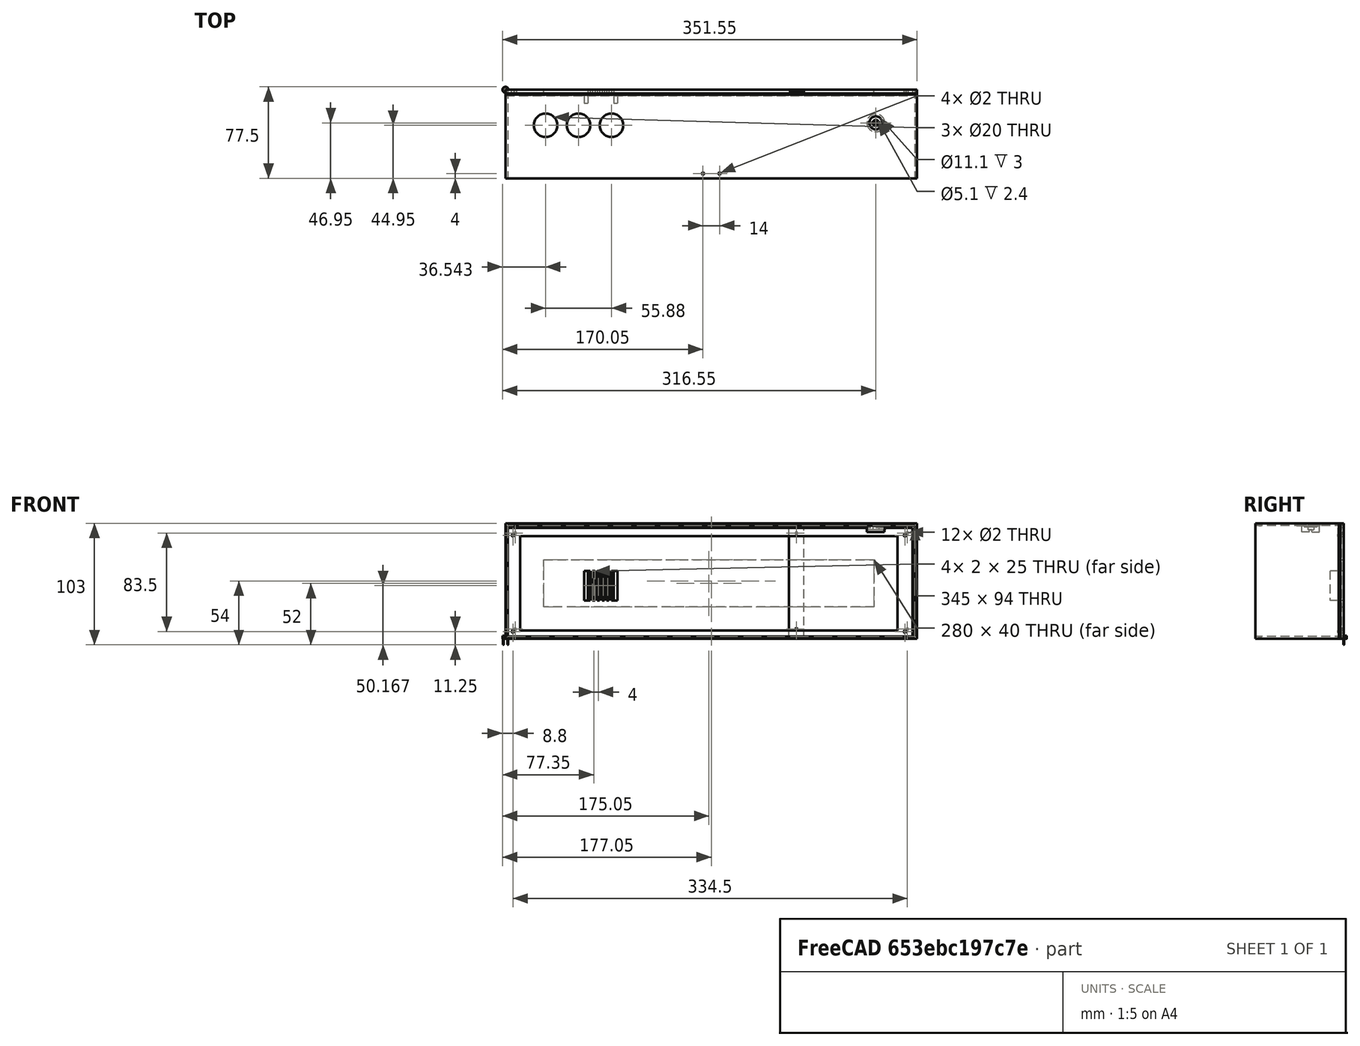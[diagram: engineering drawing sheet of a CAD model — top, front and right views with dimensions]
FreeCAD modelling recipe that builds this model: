
FCSTD DOCUMENT  (FreeCAD 1.0R39109 (Git))
Label: display
License: All rights reserved
LicenseURL: https://en.wikipedia.org/wiki/All_rights_reserved
objects: App::FeaturePython×42, App::Link×32, Sketcher::SketchObject×29, PartDesign::Plane×15, PartDesign::Pocket×10, PartDesign::Body×7, PartDesign::Pad×6, PartDesign::SubShapeBinder×5, PartDesign::Mirrored×4, App::DocumentObjectGroup×4, Spreadsheet::Sheet×2, PartDesign::MultiTransform×2, PartDesign::Line×2, Assembly::JointGroup×2, Assembly::AssemblyObject×2, PartDesign::FeatureBase×2, Assembly::ViewGroup×1, PartDesign::Point×1, PartDesign::Groove×1, PartDesign::Revolution×1, +2 more types
note: 161 computed .brp shape members not serialized (recipe doc carries the construction recipe); baked Part::Feature solids carry a one-line shape summary decoded from their .brp
EXTERNAL_REF file=Protoboard.FCStd obj=Spreadsheet004
EXTERNAL_REF file=grid.FCStd obj=Spreadsheet001
EXTERNAL_REF file=mount_stud.FCStd obj=Spreadsheet002
EXTERNAL_REF file=mount_bracket.FCStd obj=Spreadsheet
EXTERNAL_REF file=button.FCStd obj=Spreadsheet005
EXTERNAL_REF file=grid.FCStd obj=Body001
EXTERNAL_REF file=Protoboard.FCStd obj=Body007
EXTERNAL_REF file=mount_stud.FCStd obj=Body
EXTERNAL_REF file=button.FCStd obj=Body006
EXTERNAL_REF file=mount_bracket.FCStd obj=Body003
EXTERNAL_REF file=two_female_mount_bracket.FCStd obj=Body

FEATURE [Spreadsheet::Sheet] Spreadsheet  label="DisplaySS"
  cells = A1='Variant; B1='case_depth; C1='matrix_height; D1='matrix_width; E1='matrix_depth; F1='threaded_insert_depth; G1='threaded_insert_outer_diameter; H1='threaded_insert_safety_zone; I1='case_thickness; J1='grid_border_thickness; K1='grid_depth; L1='grid_intercell_spacing; M1='grid_cell_width; N1='led_x_count; O1='led_y_count; P1='grid_countersink_hole_depth; Q1='magnet_diameter; R1='magnet_height; S1='printer_tolerance_modifier; T1='screw_diameter; U1='mount_panel_exclusion_offset; V1='glass_thickness; W1='pcb_offset; X1='top_component_offset; Y1='photoresistor_diameter; Z1='photoresistor_truncated_width; AA1='photoresistor_height; AB1='top_component_horizontal_offset; AC1='top_component_spacing; AD1='photoresistor_ledge_size; AE1='back_plate_thickness; AF1='button_diameter; AG1='button_count; AH1='button_spacing; AI1='dht_height; AJ1='dht_width; AK1='dht_depth; AL1='dht_grill_diameter; A2==hiddenref(Body.Configuration.String); B2(case_depth)==.B3; C2(matrix_height)==.C3; D2(matrix_width)==.D3; E2(matrix_depth)==.E3; F2(threaded_insert_depth)==.F3; G2(threaded_insert_outer_diameter)==.G3; H2(threaded_insert_safety_zone)==.H3; I2(case_thickness)==.I3; J2(grid_border_thickness)==.J3; K2(grid_depth)==.K3; L2(grid_intercell_spacing)==.L3; M2(grid_cell_width)==.M3; N2(led_x_count)==.N3; O2(led_y_count)==.O3; P2(grid_countersink_hole_depth)==.P3; Q2(magnet_diameter)==.Q3; R2(magnet_height)==.R3; S2(printer_tolerance_modifier)==.S3; T2(screw_diameter)==.T3; U2(mount_panel_exclusion_offset)==.U3; V2(glass_thickness)==.V3; W2(pcb_offset)==.W3; X2(top_component_offset)==.X3; Y2(photoresistor_diameter)==.Y3; Z2(photoresistor_truncated_width)==.Z3; AA2(photoresistor_height)==.AA3; AB2(top_component_horizontal_offset)==.AB3; AC2(top_component_spacing)==.AC3; AD2(photoresistor_ledge_size)==.AD3; AE2(back_plate_thickness)==.AE3; AF2(button_diameter)==.AF3; AG2(button_count)==.AG3; AH2(button_spacing)==.AH3; AI2(dht_height)==.AI3; AJ2(dht_width)==.AJ3; AK2(dht_depth)==.AK3; AL2(dht_grill_diameter)==.AL3; A3='A; B3==75 mm; C3==80 mm; D3==320 mm; E3==2 mm; F3==4 mm; G3==5 mm; H3==2 mm; I3==2 mm; J3==3 mm; K3==8 mm; L3==1 mm; M3==9 mm; N3=32; O3=8; P3==3 mm; Q3==5 mm; R3==2.8 mm; S3==1 mm; T3==2 mm; U3==2 cm; V3==3 mm; W3==2 mm; X3==pcb_offset + <<Protoboard>>#<<ProtoboardSS>>.total_width / 2; Y3==5.1 mm; Z3==4.5 mm; AA3==2.4 mm; AB3==35 mm; AC3==0.5 cm; AD3==3 mm; AE3==4 mm; AF3==2.54 * 9 mm; AG3=3; AH3==2.54 * 2 mm; AI3==25.1 mm; AJ3==15.1 mm; AK3==7.7 mm; AL3==30 mm
  expr: .cells.Bind.B2.ZZ2 = tuple(.cells; <<B>> + str(hiddenref(Body.Configuration) + 3); <<ZZ>> + str(hiddenref(Body.Configuration) + 3))
FEATURE [Spreadsheet::Sheet] Spreadsheet001  label="CalculatedSS"
  cells = B1='grid_horizontal_padding; C1='grid_vertical_padding; D1='case_height; E1='case_width; F1='grid_width; G1='grid_height; H1='grid_matrix_width; I1='grid_matrix_height; J1='screw_horizontal_offset; K1='screw_vertical_offset; L1='grid_magnet_vertical_offset; M1='grid_magnet_horizontal_offset; N1='grid_magnet_depth; O1='case_clear_opening_height; P1='case_clear_opening_width; Q1='mounting_plate_thickness; R1='mount_bracket_face_size; S1='mount_bracket_length; T1='mount_bracket_draft_angle; U1='case_relative_magnet_horizontal_offset; V1='case_relative_magnet_vertical_offset; W1='mount_face_offset; X1='photoresistor_well_height; Y1='photoresistor_well_diameter; Z1='backplate_screw_offset_x; AA1='backplate_screw_offset_x; AB1='dht_vertical_offset; AC1='dht_horizontal_offset; AD1='pin_offset; AE1='protoboard_offset; AF1='protoboard_max_extent; AG1='protoboard_long_stud_clearance; AH1='button_mount_offset; AI1='button_pattern_extent; AJ1='back_plate_width; AK1='back_plate_height; AL1='split_offset; B2(grid_horizontal_padding)==<<DisplaySS>>.threaded_insert_outer_diameter + <<DisplaySS>>.threaded_insert_safety_zone * 2 + <<DisplaySS>>.grid_border_thickness + <<DisplaySS>>.grid_intercell_spacing / 2; C2(grid_vertical_padding)==grid#<<GridCalculatedSS>>.grid_vertical_padding; D2(case_height)==grid_height + <<DisplaySS>>.case_thickness * 2; E2(case_width)==grid_width + <<DisplaySS>>.case_thickness * 2; F2(grid_width)==grid_horizontal_padding * 2 + <<DisplaySS>>.matrix_width; G2(grid_height)==grid#<<GridCalculatedSS>>.grid_height; H2(grid_matrix_width)==grid_width - 2 * grid_horizontal_padding - 10 mm; I2(grid_matrix_height)=70; J2(screw_horizontal_offset)==grid_horizontal_padding / 2; K2(screw_vertical_offset)==mount_bracket_face_size / 2; L2(grid_magnet_vertical_offset)==grid#<<GridCalculatedSS>>.grid_magnet_vertical_offset; M2(grid_magnet_horizontal_offset)==grid#<<GridCalculatedSS>>.grid_magnet_horizontal_offset; N2(grid_magnet_depth)==<<DisplaySS>>.magnet_height * 2; O2(case_clear_opening_height)==grid_height; P2(case_clear_opening_width)==grid_width; Q2(mounting_plate_thickness)==<<DisplaySS>>.matrix_depth + 3 mm; R2(mount_bracket_face_size)==screw_horizontal_offset * 2; S2(mount_bracket_length)==mount_bracket_face_size / tan(mount_bracket_draft_angle) + <<DisplaySS>>.threaded_insert_depth; T2(mount_bracket_draft_angle)==35 deg; U2(case_relative_magnet_horizontal_offset)==grid_magnet_horizontal_offset + <<DisplaySS>>.case_thickness; V2(case_relative_magnet_vertical_offset)==grid_magnet_vertical_offset + <<DisplaySS>>.case_thickness; W2(mount_face_offset)==<<DisplaySS>>.case_depth - <<DisplaySS>>.grid_depth - mounting_plate_thickness; X2(photoresistor_well_height)==<<DisplaySS>>.glass_thickness + <<DisplaySS>>.photoresistor_height; Y2(photoresistor_well_diameter)==<<DisplaySS>>.photoresistor_diameter + <<DisplaySS>>.photoresistor_ledge_size * 2 + <<DisplaySS>>.case_thickness * 2; Z2(backplate_screw_offset_x)==mount_bracket_face_size / 2 + <<DisplaySS>>.case_thickness; AA2(backplate_screw_offset_y)==mount_bracket_face_size / 2 + <<DisplaySS>>.case_thickness; AB2(dht_vertical_offset)==case_height / 3; AC2(dht_horizontal_offset)==case_width / 5; AD2(pin_offset)==<<Protoboard>>#<<ProtoboardSS>>.first_pin_row_start; AE2(protoboard_offset)==40 mm; AF2(protoboard_max_extent)==protoboard_offset + <<Protoboard>>#<<ProtoboardSS>>.total_length; AG2(protoboard_long_stud_clearance)==<<mount_stud>>#<<MountStudSS>>.base_diameter / 2 - <<Protoboard>>#<<ProtoboardSS>>.mount_top_offset; AH2(button_mount_offset)==<<Protoboard>>#<<ProtoboardSS>>.mount_spacing_length / 2 - <<Protoboard>>#<<ProtoboardSS>>.pin_width / 2; AI2(button_pattern_extent)==<<DisplaySS>>.button_diameter * (<<DisplaySS>>.button_count - 1) + <<DisplaySS>>.button_spacing * (<<DisplaySS>>.button_count - 1); AJ2(back_plate_width)==case_width; AK2(back_plate_height)==case_height; AL2(split_offset)==253 mm
FEATURE [Sketcher::SketchObject] Sketch
  ArcFitTolerance = 1e-06
  AttachmentSupport = -> [XY_Plane]
  FullyConstrained = true
  MakeInternals = false
  MapMode = 3
  Placement = pos=(0,0,0) rot=(1,0,0;1.5708rad)
  expr: Constraints[10] = <<CalculatedSS>>.case_height
  expr: Constraints[9] = <<CalculatedSS>>.case_width
  sketch-geometry (4):
    g0: LineSegment StartX=0 StartY=0 StartZ=0 EndX=349 EndY=0 EndZ=0
    g1: LineSegment StartX=349 StartY=0 StartZ=0 EndX=349 EndY=98 EndZ=0
    g2: LineSegment StartX=349 StartY=98 StartZ=0 EndX=0 EndY=98 EndZ=0
    g3: LineSegment StartX=0 StartY=98 StartZ=0 EndX=0 EndY=0 EndZ=0
  constraints (11):
    c: Coincident(g0,g1)
    c: Coincident(g1,g2)
    c: Coincident(g2,g3)
    c: Coincident(g3,g0)
    c: Horizontal(g0)
    c: Horizontal(g2)
    c: Vertical(g1)
    c: Vertical(g3)
    c: Coincident(g0,g-1)
    c: Distance(g0) = 349
    c: Distance(g3) = 98
FEATURE [Sketcher::SketchObject] Sketch001
  ArcFitTolerance = 1e-06
  AttachmentSupport = -> [XY_Plane]
  FullyConstrained = true
  MakeInternals = false
  MapMode = 3
  Placement = pos=(0,0,0) rot=(1,0,0;1.5708rad)
  expr: Constraints[10] = <<CalculatedSS>>.case_width - <<DisplaySS>>.case_thickness
  expr: Constraints[11] = <<CalculatedSS>>.case_height - <<DisplaySS>>.case_thickness
  expr: Constraints[8] = <<DisplaySS>>.case_thickness
  expr: Constraints[9] = <<DisplaySS>>.case_thickness
  sketch-geometry (4):
    g0: LineSegment StartX=2 StartY=2 StartZ=0 EndX=347 EndY=2 EndZ=0
    g1: LineSegment StartX=347 StartY=2 StartZ=0 EndX=347 EndY=96 EndZ=0
    g2: LineSegment StartX=347 StartY=96 StartZ=0 EndX=2 EndY=96 EndZ=0
    g3: LineSegment StartX=2 StartY=96 StartZ=0 EndX=2 EndY=2 EndZ=0
  constraints (12):
    c: Coincident(g0,g1)
    c: Coincident(g1,g2)
    c: Coincident(g2,g3)
    c: Coincident(g3,g0)
    c: Horizontal(g0)
    c: Horizontal(g2)
    c: Vertical(g1)
    c: Vertical(g3)
    c: DistanceX(g-2,g0) = 2
    c: DistanceY(g-1,g0) = 2
    c: DistanceX(g-2,g1) = 347
    c: DistanceY(g-1,g1) = 96
FEATURE [PartDesign::Pad] Pad
  Direction = (0,-1,2e-16)
  Length = 75
  Length2 = 10
  Profile = -> Sketch
  ReferenceAxis = -> Sketch [N_Axis]
  Refine = true
  Suppressed = false
  Type = 0
  expr: Length = <<DisplaySS>>.case_depth
FEATURE [PartDesign::Pocket] Pocket
  BaseFeature = -> Pad
  Direction = (0,1,-2e-16)
  Length = 5
  Length2 = 5
  Profile = -> Sketch001
  ReferenceAxis = -> Sketch001 [N_Axis]
  Refine = true
  Reversed = true
  Suppressed = false
  Type = 1
FEATURE [PartDesign::Plane] DatumPlane
  AttachmentOffset = pos=(0,0,67) rot=(0,0,1;0rad)
  AttachmentSupport = -> [XZ_Plane]
  Length = 416.896
  MapMode = 2
  Placement = pos=(0,-67,1.49e-14) rot=(1,0,0;1.5708rad)
  ResizeMode = 0
  Width = 165.896
  expr: .AttachmentOffset.Base.z = <<DisplaySS>>.case_depth - <<DisplaySS>>.grid_depth
FEATURE [Sketcher::SketchObject] Sketch006  label="MountingPlateSketch"
  ArcFitTolerance = 1e-06
  AttachmentSupport = -> [XZ_Plane002]
  FullyConstrained = true
  MakeInternals = false
  MapMode = 5
  Placement = pos=(0,0,0) rot=(1,0,0;1.5708rad)
  expr: Constraints[10] = <<CalculatedSS>>.case_clear_opening_height
  expr: Constraints[9] = <<CalculatedSS>>.case_clear_opening_width
  sketch-geometry (4):
    g0: LineSegment StartX=0 StartY=0 StartZ=0 EndX=345 EndY=0 EndZ=0
    g1: LineSegment StartX=345 StartY=0 StartZ=0 EndX=345 EndY=94 EndZ=0
    g2: LineSegment StartX=345 StartY=94 StartZ=0 EndX=0 EndY=94 EndZ=0
    g3: LineSegment StartX=0 StartY=94 StartZ=0 EndX=0 EndY=0 EndZ=0
  constraints (11):
    c: Coincident(g0,g1)
    c: Coincident(g1,g2)
    c: Coincident(g2,g3)
    c: Coincident(g3,g0)
    c: Horizontal(g0)
    c: Horizontal(g2)
    c: Vertical(g1)
    c: Vertical(g3)
    c: Coincident(g0,g-1)
    c: Distance(g0) = 345
    c: Distance(g3) = 94
FEATURE [PartDesign::Pad] Pad002  label="MountingPlatePad"
  Direction = (0,-1,2e-16)
  Length = 5
  Length2 = 10
  Placement = pos=(0,0,0) rot=(1,0,0;1.5708rad)
  Profile = -> Sketch006
  ReferenceAxis = -> Sketch006 [N_Axis]
  Refine = true
  Suppressed = false
  Type = 0
  expr: Length = <<CalculatedSS>>.mounting_plate_thickness
FEATURE [Sketcher::SketchObject] Sketch007  label="Mounting Plate Screw Hole"
  ArcFitTolerance = 1e-06
  AttachmentSupport = -> [XZ_Plane002]
  FullyConstrained = true
  MakeInternals = false
  MapMode = 5
  Placement = pos=(0,0,0) rot=(1,0,0;1.5708rad)
  expr: Constraints[0] = <<DisplaySS>>.screw_diameter
  expr: Constraints[1] = <<CalculatedSS>>.screw_horizontal_offset
  expr: Constraints[2] = <<CalculatedSS>>.screw_vertical_offset
  sketch-geometry (1):
    g0: Circle CenterX=6.25 CenterY=6.25 CenterZ=0 NormalX=0 NormalY=0 NormalZ=1 AngleXU=0 Radius=1
  constraints (3):
    c: Diameter(g0) = 2
    c: DistanceX(g-2,g0) = 6.25
    c: DistanceY(g-1,g0) = 6.25
FEATURE [PartDesign::Pocket] Pocket004  label="MountingPlateScrewHolePocket"
  BaseFeature = -> Pad002
  Direction = (0,1,-2e-16)
  Length = 5
  Length2 = 5
  Placement = pos=(0,0,0) rot=(1,0,0;1.5708rad)
  Profile = -> Sketch007
  ReferenceAxis = -> Sketch007 [N_Axis]
  Refine = true
  Reversed = true
  Suppressed = false
  Type = 0
  expr: Length = <<CalculatedSS>>.mounting_plate_thickness
FEATURE [PartDesign::Plane] DatumPlane004  label="Mounting Case Horizontal Dividing Plane"
  AttachmentOffset = pos=(0,0,-47) rot=(0,0,1;0rad)
  AttachmentSupport = -> [XZ_Plane002]
  Length = 397.203
  MapMode = 3
  Placement = pos=(0,0,47) rot=(1,0,0;3.14159rad)
  ResizeMode = 0
  Width = 77.2029
  expr: .AttachmentOffset.Base.z = <<CalculatedSS>>.case_clear_opening_height / 2 * -1
FEATURE [PartDesign::Plane] DatumPlane005  label="MountingCaseVerticalDividingPlane"
  AttachmentOffset = pos=(0,0,172.5) rot=(0,0,1;0rad)
  AttachmentSupport = -> [YZ_Plane002]
  Length = 65.4272
  MapMode = 5
  Placement = pos=(172.5,0,0) rot=(0.57735,0.57735,0.57735;2.0944rad)
  ResizeMode = 0
  Width = 134.427
  expr: .AttachmentOffset.Base.z = <<CalculatedSS>>.case_clear_opening_width / 2
FEATURE [PartDesign::Mirrored] Mirrored004
  MirrorPlane = -> DatumPlane004
  Placement = pos=(0,0,0) rot=(1,0,0;1.5708rad)
  Refine = true
  Suppressed = false
  TransformMode = 0
FEATURE [PartDesign::Mirrored] Mirrored005
  MirrorPlane = -> DatumPlane005
  Placement = pos=(0,0,0) rot=(1,0,0;1.5708rad)
  Refine = true
  Suppressed = false
  TransformMode = 0
FEATURE [PartDesign::MultiTransform] MultiTransform003  label="MountingPlateScrewHoles"
  BaseFeature = -> Pocket004
  Originals = -> [Pocket004]
  Placement = pos=(0,0,0) rot=(1,0,0;1.5708rad)
  Refine = true
  Suppressed = false
  TransformMode = 0
  Transformations = -> [Mirrored004,Mirrored005]
FEATURE [PartDesign::Plane] DatumPlane006  label="MountingPlateFacePlane"
  AttachmentOffset = pos=(0,0,5) rot=(0,0,1;0rad)
  AttachmentSupport = -> [XZ_Plane002]
  Length = 411.967
  MapMode = 5
  Placement = pos=(0,-5,1.1e-15) rot=(1,0,0;1.5708rad)
  ResizeMode = 0
  Width = 160.967
  expr: .AttachmentOffset.Base.z = <<CalculatedSS>>.mounting_plate_thickness
FEATURE [Sketcher::SketchObject] Sketch008  label="LedPanelSketch"
  ArcFitTolerance = 1e-06
  AttachmentSupport = -> [DatumPlane006]
  FullyConstrained = true
  MakeInternals = false
  MapMode = 5
  Placement = pos=(0,-5,1.1e-15) rot=(1,0,0;1.5708rad)
  expr: Constraints[10] = <<CalculatedSS>>.case_clear_opening_height - <<CalculatedSS>>.grid_vertical_padding
  expr: Constraints[11] = <<CalculatedSS>>.case_clear_opening_width - <<CalculatedSS>>.grid_horizontal_padding
  expr: Constraints[8] = <<CalculatedSS>>.grid_vertical_padding
  expr: Constraints[9] = <<CalculatedSS>>.grid_horizontal_padding
  sketch-geometry (4):
    g0: LineSegment StartX=12.5 StartY=87 StartZ=0 EndX=12.5 EndY=7 EndZ=0
    g1: LineSegment StartX=12.5 StartY=7 StartZ=0 EndX=332.5 EndY=7 EndZ=0
    g2: LineSegment StartX=332.5 StartY=7 StartZ=0 EndX=332.5 EndY=87 EndZ=0
    g3: LineSegment StartX=332.5 StartY=87 StartZ=0 EndX=12.5 EndY=87 EndZ=0
  constraints (12):
    c: Coincident(g0,g1)
    c: Coincident(g1,g2)
    c: Coincident(g2,g3)
    c: Coincident(g3,g0)
    c: Vertical(g0)
    c: Vertical(g2)
    c: Horizontal(g1)
    c: Horizontal(g3)
    c: DistanceY(g-1,g0) = 7
    c: DistanceX(g-2,g0) = 12.5
    c: DistanceY(g-1,g0) = 87
    c: DistanceX(g-2,g1) = 332.5
FEATURE [PartDesign::Pocket] Pocket005  label="LEDMatrixPocket"
  BaseFeature = -> MultiTransform003
  Direction = (0,1,-2e-16)
  Length = 2
  Length2 = 5
  Placement = pos=(0,0,0) rot=(1,0,0;1.5708rad)
  Profile = -> Sketch008
  ReferenceAxis = -> Sketch008 [N_Axis]
  Refine = true
  Suppressed = false
  Type = 0
  expr: Length = <<DisplaySS>>.matrix_depth
FEATURE [Sketcher::SketchObject] Sketch009  label="MountPanelPassThroughSketch"
  ArcFitTolerance = 1e-06
  AttachmentSupport = -> [DatumPlane006]
  FullyConstrained = true
  MakeInternals = false
  MapMode = 5
  Placement = pos=(0,-5,1.1e-15) rot=(1,0,0;1.5708rad)
  expr: Constraints[10] = <<DisplaySS>>.matrix_width - <<DisplaySS>>.mount_panel_exclusion_offset * 2
  expr: Constraints[11] = <<DisplaySS>>.mount_panel_exclusion_offset + <<CalculatedSS>>.grid_horizontal_padding
  expr: Constraints[8] = <<CalculatedSS>>.grid_vertical_padding + <<DisplaySS>>.mount_panel_exclusion_offset
  expr: Constraints[9] = <<CalculatedSS>>.case_clear_opening_height - <<CalculatedSS>>.grid_vertical_padding - <<DisplaySS>>.mount_panel_exclusion_offset
  sketch-geometry (4):
    g0: LineSegment StartX=32.5 StartY=67 StartZ=0 EndX=32.5 EndY=27 EndZ=0
    g1: LineSegment StartX=32.5 StartY=27 StartZ=0 EndX=312.5 EndY=27 EndZ=0
    g2: LineSegment StartX=312.5 StartY=27 StartZ=0 EndX=312.5 EndY=67 EndZ=0
    g3: LineSegment StartX=312.5 StartY=67 StartZ=0 EndX=32.5 EndY=67 EndZ=0
  constraints (12):
    c: Coincident(g0,g1)
    c: Coincident(g1,g2)
    c: Coincident(g2,g3)
    c: Coincident(g3,g0)
    c: Vertical(g0)
    c: Vertical(g2)
    c: Horizontal(g1)
    c: Horizontal(g3)
    c: DistanceY(g-1,g0) = 27
    c: DistanceY(g-1,g0) = 67
    c: Distance(g3) = 280
    c: DistanceX(g-2,g0) = 32.5
FEATURE [PartDesign::Pocket] Pocket006  label="MountPanelPassThrough"
  BaseFeature = -> Pocket005
  Direction = (0,1,-2e-16)
  Length = 5
  Length2 = 5
  Placement = pos=(0,0,0) rot=(1,0,0;1.5708rad)
  Profile = -> Sketch009
  ReferenceAxis = -> Sketch009 [N_Axis]
  Refine = true
  Suppressed = false
  Type = 1
FEATURE [PartDesign::Body] Body002  label="Mounting Plate"
  AllowCompound = false
  Group = -> [Sketch006,Pad002,Sketch007,Pocket004,DatumPlane004,DatumPlane005,MultiTransform003,Mirrored004,Mirrored005,DatumPlane006,Sketch008,Pocket005,Sketch009,Pocket006]
  Origin = -> Origin002
  Tip = -> Pocket006
FEATURE [Sketcher::SketchObject] Sketch012
  ArcFitTolerance = 1e-06
  AttachmentSupport = -> [XZ_Plane004]
  FullyConstrained = true
  MakeInternals = false
  MapMode = 5
  Placement = pos=(0,0,0) rot=(1,0,0;1.5708rad)
  expr: Constraints[10] = <<CalculatedSS>>.case_width
  expr: Constraints[9] = <<CalculatedSS>>.case_height
  sketch-geometry (4):
    g0: LineSegment StartX=0 StartY=0 StartZ=0 EndX=349 EndY=0 EndZ=0
    g1: LineSegment StartX=349 StartY=0 StartZ=0 EndX=349 EndY=98 EndZ=0
    g2: LineSegment StartX=349 StartY=98 StartZ=0 EndX=0 EndY=98 EndZ=0
    g3: LineSegment StartX=0 StartY=98 StartZ=0 EndX=0 EndY=0 EndZ=0
  constraints (11):
    c: Coincident(g0,g1)
    c: Coincident(g1,g2)
    c: Coincident(g2,g3)
    c: Coincident(g3,g0)
    c: Horizontal(g0)
    c: Horizontal(g2)
    c: Vertical(g1)
    c: Vertical(g3)
    c: Coincident(g0,g-1)
    c: Distance(g3) = 98
    c: Distance(g0) = 349
FEATURE [PartDesign::Pad] Pad004  label="Glass"
  Direction = (0,-1,2e-16)
  Length = 3
  Length2 = 10
  Placement = pos=(0,0,0) rot=(1,0,0;1.5708rad)
  Profile = -> Sketch012
  ReferenceAxis = -> Sketch012 [N_Axis]
  Refine = true
  Suppressed = false
  Type = 0
  expr: Length = <<DisplaySS>>.glass_thickness
FEATURE [Sketcher::SketchObject] Sketch014
  ArcFitTolerance = 1e-06
  AttachmentSupport = -> [XY_Plane006]
  FullyConstrained = true
  MakeInternals = false
  MapMode = 5
  expr: Constraints[1] = <<DisplaySS>>.magnet_diameter
  sketch-geometry (1):
    g0: Circle CenterX=0 CenterY=0 CenterZ=0 NormalX=0 NormalY=0 NormalZ=1 AngleXU=0 Radius=2.5
  constraints (2):
    c: Coincident(g0,g-1)
    c: Diameter(g0) = 5
FEATURE [App::Link] Housing  label="Housing001"
  LinkedObject = -> Body
FEATURE [App::FeaturePython] GroundedJoint  # Assembly grounded joint (typed FeaturePython)
  ObjectToGround = -> Housing
FEATURE [App::Link] Screen  label="Screen001"
  LinkPlacement = pos=(0,-75,9.41e-14) rot=(0,0,1;0rad)
  LinkedObject = -> Body004
  Placement = pos=(0,-75,9.41e-14) rot=(0,0,1;0rad)
FEATURE [PartDesign::Pad] Pad005  label="MagnetPad"
  Direction = (0,0,1)
  Length = 2.8
  Length2 = 10
  Profile = -> Sketch014
  ReferenceAxis = -> Sketch014 [N_Axis]
  Refine = true
  Suppressed = false
  Type = 0
  expr: Length = <<DisplaySS>>.magnet_height
FEATURE [PartDesign::Body] Body005  label="MagnetBody"
  AllowCompound = false
  Group = -> [Sketch014,Pad005]
  Origin = -> Origin006
  Tip = -> Pad005
FEATURE [Sketcher::SketchObject] Sketch013  label="Magnet Placement"
  ArcFitTolerance = 1e-06
  AttachmentSupport = -> [XZ_Plane004]
  FullyConstrained = true
  MakeInternals = false
  MapMode = 5
  Placement = pos=(0,0,0) rot=(1,0,0;1.5708rad)
  expr: Constraints[0] = <<CalculatedSS>>.case_relative_magnet_vertical_offset
  expr: Constraints[10] = <<CalculatedSS>>.case_width - <<CalculatedSS>>.case_relative_magnet_horizontal_offset
  expr: Constraints[11] = <<CalculatedSS>>.case_relative_magnet_vertical_offset
  expr: Constraints[1] = <<CalculatedSS>>.case_relative_magnet_horizontal_offset
  expr: Constraints[2] = <<DisplaySS>>.magnet_diameter
  expr: Constraints[3] = <<DisplaySS>>.magnet_diameter
  expr: Constraints[4] = <<DisplaySS>>.magnet_diameter
  expr: Constraints[5] = <<DisplaySS>>.magnet_diameter
  expr: Constraints[6] = <<CalculatedSS>>.case_height - <<CalculatedSS>>.case_relative_magnet_vertical_offset
  expr: Constraints[7] = <<CalculatedSS>>.case_height - <<CalculatedSS>>.case_relative_magnet_vertical_offset
  expr: Constraints[8] = <<CalculatedSS>>.case_relative_magnet_horizontal_offset
  expr: Constraints[9] = <<CalculatedSS>>.case_width - <<CalculatedSS>>.case_relative_magnet_horizontal_offset
  sketch-geometry (4):
    g0: Circle CenterX=8.25 CenterY=20.8 CenterZ=0 NormalX=0 NormalY=0 NormalZ=1 AngleXU=0 Radius=2.5
    g1: Circle CenterX=8.25 CenterY=77.2 CenterZ=0 NormalX=0 NormalY=0 NormalZ=1 AngleXU=0 Radius=2.5
    g2: Circle CenterX=340.75 CenterY=77.2 CenterZ=0 NormalX=0 NormalY=0 NormalZ=1 AngleXU=0 Radius=2.5
    g3: Circle CenterX=340.75 CenterY=20.8 CenterZ=0 NormalX=0 NormalY=0 NormalZ=1 AngleXU=0 Radius=2.5
  constraints (12):
    c: DistanceY(g-1,g0) = 20.8
    c: DistanceX(g-2,g0) = 8.25
    c: Diameter(g0) = 5
    c: Diameter(g1) = 5
    c: Diameter(g2) = 5
    c: Diameter(g3) = 5
    c: DistanceY(g-1,g1) = 77.2
    c: DistanceY(g-1,g2) = 77.2
    c: DistanceX(g-2,g1) = 8.25
    c: DistanceX(g-2,g2) = 340.75
    c: DistanceX(g-2,g3) = 340.75
    c: DistanceY(g-1,g3) = 20.8
FEATURE [PartDesign::Body] Body004  label="Screen"
  AllowCompound = false
  Group = -> [Sketch012,Pad004,Sketch013]
  Origin = -> Origin004
  Tip = -> Pad004
FEATURE [PartDesign::Plane] DatumPlane007  label="RightInsidePlane"
  AttachmentOffset = pos=(0,0,2) rot=(0,0,1;0rad)
  AttachmentSupport = -> [YZ_Plane]
  Length = 122.181
  MapMode = 5
  Placement = pos=(2,0,0) rot=(0.57735,0.57735,0.57735;2.0944rad)
  ResizeMode = 0
  Width = 145.181
  expr: .AttachmentOffset.Base.z = <<DisplaySS>>.case_thickness
FEATURE [PartDesign::Plane] DatumPlane008  label="LeftInsidePlane"
  AttachmentOffset = pos=(0,0,347) rot=(0,0,1;0rad)
  AttachmentSupport = -> [YZ_Plane]
  Length = 122.181
  MapMode = 5
  Placement = pos=(347,0,0) rot=(0.57735,0.57735,0.57735;2.0944rad)
  ResizeMode = 0
  Width = 145.181
  expr: .AttachmentOffset.Base.z = <<CalculatedSS>>.case_width - <<DisplaySS>>.case_thickness
FEATURE [Sketcher::SketchObject] Sketch015
  ArcFitTolerance = 1e-06
  AttachmentSupport = -> [DatumPlane007]
  FullyConstrained = true
  MakeInternals = false
  MapMode = 5
  Placement = pos=(2,0,0) rot=(0.57735,0.57735,0.57735;2.0944rad)
  expr: Constraints[10] = <<CalculatedSS>>.screw_vertical_offset + <<DisplaySS>>.case_thickness + <<CalculatedSS>>.mount_bracket_face_size / 2
  expr: Constraints[11] = <<CalculatedSS>>.mount_face_offset * -1
  expr: Constraints[20] = <<CalculatedSS>>.mount_face_offset * -1
  expr: Constraints[21] = <<CalculatedSS>>.case_height - <<DisplaySS>>.case_thickness - <<CalculatedSS>>.screw_vertical_offset - <<CalculatedSS>>.mount_bracket_face_size / 2
  expr: Constraints[22] = <<CalculatedSS>>.mount_bracket_face_size
  expr: Constraints[23] = <<CalculatedSS>>.mount_bracket_length
  expr: Constraints[32] = <<CalculatedSS>>.case_height - <<DisplaySS>>.case_thickness
  expr: Constraints[33] = <<CalculatedSS>>.mount_bracket_face_size
  expr: Constraints[34] = <<CalculatedSS>>.mount_bracket_length
  expr: Constraints[43] = <<DisplaySS>>.case_thickness
  expr: Constraints[44] = <<CalculatedSS>>.mount_bracket_face_size
  expr: Constraints[45] = <<CalculatedSS>>.mount_bracket_length
  expr: Constraints[46] = <<DisplaySS>>.back_plate_thickness * -1
  expr: Constraints[47] = <<DisplaySS>>.back_plate_thickness * -1
  expr: Constraints[8] = <<CalculatedSS>>.mount_bracket_length
  expr: Constraints[9] = <<CalculatedSS>>.mount_bracket_face_size
  sketch-geometry (16):
    g0: LineSegment StartX=-62 StartY=2 StartZ=0 EndX=-62 EndY=14.5 EndZ=0
    g1: LineSegment StartX=-62 StartY=14.5 StartZ=0 EndX=-40.1481 EndY=14.5 EndZ=0
    g2: LineSegment StartX=-40.1481 StartY=14.5 StartZ=0 EndX=-40.1481 EndY=2 EndZ=0
    g3: LineSegment StartX=-40.1481 StartY=2 StartZ=0 EndX=-62 EndY=2 EndZ=0
    g4: LineSegment StartX=-62 StartY=83.5 StartZ=0 EndX=-62 EndY=96 EndZ=0
    g5: LineSegment StartX=-62 StartY=96 StartZ=0 EndX=-40.1481 EndY=96 EndZ=0
    g6: LineSegment StartX=-40.1481 StartY=96 StartZ=0 EndX=-40.1481 EndY=83.5 EndZ=0
    g7: LineSegment StartX=-40.1481 StartY=83.5 StartZ=0 EndX=-62 EndY=83.5 EndZ=0
    g8: LineSegment StartX=-25.8519 StartY=96 StartZ=0 EndX=-25.8519 EndY=83.5 EndZ=0
    g9: LineSegment StartX=-25.8519 StartY=83.5 StartZ=0 EndX=-4 EndY=83.5 EndZ=0
    g10: LineSegment StartX=-4 StartY=83.5 StartZ=0 EndX=-4 EndY=96 EndZ=0
    g11: LineSegment StartX=-4 StartY=96 StartZ=0 EndX=-25.8519 EndY=96 EndZ=0
    g12: LineSegment StartX=-25.8519 StartY=14.5 StartZ=0 EndX=-25.8519 EndY=2 EndZ=0
    g13: LineSegment StartX=-25.8519 StartY=2 StartZ=0 EndX=-4 EndY=2 EndZ=0
    g14: LineSegment StartX=-4 StartY=2 StartZ=0 EndX=-4 EndY=14.5 EndZ=0
    g15: LineSegment StartX=-4 StartY=14.5 StartZ=0 EndX=-25.8519 EndY=14.5 EndZ=0
  constraints (48):
    c: Coincident(g0,g1)
    c: Coincident(g1,g2)
    c: Coincident(g2,g3)
    c: Coincident(g3,g0)
    c: Vertical(g0)
    c: Vertical(g2)
    c: Horizontal(g1)
    c: Horizontal(g3)
    c: Distance(g1) = 21.8519
    c: Distance(g2) = 12.5
    c: DistanceY(g-1,g1) = 14.5
    c: DistanceX(g-2,g0) = -62
    c: Coincident(g4,g5)
    c: Coincident(g5,g6)
    c: Coincident(g6,g7)
    c: Coincident(g7,g4)
    c: Vertical(g4)
    c: Vertical(g6)
    c: Horizontal(g5)
    c: Horizontal(g7)
    c: DistanceX(g-2,g4) = -62
    c: DistanceY(g-1,g4) = 83.5
    c: Distance(g4) = 12.5
    c: Distance(g5) = 21.8519
    c: Coincident(g8,g9)
    c: Coincident(g9,g10)
    c: Coincident(g10,g11)
    c: Coincident(g11,g8)
    c: Vertical(g8)
    c: Vertical(g10)
    c: Horizontal(g9)
    c: Horizontal(g11)
    c: DistanceY(g-1,g10) = 96
    c: Distance(g10) = 12.5
    c: Distance(g9) = 21.8519
    c: Coincident(g12,g13)
    c: Coincident(g13,g14)
    c: Coincident(g14,g15)
    c: Coincident(g15,g12)
    c: Vertical(g12)
    c: Vertical(g14)
    c: Horizontal(g13)
    c: Horizontal(g15)
    c: DistanceY(g-1,g13) = 2
    c: Distance(g12) = 12.5
    c: Distance(g15) = 21.8519
    c: DistanceX(g-2,g9) = -4
    c: DistanceX(g-2,g13) = -4
FEATURE [Sketcher::SketchObject] Sketch016
  ArcFitTolerance = 1e-06
  AttachmentSupport = -> [DatumPlane008]
  FullyConstrained = true
  MakeInternals = false
  MapMode = 5
  Placement = pos=(347,0,0) rot=(0.57735,0.57735,0.57735;2.0944rad)
  expr: Constraints[10] = Sketch015.Constraints[10]
  expr: Constraints[11] = Sketch015.Constraints[11]
  expr: Constraints[20] = Sketch015.Constraints[20]
  expr: Constraints[21] = Sketch015.Constraints[21]
  expr: Constraints[22] = Sketch015.Constraints[22]
  expr: Constraints[23] = Sketch015.Constraints[23]
  expr: Constraints[32] = Sketch015.Constraints[32]
  expr: Constraints[33] = Sketch015.Constraints[33]
  expr: Constraints[34] = Sketch015.Constraints[34]
  expr: Constraints[43] = Sketch015.Constraints[43]
  expr: Constraints[44] = Sketch015.Constraints[44]
  expr: Constraints[45] = Sketch015.Constraints[45]
  expr: Constraints[46] = Sketch015.Constraints[46]
  expr: Constraints[47] = Sketch015.Constraints[47]
  expr: Constraints[8] = Sketch015.Constraints[8]
  expr: Constraints[9] = Sketch015.Constraints[9]
  sketch-geometry (16):
    g0: LineSegment StartX=-62 StartY=2 StartZ=0 EndX=-62 EndY=14.5 EndZ=0
    g1: LineSegment StartX=-62 StartY=14.5 StartZ=0 EndX=-40.1481 EndY=14.5 EndZ=0
    g2: LineSegment StartX=-40.1481 StartY=14.5 StartZ=0 EndX=-40.1481 EndY=2 EndZ=0
    g3: LineSegment StartX=-40.1481 StartY=2 StartZ=0 EndX=-62 EndY=2 EndZ=0
    g4: LineSegment StartX=-62 StartY=83.5 StartZ=0 EndX=-62 EndY=96 EndZ=0
    g5: LineSegment StartX=-62 StartY=96 StartZ=0 EndX=-40.1481 EndY=96 EndZ=0
    g6: LineSegment StartX=-40.1481 StartY=96 StartZ=0 EndX=-40.1481 EndY=83.5 EndZ=0
    g7: LineSegment StartX=-40.1481 StartY=83.5 StartZ=0 EndX=-62 EndY=83.5 EndZ=0
    g8: LineSegment StartX=-25.8519 StartY=96 StartZ=0 EndX=-25.8519 EndY=83.5 EndZ=0
    g9: LineSegment StartX=-25.8519 StartY=83.5 StartZ=0 EndX=-4 EndY=83.5 EndZ=0
    g10: LineSegment StartX=-4 StartY=83.5 StartZ=0 EndX=-4 EndY=96 EndZ=0
    g11: LineSegment StartX=-4 StartY=96 StartZ=0 EndX=-25.8519 EndY=96 EndZ=0
    g12: LineSegment StartX=-25.8519 StartY=14.5 StartZ=0 EndX=-25.8519 EndY=2 EndZ=0
    g13: LineSegment StartX=-25.8519 StartY=2 StartZ=0 EndX=-4 EndY=2 EndZ=0
    g14: LineSegment StartX=-4 StartY=2 StartZ=0 EndX=-4 EndY=14.5 EndZ=0
    g15: LineSegment StartX=-4 StartY=14.5 StartZ=0 EndX=-25.8519 EndY=14.5 EndZ=0
  constraints (48):
    c: Coincident(g0,g1)
    c: Coincident(g1,g2)
    c: Coincident(g2,g3)
    c: Coincident(g3,g0)
    c: Vertical(g0)
    c: Vertical(g2)
    c: Horizontal(g1)
    c: Horizontal(g3)
    c: Distance(g1) = 21.8519
    c: Distance(g2) = 12.5
    c: DistanceY(g-1,g1) = 14.5
    c: DistanceX(g-2,g0) = -62
    c: Coincident(g4,g5)
    c: Coincident(g5,g6)
    c: Coincident(g6,g7)
    c: Coincident(g7,g4)
    c: Vertical(g4)
    c: Vertical(g6)
    c: Horizontal(g5)
    c: Horizontal(g7)
    c: DistanceX(g-2,g4) = -62
    c: DistanceY(g-1,g4) = 83.5
    c: Distance(g4) = 12.5
    c: Distance(g5) = 21.8519
    c: Coincident(g8,g9)
    c: Coincident(g9,g10)
    c: Coincident(g10,g11)
    c: Coincident(g11,g8)
    c: Vertical(g8)
    c: Vertical(g10)
    c: Horizontal(g9)
    c: Horizontal(g11)
    c: DistanceY(g-1,g10) = 96
    c: Distance(g10) = 12.5
    c: Distance(g9) = 21.8519
    c: Coincident(g12,g13)
    c: Coincident(g13,g14)
    c: Coincident(g14,g15)
    c: Coincident(g15,g12)
    c: Vertical(g12)
    c: Vertical(g14)
    c: Horizontal(g13)
    c: Horizontal(g15)
    c: DistanceY(g-1,g13) = 2
    c: Distance(g12) = 12.5
    c: Distance(g15) = 21.8519
    c: DistanceX(g-2,g9) = -4
    c: DistanceX(g-2,g13) = -4
FEATURE [App::FeaturePython] Move  # WARN: FeaturePython — macro-defined, semantics opaque (R4)
  MoveType = 0
  MovementTransform = pos=(0,-228,0) rot=(0,0,1;0rad)
  References = -> Assembly [Screen.]
FEATURE [App::FeaturePython] Move001  # WARN: FeaturePython — macro-defined, semantics opaque (R4)
  MoveType = 0
  MovementTransform = pos=(0,-176,-1e-05) rot=(-1.00436,0,0;0rad)
  References = -> Assembly [MagnetBody004.]
FEATURE [App::FeaturePython] Move002  # WARN: FeaturePython — macro-defined, semantics opaque (R4)
  MoveType = 0
  MovementTransform = pos=(0,-151,-1e-05) rot=(-1.00436,0,0;0rad)
  References = -> Assembly [MagnetBody005.]
FEATURE [App::FeaturePython] Move003  # WARN: FeaturePython — macro-defined, semantics opaque (R4)
  MoveType = 0
  MovementTransform = pos=(0,-195,9e-05) rot=(0,0,1;0rad)
  References = -> Assembly [MagnetBody006.]
FEATURE [App::FeaturePython] Move004  # WARN: FeaturePython — macro-defined, semantics opaque (R4)
  MoveType = 0
  MovementTransform = pos=(-1e-05,-210,0.00016) rot=(0,0,1;0rad)
  References = -> Assembly [MagnetBody007.]
FEATURE [App::FeaturePython] Move005  # WARN: FeaturePython — macro-defined, semantics opaque (R4)
  MoveType = 0
  MovementTransform = pos=(0,-165,-0.00014) rot=(1.00436,0,0;0rad)
  References = -> Assembly [MagnetBody.]
FEATURE [App::FeaturePython] Move006  # WARN: FeaturePython — macro-defined, semantics opaque (R4)
  MoveType = 0
  MovementTransform = pos=(0,-136,-0.0001) rot=(1.00436,0,0;0rad)
  References = -> Assembly [MagnetBody001.]
FEATURE [App::FeaturePython] Move007  # WARN: FeaturePython — macro-defined, semantics opaque (R4)
  MoveType = 0
  MovementTransform = pos=(0,-175.001,0.0001) rot=(0,0,1;0rad)
  References = -> Assembly [MagnetBody002.]
FEATURE [App::FeaturePython] Move008  # WARN: FeaturePython — macro-defined, semantics opaque (R4)
  MoveType = 0
  MovementTransform = pos=(-3e-05,-163.001,-2e-05) rot=(0,0,1;0rad)
  References = -> Assembly [MagnetBody003.]
FEATURE [App::FeaturePython] Move009  # WARN: FeaturePython — macro-defined, semantics opaque (R4)
  MoveType = 0
  MovementTransform = pos=(-2e-05,-123.001,-1e-05) rot=(0,0,1;0rad)
  References = -> Assembly [Grid.]
FEATURE [App::FeaturePython] Move010  # WARN: FeaturePython — macro-defined, semantics opaque (R4)
  MoveType = 0
  MovementTransform = pos=(0,-56.0002,-1e-05) rot=(0,0,1;0rad)
  References = -> Assembly [Mounting_Plate.]
FEATURE [App::FeaturePython] Exploded_View  # WARN: FeaturePython — macro-defined, semantics opaque (R4)
  Moves = -> [Move,Move001,Move002,Move003,Move004,Move005,Move006,Move007,Move008,Move009,Move010]
FEATURE [Assembly::ViewGroup] Exploded_Views
  Group = -> [Exploded_View]
FEATURE [PartDesign::Plane] DatumPlane009  label="CaseTopPlane"
  AttachmentOffset = pos=(0,0,98) rot=(0,0,1;0rad)
  AttachmentSupport = -> [XY_Plane]
  Length = 412.678
  MapMode = 5
  Placement = pos=(0,0,98) rot=(0,0,1;0rad)
  ResizeMode = 0
  Width = 138.678
  expr: .AttachmentOffset.Base.z = <<CalculatedSS>>.case_height
FEATURE [PartDesign::Plane] DatumPlane010
  AttachmentOffset = pos=(0,0,28.05) rot=(0,0,1;0rad)
  AttachmentSupport = -> [XZ_Plane]
  Length = 416.896
  MapMode = 5
  Placement = pos=(0,-28.05,6.2e-15) rot=(1,0,0;1.5708rad)
  ResizeMode = 0
  Width = 165.896
  expr: .AttachmentOffset.Base.z = <<DisplaySS>>.top_component_offset
FEATURE [PartDesign::Line] DatumLine
  AttacherType = Attacher::AttachEngineLine
  AttachmentOffset = pos=(-28.05,0,0) rot=(0,0,1;0rad)
  AttachmentSupport = -> [DatumPlane009]
  Length = 20
  MapMode = 16
  Placement = pos=(0,-28.05,98) rot=(0.57735,0.57735,0.57735;2.0944rad)
  ResizeMode = 0
  expr: .AttachmentOffset.Base.x = <<DisplaySS>>.top_component_offset * -1
FEATURE [PartDesign::Plane] DatumPlane011  label="TopComponentPlane"
  AttachmentOffset = pos=(0,0,28.05) rot=(0,0,1;0rad)
  AttachmentSupport = -> [XZ_Plane]
  Length = 416.896
  MapMode = 2
  Placement = pos=(0,-28.05,6.2e-15) rot=(1,0,0;1.5708rad)
  ResizeMode = 0
  Width = 165.896
  expr: .AttachmentOffset.Base.z = <<DisplaySS>>.top_component_offset
FEATURE [PartDesign::Point] DatumPoint
  AttacherType = Attacher::AttachEnginePoint
  AttachmentOffset = pos=(314,98,0) rot=(0,0,1;0rad)
  AttachmentSupport = -> [DatumPlane011]
  MapMode = 32
  Placement = pos=(314,-28.05,98) rot=(1,0,0;1.5708rad)
  expr: .AttachmentOffset.Base.x = <<CalculatedSS>>.case_width - <<DisplaySS>>.top_component_horizontal_offset
  expr: .AttachmentOffset.Base.y = <<CalculatedSS>>.case_height
FEATURE [PartDesign::Line] DatumLine001
  AttacherType = Attacher::AttachEngineLine
  AttachmentSupport = -> [DatumPoint,DatumPlane009]
  Length = 20
  MapMode = 46
  Placement = pos=(314,-28.05,98) rot=(0,0,1;3.14159rad)
  ResizeMode = 0
FEATURE [Sketcher::SketchObject] Sketch019
  ArcFitTolerance = 1e-06
  AttachmentSupport = -> [DatumPlane011]
  ExternalGeometry = -> [DatumPoint]
  FullyConstrained = true
  MakeInternals = false
  MapMode = 5
  Placement = pos=(0,-28.05,6.2e-15) rot=(1,0,0;1.5708rad)
  expr: Constraints[15] = <<DisplaySS>>.photoresistor_diameter / 2
  expr: Constraints[16] = <<DisplaySS>>.photoresistor_ledge_size
  expr: Constraints[17] = <<DisplaySS>>.glass_thickness
  expr: Constraints[18] = <<DisplaySS>>.case_thickness
  expr: Constraints[20] = <<DisplaySS>>.photoresistor_height
  expr: Constraints[21] = <<DisplaySS>>.case_thickness
  sketch-geometry (8):
    g0: LineSegment StartX=319.55 StartY=98 StartZ=0 EndX=319.55 EndY=95 EndZ=0
    g1: LineSegment StartX=319.55 StartY=95 StartZ=0 EndX=316.55 EndY=95 EndZ=0
    g2: LineSegment StartX=316.55 StartY=95 StartZ=0 EndX=316.55 EndY=92.6 EndZ=0
    g3: LineSegment StartX=316.55 StartY=92.6 StartZ=0 EndX=314 EndY=92.6 EndZ=0
    g4: LineSegment StartX=314 StartY=92.6 StartZ=0 EndX=314 EndY=90.6 EndZ=0
    g5: LineSegment StartX=314 StartY=90.6 StartZ=0 EndX=321.55 EndY=90.6 EndZ=0
    g6: LineSegment StartX=321.55 StartY=90.6 StartZ=0 EndX=321.55 EndY=98 EndZ=0
    g7: LineSegment StartX=321.55 StartY=98 StartZ=0 EndX=319.55 EndY=98 EndZ=0
  constraints (24):
    c: Vertical(g0)
    c: Coincident(g0,g1)
    c: Horizontal(g1)
    c: Coincident(g1,g2)
    c: Vertical(g2)
    c: Coincident(g2,g3)
    c: Horizontal(g3)
    c: Coincident(g3,g4)
    c: Vertical(g4)
    c: Coincident(g4,g5)
    c: Horizontal(g5)
    c: Coincident(g5,g6)
    c: Vertical(g6)
    c: Coincident(g6,g7)
    c: Coincident(g7,g0)
    c: Distance(g3) = 2.55
    c: Distance(g1) = 3
    c: Distance(g0) = 3
    c: Distance(g7) = 2
    c: Angle(g7,g6) = 1.5708
    c: Distance(g2) = 2.4
    c: Distance(g4) = 2
    c: DistanceX(g3,g-3) = 0
    c: DistanceY(g0,g-3) = 0
FEATURE [Sketcher::SketchObject] Sketch020
  ArcFitTolerance = 1e-06
  AttachmentSupport = -> [DatumPlane011]
  ExternalGeometry = -> [DatumPoint]
  FullyConstrained = true
  MakeInternals = false
  MapMode = 5
  Placement = pos=(0,-28.05,6.2e-15) rot=(1,0,0;1.5708rad)
  expr: Constraints[15] = Sketch019.Constraints[15]
  expr: Constraints[16] = Sketch019.Constraints[16]
  expr: Constraints[17] = Sketch019.Constraints[17]
  expr: Constraints[18] = Sketch019.Constraints[18]
  expr: Constraints[19] = Sketch019.Constraints[19]
  expr: Constraints[20] = Sketch019.Constraints[20]
  expr: Constraints[21] = Sketch019.Constraints[21]
  expr: Constraints[22] = Sketch019.Constraints[22]
  expr: Constraints[23] = Sketch019.Constraints[23]
  sketch-geometry (8):
    g0: LineSegment StartX=319.55 StartY=98 StartZ=0 EndX=319.55 EndY=95 EndZ=0
    g1: LineSegment StartX=319.55 StartY=95 StartZ=0 EndX=316.55 EndY=95 EndZ=0
    g2: LineSegment StartX=316.55 StartY=95 StartZ=0 EndX=316.55 EndY=92.6 EndZ=0
    g3: LineSegment StartX=316.55 StartY=92.6 StartZ=0 EndX=314 EndY=92.6 EndZ=0
    g4: LineSegment StartX=314 StartY=92.6 StartZ=0 EndX=314 EndY=90.6 EndZ=0
    g5: LineSegment StartX=314 StartY=90.6 StartZ=0 EndX=321.55 EndY=90.6 EndZ=0
    g6: LineSegment StartX=321.55 StartY=90.6 StartZ=0 EndX=321.55 EndY=98 EndZ=0
    g7: LineSegment StartX=321.55 StartY=98 StartZ=0 EndX=319.55 EndY=98 EndZ=0
  constraints (24):
    c: Vertical(g0)
    c: Coincident(g0,g1)
    c: Horizontal(g1)
    c: Coincident(g1,g2)
    c: Vertical(g2)
    c: Coincident(g2,g3)
    c: Horizontal(g3)
    c: Coincident(g3,g4)
    c: Vertical(g4)
    c: Coincident(g4,g5)
    c: Horizontal(g5)
    c: Coincident(g5,g6)
    c: Vertical(g6)
    c: Coincident(g6,g7)
    c: Coincident(g7,g0)
    c: Distance(g3) = 2.55
    c: Distance(g1) = 3
    c: Distance(g0) = 3
    c: Distance(g7) = 2
    c: Angle(g7,g6) = 1.5708
    c: Distance(g2) = 2.4
    c: Distance(g4) = 2
    c: DistanceX(g3,g-3) = 0
    c: DistanceY(g0,g-3) = 0
FEATURE [PartDesign::Groove] Groove
  Angle = 360
  Angle2 = 60
  Axis = (0,0,1)
  Base = (314,-28.05,98)
  BaseFeature = -> Pocket
  Profile = -> Sketch019
  ReferenceAxis = -> DatumLine001
  Refine = true
  Suppressed = false
  Type = 0
FEATURE [PartDesign::Revolution] Revolution
  Angle = 360
  Angle2 = 60
  Axis = (0,0,1)
  Base = (314,-28.05,98)
  BaseFeature = -> Groove
  Profile = -> Sketch020
  ReferenceAxis = -> DatumLine001
  Refine = true
  Suppressed = false
  Type = 0
FEATURE [Sketcher::SketchObject] Sketch021
  ArcFitTolerance = 1e-06
  AttachmentSupport = -> [DatumPlane011]
  ExternalGeometry = -> [DatumPoint]
  FullyConstrained = true
  MakeInternals = false
  MapMode = 5
  Placement = pos=(0,-28.05,6.2e-15) rot=(1,0,0;1.5708rad)
  expr: Constraints[15] = <<DisplaySS>>.glass_thickness + <<DisplaySS>>.photoresistor_height
  expr: Constraints[8] = <<CalculatedSS>>.photoresistor_well_diameter
  expr: Constraints[9] = <<DisplaySS>>.case_thickness
  sketch-geometry (6):
    g0: LineSegment StartX=306.45 StartY=92.6 StartZ=0 EndX=306.45 EndY=90.6 EndZ=0
    g1: LineSegment StartX=306.45 StartY=90.6 StartZ=0 EndX=321.55 EndY=90.6 EndZ=0
    g2: LineSegment StartX=321.55 StartY=90.6 StartZ=0 EndX=321.55 EndY=92.6 EndZ=0
    g3: LineSegment StartX=321.55 StartY=92.6 StartZ=0 EndX=306.45 EndY=92.6 EndZ=0
    g4: LineSegment [constr] StartX=306.45 StartY=92.6 StartZ=0 EndX=314 EndY=98 EndZ=0
    g5: LineSegment [constr] StartX=321.55 StartY=92.6 StartZ=0 EndX=314 EndY=98 EndZ=0
  constraints (16):
    c: Coincident(g0,g1)
    c: Coincident(g1,g2)
    c: Coincident(g2,g3)
    c: Coincident(g3,g0)
    c: Vertical(g0)
    c: Vertical(g2)
    c: Horizontal(g1)
    c: Horizontal(g3)
    c: Distance(g3) = 15.1
    c: Distance(g0) = 2
    c: Coincident(g4,g0)
    c: Coincident(g4,g-3)
    c: Coincident(g5,g2)
    c: Coincident(g5,g4)
    c: Equal(g4,g5)
    c: Distance(g4,g3) = 5.4
FEATURE [PartDesign::Pocket] Pocket010
  BaseFeature = -> Revolution
  Direction = (0,1,-2e-16)
  Length = 1
  Length2 = 1
  Profile = -> Sketch021
  ReferenceAxis = -> Sketch021 [N_Axis]
  Refine = true
  Suppressed = false
  Type = 4
FEATURE [Sketcher::SketchObject] Sketch022
  ArcFitTolerance = 1e-06
  AttachmentSupport = -> [XZ_Plane007]
  FullyConstrained = true
  MakeInternals = false
  MapMode = 5
  Placement = pos=(0,0,0) rot=(1,0,0;1.5708rad)
  expr: Constraints[10] = <<CalculatedSS>>.back_plate_width
  expr: Constraints[91] = <<CalculatedSS>>.dht_vertical_offset
  expr: Constraints[92] = <<CalculatedSS>>.dht_horizontal_offset
  expr: Constraints[93] = <<DisplaySS>>.case_thickness + mount_bracket#<<DisplaySS>>.mount_bracket_face_size / 2
  expr: Constraints[94] = <<CalculatedSS>>.split_offset - <<CalculatedSS>>.mount_bracket_face_size / 2
  expr: Constraints[95] = <<DisplaySS>>.screw_diameter
  expr: Constraints[96] = <<CalculatedSS>>.split_offset - <<CalculatedSS>>.mount_bracket_face_size / 2
  expr: Constraints[97] = <<CalculatedSS>>.case_height - <<DisplaySS>>.case_thickness - <<mount_bracket>>#<<DisplaySS>>.mount_bracket_face_size / 2
  expr: Constraints[98] = <<DisplaySS>>.screw_diameter
  expr: Constraints[9] = <<CalculatedSS>>.back_plate_height
  sketch-geometry (35):
    g0: LineSegment StartX=0 StartY=98 StartZ=0 EndX=0 EndY=0 EndZ=0
    g1: LineSegment StartX=0 StartY=0 StartZ=0 EndX=349 EndY=0 EndZ=0
    g2: LineSegment StartX=349 StartY=0 StartZ=0 EndX=349 EndY=98 EndZ=0
    g3: LineSegment StartX=349 StartY=98 StartZ=0 EndX=0 EndY=98 EndZ=0
    g4: LineSegment StartX=69.8 StartY=57.6667 StartZ=0 EndX=69.8 EndY=32.6667 EndZ=0
    g5: LineSegment StartX=69.8 StartY=32.6667 StartZ=0 EndX=71.8 EndY=32.6667 EndZ=0
    g6: LineSegment StartX=71.8 StartY=32.6667 StartZ=0 EndX=71.8 EndY=57.6667 EndZ=0
    g7: LineSegment StartX=71.8 StartY=57.6667 StartZ=0 EndX=69.8 EndY=57.6667 EndZ=0
    g8: LineSegment StartX=73.8 StartY=57.6667 StartZ=0 EndX=73.8 EndY=32.6667 EndZ=0
    g9: LineSegment StartX=73.8 StartY=32.6667 StartZ=0 EndX=75.8 EndY=32.6667 EndZ=0
    g10: LineSegment StartX=75.8 StartY=32.6667 StartZ=0 EndX=75.8 EndY=57.6667 EndZ=0
    g11: LineSegment StartX=75.8 StartY=57.6667 StartZ=0 EndX=73.8 EndY=57.6667 EndZ=0
    g12: LineSegment StartX=77.8 StartY=57.6667 StartZ=0 EndX=77.8 EndY=32.6667 EndZ=0
    g13: LineSegment StartX=77.8 StartY=32.6667 StartZ=0 EndX=79.8 EndY=32.6667 EndZ=0
    g14: LineSegment StartX=79.8 StartY=32.6667 StartZ=0 EndX=79.8 EndY=57.6667 EndZ=0
    g15: LineSegment StartX=79.8 StartY=57.6667 StartZ=0 EndX=77.8 EndY=57.6667 EndZ=0
    g16: LineSegment StartX=81.8 StartY=57.6667 StartZ=0 EndX=81.8 EndY=32.6667 EndZ=0
    g17: LineSegment StartX=81.8 StartY=32.6667 StartZ=0 EndX=83.8 EndY=32.6667 EndZ=0
    g18: LineSegment StartX=83.8 StartY=32.6667 StartZ=0 EndX=83.8 EndY=57.6667 EndZ=0
    g19: LineSegment StartX=83.8 StartY=57.6667 StartZ=0 EndX=81.8 EndY=57.6667 EndZ=0
    g20: LineSegment StartX=85.8 StartY=57.6667 StartZ=0 EndX=85.8 EndY=32.6667 EndZ=0
    g21: LineSegment StartX=85.8 StartY=32.6667 StartZ=0 EndX=87.8 EndY=32.6667 EndZ=0
    g22: LineSegment StartX=87.8 StartY=32.6667 StartZ=0 EndX=87.8 EndY=57.6667 EndZ=0
    g23: LineSegment StartX=87.8 StartY=57.6667 StartZ=0 EndX=85.8 EndY=57.6667 EndZ=0
    g24: LineSegment StartX=89.8 StartY=57.6667 StartZ=0 EndX=89.8 EndY=32.6667 EndZ=0
    g25: LineSegment StartX=89.8 StartY=32.6667 StartZ=0 EndX=91.8 EndY=32.6667 EndZ=0
    g26: LineSegment StartX=91.8 StartY=32.6667 StartZ=0 EndX=91.8 EndY=57.6667 EndZ=0
    g27: LineSegment StartX=91.8 StartY=57.6667 StartZ=0 EndX=89.8 EndY=57.6667 EndZ=0
    g28: LineSegment [constr] StartX=71.8 StartY=57.6667 StartZ=0 EndX=73.8 EndY=57.6667 EndZ=0
    g29: LineSegment [constr] StartX=75.8 StartY=57.6667 StartZ=0 EndX=77.8 EndY=57.6667 EndZ=0
    g30: LineSegment [constr] StartX=79.8 StartY=57.6667 StartZ=0 EndX=81.8 EndY=57.6667 EndZ=0
    g31: LineSegment [constr] StartX=83.8 StartY=57.6667 StartZ=0 EndX=85.8 EndY=57.6667 EndZ=0
    g32: LineSegment [constr] StartX=87.8 StartY=57.6667 StartZ=0 EndX=89.8 EndY=57.6667 EndZ=0
    g33: Circle CenterX=246.75 CenterY=8.25 CenterZ=0 NormalX=0 NormalY=0 NormalZ=1 AngleXU=0 Radius=1
    g34: Circle CenterX=246.75 CenterY=89.75 CenterZ=0 NormalX=0 NormalY=0 NormalZ=1 AngleXU=0 Radius=1
  constraints (99):
    c: Coincident(g0,g1)
    c: Coincident(g1,g2)
    c: Coincident(g2,g3)
    c: Coincident(g3,g0)
    c: Vertical(g0)
    c: Vertical(g2)
    c: Horizontal(g1)
    c: Horizontal(g3)
    c: Coincident(g0,g-1)
    c: Distance(g0) = 98
    c: Distance(g1) = 349
    c: Coincident(g4,g5)
    c: Coincident(g5,g6)
    c: Coincident(g6,g7)
    c: Coincident(g7,g4)
    c: Vertical(g4)
    c: Vertical(g6)
    c: Horizontal(g5)
    c: Horizontal(g7)
    c: Distance(g6) = 25
    c: Distance(g7) = 2
    c: Coincident(g8,g9)
    c: Coincident(g12,g13)
    c: Coincident(g16,g17)
    c: Coincident(g20,g21)
    c: Coincident(g24,g25)
    c: Coincident(g9,g10)
    c: Coincident(g13,g14)
    c: Coincident(g17,g18)
    c: Coincident(g21,g22)
    c: Coincident(g25,g26)
    c: Coincident(g10,g11)
    c: Coincident(g14,g15)
    c: Coincident(g18,g19)
    c: Coincident(g22,g23)
    c: Coincident(g26,g27)
    c: Coincident(g11,g8)
    c: Coincident(g15,g12)
    c: Coincident(g19,g16)
    c: Coincident(g23,g20)
    c: Coincident(g27,g24)
    c: Vertical(g8)
    c: Vertical(g12)
    c: Vertical(g16)
    c: Vertical(g20)
    c: Vertical(g24)
    c: Vertical(g10)
    c: Vertical(g14)
    c: Vertical(g18)
    c: Vertical(g22)
    c: Vertical(g26)
    c: Horizontal(g9)
    c: Horizontal(g13)
    c: Horizontal(g17)
    c: Horizontal(g21)
    c: Horizontal(g25)
    c: Horizontal(g11)
    c: Horizontal(g15)
    c: Horizontal(g19)
    c: Horizontal(g23)
    c: Horizontal(g27)
    c: Coincident(g28,g6)
    c: Coincident(g28,g8)
    c: Horizontal(g28)
    c: Coincident(g29,g10)
    c: Coincident(g29,g12)
    c: Horizontal(g29)
    c: Coincident(g30,g14)
    c: Coincident(g30,g16)
    c: Horizontal(g30)
    c: Coincident(g31,g18)
    c: Coincident(g31,g20)
    c: Horizontal(g31)
    c: Coincident(g32,g22)
    c: Coincident(g32,g24)
    c: Horizontal(g32)
    c: DistanceX(g6,g8) = 2
    c: Equal(g11,g7)
    c: Equal(g7,g15)
    c: Equal(g15,g19)
    c: Equal(g19,g23)
    c: Equal(g23,g27)
    c: Equal(g29,g28)
    c: Equal(g28,g30)
    c: Equal(g30,g31)
    c: Equal(g31,g32)
    c: Horizontal(g4,g8)
    c: Horizontal(g8,g12)
    c: Horizontal(g12,g16)
    c: Horizontal(g16,g20)
    c: Horizontal(g20,g24)
    c: DistanceY(g-1,g4) = 32.6667
    c: DistanceX(g-1,g4) = 69.8
    c: DistanceY(g-1,g33) = 8.25
    c: DistanceX(g-2,g33) = 246.75
    c: Diameter(g33) = 2
    c: DistanceX(g-2,g34) = 246.75
    c: DistanceY(g-1,g34) = 89.75
    c: Diameter(g34) = 2
FEATURE [PartDesign::Pad] Pad007  label="BackPlatePad"
  Direction = (0,-1,2e-16)
  Length = 4
  Length2 = 10
  Placement = pos=(0,0,0) rot=(1,0,0;1.5708rad)
  Profile = -> Sketch022
  ReferenceAxis = -> Sketch022 [N_Axis]
  Refine = true
  Suppressed = false
  Type = 0
  expr: Length = <<DisplaySS>>.back_plate_thickness
FEATURE [Sketcher::SketchObject] Sketch023
  ArcFitTolerance = 1e-06
  AttachmentSupport = -> [XZ_Plane007]
  FullyConstrained = true
  MakeInternals = false
  MapMode = 5
  Placement = pos=(0,0,0) rot=(1,0,0;1.5708rad)
  expr: Constraints[0] = <<CalculatedSS>>.backplate_screw_offset_x
  expr: Constraints[1] = <<CalculatedSS>>.backplate_screw_offset_y
  expr: Constraints[2] = <<DisplaySS>>.screw_diameter
  sketch-geometry (1):
    g0: Circle CenterX=8.25 CenterY=8.25 CenterZ=0 NormalX=0 NormalY=0 NormalZ=1 AngleXU=0 Radius=1
  constraints (3):
    c: DistanceX(g-2,g0) = 8.25
    c: DistanceY(g-1,g0) = 8.25
    c: Diameter(g0) = 2
FEATURE [PartDesign::Plane] DatumPlane012
  AttachmentOffset = pos=(0,0,174.5) rot=(0,0,1;0rad)
  AttachmentSupport = -> [Pad007]
  Length = 138.684
  MapMode = 4
  Placement = pos=(174.5,0,-3.87e-14) rot=(0.707107,0,0.707107;3.14159rad)
  ResizeMode = 0
  Width = 65.6844
  expr: .AttachmentOffset.Base.z = <<CalculatedSS>>.back_plate_width / 2
FEATURE [PartDesign::Plane] DatumPlane013
  AttachmentOffset = pos=(0,0,-49) rot=(0,0,1;0rad)
  AttachmentSupport = -> [Pad007]
  Length = 401.35
  MapMode = 3
  Placement = pos=(0,0,49) rot=(1,0,0;3.14159rad)
  ResizeMode = 0
  Width = 77.3496
  expr: .AttachmentOffset.Base.z = <<CalculatedSS>>.back_plate_height / 2 * -1
FEATURE [App::Link] BackPlateBody  label="BackPlateBody001"
  LinkPlacement = pos=(349,4,98) rot=(0,1,0;3.14159rad)
  LinkedObject = -> Body006
  Placement = pos=(349,4,98) rot=(0,1,0;3.14159rad)
FEATURE [Part::Feature] Part__Feature  label="LDR"
  shape: bbox 5.1 x 4.3 x 7 mm, 52 faces (baked)
FEATURE [App::Link] LDR  label="LDR001"
  LinkPlacement = pos=(314,-28.05,92.6) rot=(0,0,1;0rad)
  LinkedObject = -> Part__Feature
  Placement = pos=(314,-28.05,92.6) rot=(0,0,1;0rad)
FEATURE [App::FeaturePython] Joint010  label="Fixed010"  # Assembly joint (typed FeaturePython)
  Activated = true
  AngleMax = 0
  AngleMin = 0
  Detach1 = false
  Detach2 = false
  Distance = 0
  Distance2 = 0
  EnableAngleMax = false
  EnableAngleMin = false
  EnableLengthMax = false
  EnableLengthMin = false
  JointType = 0 (Fixed)
  LengthMax = 0
  LengthMin = 0
  Placement2 = pos=(314,-28.05,92.6) rot=(0,0,1;0rad)
  Reference1 = -> Assembly [LDR.Edge6,LDR.Edge6]
  Reference2 = -> Assembly [Housing.Edge65,Housing.Edge65]
FEATURE [Sketcher::SketchObject] Sketch026
  ArcFitTolerance = 1e-06
  AttachmentSupport = -> [XZ_Plane007]
  ExternalGeometry = -> [Sketch022]
  FullyConstrained = true
  MakeInternals = false
  MapMode = 5
  Placement = pos=(0,0,0) rot=(1,0,0;1.5708rad)
  sketch-geometry (8):
    g0: LineSegment StartX=69.8 StartY=57.6667 StartZ=0 EndX=66.8 EndY=57.6667 EndZ=0
    g1: LineSegment StartX=66.8 StartY=57.6667 StartZ=0 EndX=66.8 EndY=32.6667 EndZ=0
    g2: LineSegment StartX=66.8 StartY=32.6667 StartZ=0 EndX=69.8 EndY=32.6667 EndZ=0
    g3: LineSegment StartX=69.8 StartY=32.6667 StartZ=0 EndX=69.8 EndY=57.6667 EndZ=0
    g4: LineSegment StartX=91.8 StartY=57.6667 StartZ=0 EndX=91.8 EndY=32.6667 EndZ=0
    g5: LineSegment StartX=91.8 StartY=32.6667 StartZ=0 EndX=94.8 EndY=32.6667 EndZ=0
    g6: LineSegment StartX=94.8 StartY=32.6667 StartZ=0 EndX=94.8 EndY=57.6667 EndZ=0
    g7: LineSegment StartX=94.8 StartY=57.6667 StartZ=0 EndX=91.8 EndY=57.6667 EndZ=0
  constraints (20):
    c: Coincident(g0,g1)
    c: Coincident(g1,g2)
    c: Coincident(g2,g3)
    c: Coincident(g3,g0)
    c: Horizontal(g0)
    c: Horizontal(g2)
    c: Vertical(g1)
    c: Coincident(g0,g-6)
    c: Coincident(g4,g5)
    c: Coincident(g5,g6)
    c: Coincident(g6,g7)
    c: Coincident(g7,g4)
    c: Vertical(g6)
    c: Horizontal(g5)
    c: Horizontal(g7)
    c: Coincident(g4,g-3)
    c: Coincident(g4,g-4)
    c: Coincident(g2,g-5)
    c: Distance(g2) = 3
    c: Equal(g2,g5)
FEATURE [PartDesign::Pad] Pad008
  BaseFeature = -> Pad007
  Direction = (0,-1,2e-16)
  Length = 11.7
  Length2 = 10
  Placement = pos=(0,0,0) rot=(1,0,0;1.5708rad)
  Profile = -> Sketch026
  ReferenceAxis = -> Sketch026 [N_Axis]
  Refine = true
  Suppressed = false
  Type = 0
  expr: Length = <<DisplaySS>>.back_plate_thickness + <<DisplaySS>>.dht_depth
FEATURE [App::DocumentObjectGroup] Measurements
FEATURE [PartDesign::Plane] DatumPlane015  label="BackPlateFace"
  AttachmentOffset = pos=(0,0,4) rot=(0,0,1;0rad)
  AttachmentSupport = -> [Pad008]
  Length = 416.896
  MapMode = 2
  Placement = pos=(0,-4,9e-16) rot=(1,0,0;1.5708rad)
  ResizeMode = 0
  Width = 165.896
  expr: .AttachmentOffset.Base.z = <<DisplaySS>>.back_plate_thickness
FEATURE [Sketcher::SketchObject] Sketch027  label="MountStudSketch"
  ArcFitTolerance = 1e-06
  AttachmentSupport = -> [DatumPlane015]
  ExternalGeometry = -> [Sketch026]
  FullyConstrained = true
  MakeInternals = false
  MapMode = 5
  Placement = pos=(0,-4,9e-16) rot=(1,0,0;1.5708rad)
  expr: Constraints[0] = <<mount_stud>>#<<MountStudSS>>.base_diameter
  expr: Constraints[6] = mount_stud#<<MountStudSS>>.base_diameter / 2
  sketch-geometry (4):
    g0: Circle CenterX=80.8 CenterY=23.3932 CenterZ=0 NormalX=0 NormalY=0 NormalZ=1 AngleXU=0 Radius=9.2735
    g1: LineSegment [constr] StartX=80.8 StartY=23.3932 StartZ=0 EndX=66.8 EndY=32.6667 EndZ=0
    g2: LineSegment [constr] StartX=80.8 StartY=23.3932 StartZ=0 EndX=94.8 EndY=32.6667 EndZ=0
    g3: LineSegment StartX=80.8 StartY=23.3932 StartZ=0 EndX=80.8 EndY=32.6667 EndZ=0
  constraints (10):
    c: Diameter(g0) = 18.547
    c: Coincident(g1,g0)
    c: Coincident(g1,g-3)
    c: Coincident(g2,g0)
    c: Coincident(g2,g-4)
    c: Equal(g2,g1)
    c: DistanceY(g0,g1) = 9.2735
    c: Coincident(g3,g0)
    c: PointOnObject(g3,g0)
    c: Vertical(g3)
FEATURE [App::Link] Mounting_Plate  label="Mounting Plate001"
  LinkPlacement = pos=(2,-62,2) rot=(0,0,1;0rad)
  LinkedObject = -> Body002
  Placement = pos=(2,-62,2) rot=(0,0,1;0rad)
FEATURE [App::FeaturePython] Joint012  label="Fixed012"  # Assembly joint (typed FeaturePython)
  Activated = true
  AngleMax = 0
  AngleMin = 0
  Detach1 = false
  Detach2 = false
  Distance = 0
  Distance2 = 0
  EnableAngleMax = false
  EnableAngleMin = false
  EnableLengthMax = false
  EnableLengthMin = false
  JointType = 0 (Fixed)
  LengthMax = 0
  LengthMin = 0
  Offset2 = pos=(0,0,0) rot=(0,0,1;1.5708rad)
  Placement1 = pos=(172.5,0,0) rot=(0.707107,0,0.707107;3.14159rad)
  Placement2 = pos=(174.5,-62,0) rot=(-0.57735,0.57735,0.57735;4.18879rad)
  Reference1 = -> Assembly [Mounting_Plate.Sketch006.Edge1,Mounting_Plate.Sketch006.Edge1]
  Reference2 = -> Assembly [Housing.Sketch028.Edge12,Housing.Sketch028.Edge12]
FEATURE [App::Link] Grid
  LinkPlacement = pos=(2,-67,2) rot=(0,0,1;0rad)
  LinkedObject = -> <external grid.FCStd>#Body001
  Placement = pos=(2,-67,2) rot=(0,0,1;0rad)
FEATURE [App::FeaturePython] Joint013  label="Fixed013"  # Assembly joint (typed FeaturePython)
  Activated = true
  AngleMax = 0
  AngleMin = 0
  Detach1 = false
  Detach2 = false
  Distance = 0
  Distance2 = 0
  EnableAngleMax = false
  EnableAngleMin = false
  EnableLengthMax = false
  EnableLengthMin = false
  JointType = 0 (Fixed)
  LengthMax = 0
  LengthMin = 0
  Offset2 = pos=(0,0,0) rot=(0,0,1;1.5708rad)
  Placement1 = pos=(172.5,0,0) rot=(0.707107,0,0.707107;3.14159rad)
  Placement2 = pos=(174.5,-67,0) rot=(-0.57735,0.57735,0.57735;4.18879rad)
  Reference1 = -> Assembly [Grid.Sketch002.Edge1,Grid.Sketch002.Edge1]
  Reference2 = -> Assembly [Housing.Sketch028.Edge4,Housing.Sketch028.Edge4]
FEATURE [App::FeaturePython] Joint014  label="Fixed014"  # Assembly joint (typed FeaturePython)
  Activated = true
  AngleMax = 0
  AngleMin = 0
  Detach1 = false
  Detach2 = false
  Distance = 0
  Distance2 = 0
  EnableAngleMax = false
  EnableAngleMin = false
  EnableLengthMax = false
  EnableLengthMin = false
  JointType = 0 (Fixed)
  LengthMax = 0
  LengthMin = 0
  Placement1 = pos=(174.5,-75,1.67e-14) rot=(0.707107,0,0.707107;3.14159rad)
  Placement2 = pos=(174.5,0,0) rot=(0.707107,0,0.707107;3.14159rad)
  Reference1 = -> Assembly [Housing.Edge7,Housing.Edge7]
  Reference2 = -> Assembly [Screen.Edge3,Screen.Edge3]
FEATURE [App::Link] Protoboard_Body  label="Protoboard Body"
  LinkPlacement = pos=(180.751,-4,79) rot=(0.57735,-0.57735,0.57735;4.18879rad)
  LinkedObject = -> <external Protoboard.FCStd>#Body007
  Placement = pos=(180.751,-4,79) rot=(0.57735,-0.57735,0.57735;4.18879rad)
FEATURE [App::Link] MountStud  label="MountStud001"
  LinkPlacement = pos=(8.25,6,167.65) rot=(1,0,0;1.5708rad)
  LinkedObject = -> <external mount_stud.FCStd>#Body
  Placement = pos=(8.25,6,167.65) rot=(1,0,0;1.5708rad)
FEATURE [App::FeaturePython] Joint016  label="Fixed016"  # Assembly joint (typed FeaturePython)
  Activated = true
  AngleMax = 0
  AngleMin = 0
  Detach1 = false
  Detach2 = false
  Distance = 0
  Distance2 = 0
  EnableAngleMax = false
  EnableAngleMin = false
  EnableLengthMax = false
  EnableLengthMin = false
  JointType = 0 (Fixed)
  LengthMax = 0
  LengthMin = 0
  Offset1 = pos=(0,10,0) rot=(1,0,0;1.5708rad)
  Placement1 = pos=(0,10,0) rot=(1,0,0;1.5708rad)
  Placement2 = pos=(8.25,167.65,0) rot=(0,0,1;0rad)
  Reference1 = -> Assembly [Assembly001.MountStud.Sketch.Vertex4,Assembly001.MountStud.Sketch.Vertex4]
  Reference2 = -> Assembly [Assembly001.Protoboard_Body.Sketch020.Vertex12,Assembly001.Protoboard_Body.Sketch020.Vertex12]
  expr: .Offset1.Base.y = <<mount_stud>>#<<MountStudSS>>.height
FEATURE [App::Link] MountStud001  label="MountStud002"
  LinkPlacement = pos=(101.851,-27.2012,35.15) rot=(0.707107,0,-0.707107;3.14159rad)
  LinkedObject = -> <external mount_stud.FCStd>#Body
  Placement = pos=(101.851,-27.2012,35.15) rot=(0.707107,0,-0.707107;3.14159rad)
FEATURE [App::FeaturePython] Joint017  label="Fixed017"  # Assembly joint (typed FeaturePython)
  Activated = true
  AngleMax = 0
  AngleMin = 0
  Detach1 = false
  Detach2 = false
  Distance = 0
  Distance2 = 0
  EnableAngleMax = false
  EnableAngleMin = false
  EnableLengthMax = false
  EnableLengthMin = false
  JointType = 0 (Fixed)
  LengthMax = 0
  LengthMin = 0
  Offset1 = pos=(0,0,-10) rot=(1,0,0;1.5708rad)
  Placement1 = pos=(43.85,167.65,-10) rot=(1,0,0;1.5708rad)
  Reference1 = -> Assembly [Assembly001.Protoboard_Body.Sketch020.Vertex11,Assembly001.Protoboard_Body.Sketch020.Vertex11]
  Reference2 = -> Assembly [Assembly001.MountStud001.Sketch.Vertex4,Assembly001.MountStud001.Sketch.Vertex4]
  expr: .Offset1.Base.z = -1 * <<mount_stud>>#<<MountStudSS>>.height
FEATURE [App::Link] MountStud002  label="MountStud003"
  LinkPlacement = pos=(101.851,-189.801,70.75) rot=(0.707107,0,-0.707107;3.14159rad)
  LinkedObject = -> <external mount_stud.FCStd>#Body
  Placement = pos=(101.851,-189.801,70.75) rot=(0.707107,0,-0.707107;3.14159rad)
FEATURE [App::FeaturePython] Joint018  label="Fixed018"  # Assembly joint (typed FeaturePython)
  Activated = true
  AngleMax = 0
  AngleMin = 0
  Detach1 = false
  Detach2 = false
  Distance = 0
  Distance2 = 0
  EnableAngleMax = false
  EnableAngleMin = false
  EnableLengthMax = false
  EnableLengthMin = false
  JointType = 0 (Fixed)
  LengthMax = 0
  LengthMin = 0
  Offset1 = pos=(0,0,-10) rot=(1,0,0;1.5708rad)
  Placement1 = pos=(8.25,5.05,-10) rot=(1,0,0;1.5708rad)
  Reference1 = -> Assembly [Assembly001.Protoboard_Body.Sketch020.Vertex9,Assembly001.Protoboard_Body.Sketch020.Vertex9]
  Reference2 = -> Assembly [Assembly001.MountStud002.Sketch.Vertex4,Assembly001.MountStud002.Sketch.Vertex4]
  expr: .Offset1.Base.z = <<mount_stud>>#<<MountStudSS>>.height * -1
FEATURE [App::Link] MountStud003  label="MountStud004"
  LinkPlacement = pos=(43.85,6,5.05) rot=(1,0,0;1.5708rad)
  LinkedObject = -> <external mount_stud.FCStd>#Body
  Placement = pos=(43.85,6,5.05) rot=(1,0,0;1.5708rad)
FEATURE [App::FeaturePython] Joint019  label="Fixed019"  # Assembly joint (typed FeaturePython)
  Activated = true
  AngleMax = 0
  AngleMin = 0
  Detach1 = false
  Detach2 = false
  Distance = 0
  Distance2 = 0
  EnableAngleMax = false
  EnableAngleMin = false
  EnableLengthMax = false
  EnableLengthMin = false
  JointType = 0 (Fixed)
  LengthMax = 0
  LengthMin = 0
  Offset1 = pos=(0,10,0) rot=(1,0,0;1.5708rad)
  Placement1 = pos=(0,10,0) rot=(1,0,0;1.5708rad)
  Placement2 = pos=(43.85,5.05,0) rot=(0,0,1;0rad)
  Reference1 = -> Assembly [Assembly001.MountStud003.Sketch.Vertex4,Assembly001.MountStud003.Sketch.Vertex4]
  Reference2 = -> Assembly [Assembly001.Protoboard_Body.Sketch020.Vertex10,Assembly001.Protoboard_Body.Sketch020.Vertex10]
  expr: .Offset1.Base.y = <<mount_stud>>#<<MountStudSS>>.height
FEATURE [Assembly::JointGroup] Joints001
  Group = -> [Joint016,Joint017,Joint018,Joint019]
FEATURE [Assembly::AssemblyObject] Assembly001  label="Protoboard Assembly"
  Group = -> [Joints001,Protoboard_Body,MountStud,Joint016,MountStud001,Joint017,MountStud002,Joint018,MountStud003,Joint019]
  Origin = -> Origin008
  Placement = pos=(50.9747,-83,-13.8512) rot=(-0.57735,-0.57735,-0.57735;2.0944rad)
  Type = Assembly
FEATURE [PartDesign::SubShapeBinder] Binder001
  BindCopyOnChange = 0
  BindMode = 0
  ClaimChildren = false
  Context = -> Body [Binder001.]
  Fuse = false
  MakeFace = true
  OffsetFill = false
  OffsetIntersection = false
  OffsetJoinType = 0
  OffsetOpenResult = false
  PartialLoad = false
  Placement = pos=(18.7235,-56.1,98) rot=(0.57735,0.57735,0.57735;2.0944rad)
  Refine = true
  Relative = true
  Support = -> [<external Protoboard.FCStd>#Body007[Sketch020.]]
  _Version = 2
  expr: .Placement.Base.x = <<CalculatedSS>>.mount_bracket_face_size + <<DisplaySS>>.case_thickness + <<CalculatedSS>>.protoboard_long_stud_clearance
  expr: .Placement.Base.y = (<<DisplaySS>>.back_plate_thickness + <<Protoboard>>#<<ProtoboardSS>>.total_width) * -1
  expr: .Placement.Base.z = <<CalculatedSS>>.case_height
FEATURE [Sketcher::SketchObject] Sketch029  label="MountBoardBracketSketch"
  ArcFitTolerance = 1e-06
  AttachmentSupport = -> [DatumPlane009]
  ExternalGeometry = -> [Binder001]
  FullyConstrained = true
  MakeInternals = false
  MapMode = 2
  Placement = pos=(0,0,98) rot=(0,0,1;0rad)
  expr: Constraints[1] = <<Protoboard>>#<<ProtoboardSS>>.mount_hole_diameter / 2
  expr: Constraints[2] = mount_stud#<<MountStudSS>>.base_diameter
  expr: Constraints[4] = <<Protoboard>>#<<ProtoboardSS>>.mount_hole_diameter / 2
  expr: Constraints[6] = <<Protoboard>>#<<ProtoboardSS>>.mount_hole_diameter / 2
  expr: Constraints[7] = <<Protoboard>>#<<ProtoboardSS>>.mount_hole_diameter / 2
  sketch-geometry (4):
    g0: Circle CenterX=186.374 CenterY=-12.25 CenterZ=0 NormalX=0 NormalY=0 NormalZ=1 AngleXU=0 Radius=9.2735
    g1: Circle CenterX=186.374 CenterY=-47.85 CenterZ=0 NormalX=0 NormalY=0 NormalZ=1 AngleXU=0 Radius=9.2735
    g2: Circle CenterX=23.7735 CenterY=-47.85 CenterZ=0 NormalX=0 NormalY=0 NormalZ=1 AngleXU=0 Radius=9.2735
    g3: Circle CenterX=23.7735 CenterY=-12.25 CenterZ=0 NormalX=0 NormalY=0 NormalZ=1 AngleXU=0 Radius=9.2735
  constraints (12):
    c: DistanceX(g-5,g0) = 0
    c: Distance(g0,g-5) = 1.1
    c: Diameter(g0) = 18.547
    c: DistanceX(g1,g-6) = 0
    c: Distance(g1,g-6) = 1.1
    c: Equal(g1,g0)
    c: Distance(g3,g-4) = 1.1
    c: Distance(g2,g-3) = 1.1
    c: DistanceX(g2,g-3) = 0
    c: DistanceX(g3,g-4) = 0
    c: Equal(g3,g2)
    c: Equal(g2,g0)
FEATURE [Sketcher::SketchObject] Sketch024
  ArcFitTolerance = 1e-06
  AttachmentSupport = -> [DatumPlane009]
  ExternalGeometry = -> [DatumPlane011,Sketch029]
  FullyConstrained = true
  MakeInternals = false
  MapMode = 5
  Placement = pos=(0,0,98) rot=(0,0,1;0rad)
  expr: Constraints[0] = <<button>>#<<ButtonSS>>.diameter
  expr: Constraints[6] = <<CalculatedSS>>.button_mount_offset + <<Protoboard>>#<<ProtoboardSS>>.pitch * 3
  sketch-geometry (3):
    g0: Circle CenterX=33.9935 CenterY=-30.05 CenterZ=0 NormalX=0 NormalY=0 NormalZ=1 AngleXU=0 Radius=10
    g1: LineSegment [constr] StartX=33.9935 StartY=-30.05 StartZ=0 EndX=23.7735 EndY=-12.25 EndZ=0
    g2: LineSegment [constr] StartX=33.9935 StartY=-30.05 StartZ=0 EndX=23.7735 EndY=-47.85 EndZ=0
  constraints (7):
    c: Diameter(g0) = 20
    c: Coincident(g1,g0)
    c: Coincident(g1,g-5)
    c: Coincident(g2,g0)
    c: Coincident(g2,g-4)
    c: Equal(g2,g1)
    c: DistanceX(g1,g0) = 10.22
FEATURE [PartDesign::Pocket] Pocket013
  BaseFeature = -> Pocket010
  Direction = (0,0,-1)
  Length = 2
  Length2 = 5
  Profile = -> Sketch024 [Edge1]
  ReferenceAxis = -> Sketch024 [N_Axis]
  Refine = true
  Suppressed = false
  Type = 0
  expr: Length = <<DisplaySS>>.case_thickness
FEATURE [PartDesign::LinearPattern] LinearPattern
  BaseFeature = -> Pocket013
  Direction = -> Sketch024 [H_Axis]
  Length = 55.88
  Mode = 0
  Occurrences = 3
  Offset = 27.94
  Originals = -> [Pocket013]
  Refine = true
  Suppressed = false
  TransformMode = 0
  expr: Length = <<DisplaySS>>.button_diameter * (<<DisplaySS>>.button_count - 1) + <<DisplaySS>>.button_spacing * (<<DisplaySS>>.button_count - 1)
  expr: Occurrences = <<DisplaySS>>.button_count
FEATURE [PartDesign::Plane] DatumPlane014  label="InsideBottomPlane"
  AttachmentOffset = pos=(0,0,2) rot=(0,0,1;0rad)
  AttachmentSupport = -> [LinearPattern]
  Length = 412.678
  MapMode = 2
  Placement = pos=(0,0,2) rot=(0,0,1;0rad)
  ResizeMode = 0
  Width = 138.678
  expr: .AttachmentOffset.Base.z = <<DisplaySS>>.case_thickness
FEATURE [Sketcher::SketchObject] Sketch028  label="InternalPanelAlignmentSketch"
  ArcFitTolerance = 1e-06
  AttachmentSupport = -> [DatumPlane014]
  FullyConstrained = true
  MakeInternals = false
  MapMode = 5
  Placement = pos=(0,0,2) rot=(0,0,1;0rad)
  expr: Constraints[115] = <<CalculatedSS>>.split_offset
  expr: Constraints[17] = <<CalculatedSS>>.case_clear_opening_width
  expr: Constraints[18] = <<DisplaySS>>.case_thickness
  expr: Constraints[19] = <<DisplaySS>>.grid_depth
  expr: Constraints[20] = <<CalculatedSS>>.mounting_plate_thickness
  expr: Constraints[21] = <<DisplaySS>>.case_depth * -1
  expr: Constraints[24] = <<CalculatedSS>>.mount_bracket_length
  expr: Constraints[25] = <<DisplaySS>>.case_thickness
  expr: Constraints[63] = <<CalculatedSS>>.mount_bracket_face_size
  sketch-geometry (42):
    g0: LineSegment StartX=2 StartY=-62 StartZ=0 EndX=2 EndY=-67 EndZ=0
    g1: LineSegment StartX=2 StartY=-67 StartZ=0 EndX=347 EndY=-67 EndZ=0
    g2: LineSegment StartX=347 StartY=-67 StartZ=0 EndX=347 EndY=-62 EndZ=0
    g3: LineSegment StartX=347 StartY=-62 StartZ=0 EndX=2 EndY=-62 EndZ=0
    g4: LineSegment StartX=2 StartY=-67 StartZ=0 EndX=2 EndY=-75 EndZ=0
    g5: LineSegment StartX=2 StartY=-75 StartZ=0 EndX=347 EndY=-75 EndZ=0
    g6: LineSegment StartX=347 StartY=-75 StartZ=0 EndX=347 EndY=-67 EndZ=0
    g7: LineSegment StartX=347 StartY=-67 StartZ=0 EndX=2 EndY=-67 EndZ=0
    g8: LineSegment StartX=2 StartY=0 StartZ=0 EndX=2 EndY=-21.8519 EndZ=0
    g9: LineSegment StartX=2 StartY=-21.8519 StartZ=0 EndX=14.5 EndY=-21.8519 EndZ=0
    g10: LineSegment StartX=14.5 StartY=-21.8519 StartZ=0 EndX=14.5 EndY=0 EndZ=0
    g11: LineSegment StartX=14.5 StartY=0 StartZ=0 EndX=2 EndY=0 EndZ=0
    g12: LineSegment StartX=2 StartY=-62 StartZ=0 EndX=14.5 EndY=-62 EndZ=0
    g13: LineSegment StartX=347 StartY=-62 StartZ=0 EndX=347 EndY=-40.1481 EndZ=0
    g14: LineSegment StartX=347 StartY=-40.1481 StartZ=0 EndX=334.5 EndY=-40.1481 EndZ=0
    g15: LineSegment StartX=334.5 StartY=-40.1481 StartZ=0 EndX=334.5 EndY=-62 EndZ=0
    g16: LineSegment StartX=334.5 StartY=-62 StartZ=0 EndX=347 EndY=-62 EndZ=0
    g17: LineSegment StartX=347 StartY=0 StartZ=0 EndX=334.5 EndY=0 EndZ=0
    g18: LineSegment StartX=334.5 StartY=0 StartZ=0 EndX=334.5 EndY=-21.8519 EndZ=0
    g19: LineSegment StartX=334.5 StartY=-21.8519 StartZ=0 EndX=347 EndY=-21.8519 EndZ=0
    g20: LineSegment StartX=347 StartY=-21.8519 StartZ=0 EndX=347 EndY=0 EndZ=0
    g21: LineSegment [constr] StartX=347 StartY=-75 StartZ=0 EndX=347 EndY=0 EndZ=0
    g22: LineSegment StartX=2 StartY=-62 StartZ=0 EndX=14.5 EndY=-62 EndZ=0
    g23: LineSegment StartX=14.5 StartY=-62 StartZ=0 EndX=14.5 EndY=-40.1481 EndZ=0
    g24: LineSegment StartX=14.5 StartY=-40.1481 StartZ=0 EndX=2 EndY=-40.1481 EndZ=0
    g25: LineSegment StartX=2 StartY=-40.1481 StartZ=0 EndX=2 EndY=-62 EndZ=0
    g26: LineSegment StartX=231.148 StartY=-49.5 StartZ=0 EndX=231.148 EndY=-62 EndZ=0
    g27: LineSegment StartX=231.148 StartY=-62 StartZ=0 EndX=253 EndY=-62 EndZ=0
    g28: LineSegment StartX=253 StartY=-62 StartZ=0 EndX=253 EndY=-49.5 EndZ=0
    g29: LineSegment StartX=253 StartY=-49.5 StartZ=0 EndX=231.148 EndY=-49.5 EndZ=0
    g30: LineSegment StartX=253 StartY=-49.5 StartZ=0 EndX=253 EndY=-62 EndZ=0
    g31: LineSegment StartX=253 StartY=-62 StartZ=0 EndX=274.852 EndY=-62 EndZ=0
    g32: LineSegment StartX=274.852 StartY=-62 StartZ=0 EndX=274.852 EndY=-49.5 EndZ=0
    g33: LineSegment StartX=274.852 StartY=-49.5 StartZ=0 EndX=253 EndY=-49.5 EndZ=0
    g34: LineSegment StartX=253 StartY=0 StartZ=0 EndX=231.148 EndY=0 EndZ=0
    g35: LineSegment StartX=231.148 StartY=0 StartZ=0 EndX=231.148 EndY=-12.5 EndZ=0
    g36: LineSegment StartX=231.148 StartY=-12.5 StartZ=0 EndX=253 EndY=-12.5 EndZ=0
    g37: LineSegment StartX=253 StartY=-12.5 StartZ=0 EndX=253 EndY=0 EndZ=0
    g38: LineSegment StartX=253 StartY=0 StartZ=0 EndX=253 EndY=-12.5 EndZ=0
    g39: LineSegment StartX=253 StartY=-12.5 StartZ=0 EndX=274.852 EndY=-12.5 EndZ=0
    g40: LineSegment StartX=274.852 StartY=-12.5 StartZ=0 EndX=274.852 EndY=0 EndZ=0
    g41: LineSegment StartX=274.852 StartY=0 StartZ=0 EndX=253 EndY=0 EndZ=0
  constraints (118):
    c: Coincident(g0,g1)
    c: Coincident(g1,g2)
    c: Coincident(g2,g3)
    c: Coincident(g3,g0)
    c: Vertical(g0)
    c: Vertical(g2)
    c: Horizontal(g1)
    c: Horizontal(g3)
    c: Coincident(g4,g5)
    c: Coincident(g5,g6)
    c: Coincident(g6,g7)
    c: Coincident(g7,g4)
    c: Vertical(g4)
    c: Vertical(g6)
    c: Horizontal(g5)
    c: Coincident(g4,g0)
    c: Coincident(g6,g1)
    c: Distance(g1) = 345
    c: DistanceX(g-2,g0) = 2
    c: Distance(g4) = 8
    c: Distance(g0) = 5
    c: DistanceY(g-1,g4) = -75
    c: Horizontal(g11)
    c: DistanceY(g-1,g8) = 0
    c: Distance(g10) = 21.8519
    c: DistanceX(g-2,g8) = 2
    c: Horizontal(g12)
    c: Coincident(g13,g14)
    c: Coincident(g14,g15)
    c: Coincident(g15,g16)
    c: Coincident(g16,g13)
    c: Vertical(g13)
    c: Vertical(g15)
    c: Horizontal(g14)
    c: Horizontal(g16)
    c: Coincident(g13,g2)
    c: Coincident(g17,g18)
    c: Coincident(g18,g19)
    c: Coincident(g19,g20)
    c: Coincident(g20,g17)
    c: Horizontal(g17)
    c: Horizontal(g19)
    c: Vertical(g18)
    c: Vertical(g20)
    c: PointOnObject(g17,g-1)
    c: Equal(g18,g15)
    c: Equal(g15,g10)
    c: Equal(g17,g14)
    c: Equal(g14,g11)
    c: Coincident(g21,g5)
    c: Vertical(g21)
    c: Coincident(g21,g17)
    c: Coincident(g22,g23)
    c: Coincident(g23,g24)
    c: Coincident(g24,g25)
    c: Coincident(g25,g22)
    c: Horizontal(g24)
    c: Vertical(g23)
    c: Vertical(g25)
    c: Coincident(g22,g12)
    c: DistanceX(g23,g9) = 0
    c: Equal(g25,g8)
    c: Coincident(g0,g12)
    c: Distance(g9) = 12.5
    c: Coincident(g8,g9)
    c: Coincident(g9,g10)
    c: Angle(g9,g8) = 1.5708
    c: Coincident(g10,g11)
    c: Coincident(g11,g8)
    c: Angle(g11,g10) = 1.5708
    c: Equal(g11,g9)
    c: Coincident(g12,g22)
    c: Coincident(g26,g27)
    c: Coincident(g27,g28)
    c: Coincident(g28,g29)
    c: Coincident(g29,g26)
    c: Vertical(g26)
    c: Vertical(g28)
    c: Horizontal(g27)
    c: Horizontal(g29)
    c: PointOnObject(g27,g3)
    c: Coincident(g30,g31)
    c: Coincident(g31,g32)
    c: Coincident(g32,g33)
    c: Coincident(g33,g30)
    c: Vertical(g30)
    c: Vertical(g32)
    c: Horizontal(g31)
    c: Horizontal(g33)
    c: PointOnObject(g31,g3)
    c: PointOnObject(g34,g-1)
    c: Equal(g32,g24)
    c: Equal(g29,g23)
    c: Equal(g33,g29)
    c: Coincident(g34,g35)
    c: Coincident(g35,g36)
    c: Coincident(g36,g37)
    c: Coincident(g37,g34)
    c: Horizontal(g34)
    c: Horizontal(g36)
    c: Vertical(g35)
    c: Vertical(g37)
    c: Coincident(g38,g39)
    c: Coincident(g39,g40)
    c: Coincident(g40,g41)
    c: Coincident(g41,g38)
    c: Vertical(g38)
    c: Vertical(g40)
    c: Horizontal(g39)
    c: Horizontal(g41)
    c: Vertical(g39,g32)
    c: Vertical(g35,g26)
    c: Equal(g35,g26)
    c: Equal(g40,g32)
    c: Coincident(g28,g30)
    c: DistanceX(g-2,g28) = 253
    c: Coincident(g38,g36)
    c: Equal(g36,g29)
FEATURE [App::Link] MountStud004  label="MountStud005"
  LinkPlacement = pos=(23.7735,-47.85,96) rot=(1,0,0;3.14159rad)
  LinkedObject = -> <external mount_stud.FCStd>#Body
  Placement = pos=(23.7735,-47.85,96) rot=(1,0,0;3.14159rad)
FEATURE [App::Link] MountStud005  label="MountStud006"
  LinkPlacement = pos=(23.7735,-12.25,96) rot=(1,0,0;3.14159rad)
  LinkedObject = -> <external mount_stud.FCStd>#Body
  Placement = pos=(23.7735,-12.25,96) rot=(1,0,0;3.14159rad)
FEATURE [App::Link] MountStud006  label="MountStud007"
  LinkPlacement = pos=(186.374,-47.85,96) rot=(1,0,0;3.14159rad)
  LinkedObject = -> <external mount_stud.FCStd>#Body
  Placement = pos=(186.374,-47.85,96) rot=(1,0,0;3.14159rad)
FEATURE [App::Link] MountStud007  label="MountStud008"
  LinkPlacement = pos=(186.374,-12.25,96) rot=(1,0,0;3.14159rad)
  LinkedObject = -> <external mount_stud.FCStd>#Body
  Placement = pos=(186.374,-12.25,96) rot=(1,0,0;3.14159rad)
FEATURE [App::Link] Button_Body  label="Button Body"
  LinkPlacement = pos=(33.9935,-30.05,90) rot=(1,0,0;1.5708rad)
  LinkedObject = -> <external button.FCStd>#Body006
  Placement = pos=(33.9935,-30.05,90) rot=(1,0,0;1.5708rad)
FEATURE [App::FeaturePython] Joint025  label="Fixed025"  # Assembly joint (typed FeaturePython)
  Activated = true
  AngleMax = 0
  AngleMin = 0
  Detach1 = false
  Detach2 = false
  Distance = 0
  Distance2 = 0
  EnableAngleMax = false
  EnableAngleMin = false
  EnableLengthMax = false
  EnableLengthMin = false
  JointType = 0 (Fixed)
  LengthMax = 0
  LengthMin = 0
  Placement1 = pos=(0,8,3.6e-15) rot=(1,0,0;1.5708rad)
  Placement2 = pos=(33.9935,-30.05,98) rot=(0,0,1;0rad)
  Reference1 = -> Assembly [Button_Body.Edge1,Button_Body.Edge1]
  Reference2 = -> Assembly [Housing.Edge15,Housing.Edge15]
FEATURE [App::Link] Button_Body001  label="Button Body001"
  LinkPlacement = pos=(89.8735,-30.05,90) rot=(1,0,0;1.5708rad)
  LinkedObject = -> <external button.FCStd>#Body006
  Placement = pos=(89.8735,-30.05,90) rot=(1,0,0;1.5708rad)
FEATURE [App::Link] Button_Body002  label="Button Body002"
  LinkPlacement = pos=(61.9335,-30.05,90) rot=(1,0,0;1.5708rad)
  LinkedObject = -> <external button.FCStd>#Body006
  Placement = pos=(61.9335,-30.05,90) rot=(1,0,0;1.5708rad)
FEATURE [App::FeaturePython] Joint026  label="Fixed026"  # Assembly joint (typed FeaturePython)
  Activated = true
  AngleMax = 0
  AngleMin = 0
  Detach1 = false
  Detach2 = false
  Distance = 0
  Distance2 = 0
  EnableAngleMax = false
  EnableAngleMin = false
  EnableLengthMax = false
  EnableLengthMin = false
  JointType = 0 (Fixed)
  LengthMax = 0
  LengthMin = 0
  Placement1 = pos=(0,8,3.6e-15) rot=(1,0,0;1.5708rad)
  Placement2 = pos=(61.9335,-30.05,98) rot=(0,0,1;0rad)
  Reference1 = -> Assembly [Button_Body002.Edge1,Button_Body002.Edge1]
  Reference2 = -> Assembly [Housing.Edge16,Housing.Edge16]
FEATURE [App::FeaturePython] Joint027  label="Fixed027"  # Assembly joint (typed FeaturePython)
  Activated = true
  AngleMax = 0
  AngleMin = 0
  Detach1 = false
  Detach2 = false
  Distance = 0
  Distance2 = 0
  EnableAngleMax = false
  EnableAngleMin = false
  EnableLengthMax = false
  EnableLengthMin = false
  JointType = 0 (Fixed)
  LengthMax = 0
  LengthMin = 0
  Placement1 = pos=(0,8,3.6e-15) rot=(1,0,0;1.5708rad)
  Placement2 = pos=(89.8735,-30.05,98) rot=(0,0,1;0rad)
  Reference1 = -> Assembly [Button_Body001.Edge1,Button_Body001.Edge1]
  Reference2 = -> Assembly [Housing.Edge17,Housing.Edge17]
FEATURE [App::DocumentObjectGroup] Group003  label="Buttons"
  Group = -> [Button_Body002,Button_Body001,Button_Body]
FEATURE [App::DocumentObjectGroup] Group004  label="ProtoboardMountStuds"
  Group = -> [MountStud005,MountStud006,MountStud004,MountStud007]
FEATURE [App::Link] MountBracket002  label="MountBracket003"
  LinkPlacement = pos=(2,-62,96) rot=(1,0,0;3.14159rad)
  LinkedObject = -> <external mount_bracket.FCStd>#Body003
  Placement = pos=(2,-62,96) rot=(1,0,0;3.14159rad)
FEATURE [App::Link] MountBracket004  label="MountBracket005"
  LinkPlacement = pos=(9235.91,7769.34,228) rot=(0.926735,0.375715,0;3.14159rad)
  LinkedObject = -> <external mount_bracket.FCStd>#Body003
  Placement = pos=(9235.91,7769.34,228) rot=(0.926735,0.375715,0;3.14159rad)
FEATURE [App::FeaturePython] Joint032  label="Fixed032"  # Assembly joint (typed FeaturePython)
  Activated = true
  AngleMax = 0
  AngleMin = 0
  Detach1 = false
  Detach2 = false
  Distance = 0
  Distance2 = 0
  EnableAngleMax = false
  EnableAngleMin = false
  EnableLengthMax = false
  EnableLengthMin = false
  JointType = 0 (Fixed)
  LengthMax = 0
  LengthMin = 0
  Offset1 = pos=(94,0,0) rot=(0,0,1;0rad)
  Placement1 = pos=(-11806.3,-615.014,226) rot=(-0.929358,-0.369179,0;3.14159rad)
  Placement2 = pos=(334.5,-10.9259,0) rot=(-0.57735,-0.57735,0.57735;4.18879rad)
  Reference1 = -> Assembly [MountBracket004.?Edge4,MountBracket004.?Edge4]
  Reference2 = -> Assembly [Housing.Sketch028.Edge23,Housing.Sketch028.Edge23]
  expr: .Offset1.Base.x = <<CalculatedSS>>.case_clear_opening_height
FEATURE [App::Link] MountBracket006  label="MountBracket007"
  LinkPlacement = pos=(14724.7,-12629.1,134) rot=(0,0,1;0.349488rad)
  LinkedObject = -> <external mount_bracket.FCStd>#Body003
  Placement = pos=(14724.7,-12629.1,134) rot=(0,0,1;0.349488rad)
FEATURE [App::FeaturePython] Joint033  label="Fixed033"  # Assembly joint (typed FeaturePython)
  Activated = true
  AngleMax = 0
  AngleMin = 0
  Detach1 = false
  Detach2 = false
  Distance = 0
  Distance2 = 0
  EnableAngleMax = false
  EnableAngleMin = false
  EnableLengthMax = false
  EnableLengthMin = false
  JointType = 0 (Fixed)
  LengthMax = 0
  LengthMin = 0
  Offset1 = pos=(0,0,0) rot=(0,0,1;3.14159rad)
  Placement1 = pos=(-9213.31,16745.1,-132) rot=(0,0,1;2.7826rad)
  Placement2 = pos=(334.5,-51.0741,0) rot=(-0.57735,-0.57735,0.57735;4.18879rad)
  Reference1 = -> Assembly [MountBracket006.?Edge4,MountBracket006.?Edge4]
  Reference2 = -> Assembly [Housing.Sketch028.Edge10,Housing.Sketch028.Edge10]
FEATURE [App::Link] MountBracket007  label="MountBracket008"
  LinkPlacement = pos=(8531.12,7102.72,228) rot=(0.830359,-0.557229,0;3.14159rad)
  LinkedObject = -> <external mount_bracket.FCStd>#Body003
  Placement = pos=(8531.12,7102.72,228) rot=(0.830359,-0.557229,0;3.14159rad)
FEATURE [App::DocumentObjectGroup] Group  label="Mount Bracket"
  Group = -> [MountBracket002,MountBracket004,MountBracket006,MountBracket007]
FEATURE [App::FeaturePython] Joint034  label="Fixed034"  # Assembly joint (typed FeaturePython)
  Activated = true
  AngleMax = 0
  AngleMin = 0
  Detach1 = false
  Detach2 = false
  Distance = 0
  Distance2 = 0
  EnableAngleMax = false
  EnableAngleMin = false
  EnableLengthMax = false
  EnableLengthMin = false
  JointType = 0 (Fixed)
  LengthMax = 0
  LengthMin = 0
  Offset1 = pos=(94,0,0) rot=(0,0,1;3.14159rad)
  Placement1 = pos=(3518.41,10284.8,226) rot=(0.565033,0.825068,0;3.14159rad)
  Placement2 = pos=(347,-51.0741,0) rot=(0.57735,0.57735,0.57735;4.18879rad)
  Reference1 = -> Assembly [MountBracket007.?Edge4,MountBracket007.?Edge4]
  Reference2 = -> Assembly [Housing.Sketch028.Edge8,Housing.Sketch028.Edge8]
  expr: .Offset1.Base.x = <<CalculatedSS>>.case_clear_opening_height
FEATURE [App::FeaturePython] Joint035  label="Fixed035"  # Assembly joint (typed FeaturePython)
  Activated = true
  AngleMax = 0
  AngleMin = 0
  Detach1 = false
  Detach2 = false
  Distance = 0
  Distance2 = 0
  EnableAngleMax = false
  EnableAngleMin = false
  EnableLengthMax = false
  EnableLengthMin = false
  JointType = 0 (Fixed)
  LengthMax = 0
  LengthMin = 0
  Offset2 = pos=(0,0,0) rot=(0,0,-1;1.5708rad)
  Placement1 = pos=(174.5,-4,98) rot=(-0.707107,0,0.707107;3.14159rad)
  Placement2 = pos=(174.5,0,0) rot=(0.57735,0.57735,0.57735;2.0944rad)
  Reference1 = -> Assembly [BackPlateBody.Edge7,BackPlateBody.Edge7]
  Reference2 = -> Assembly [Housing.Sketch.Edge1,Housing.Sketch.Edge1]
FEATURE [PartDesign::Mirrored] Mirrored
  MirrorPlane = -> DatumPlane013
  Placement = pos=(0,0,0) rot=(1,0,0;1.5708rad)
  Refine = true
  Suppressed = false
  TransformMode = 0
FEATURE [PartDesign::Mirrored] Mirrored006
  MirrorPlane = -> DatumPlane012
  Placement = pos=(0,0,0) rot=(1,0,0;1.5708rad)
  Refine = true
  Suppressed = false
  TransformMode = 0
FEATURE [PartDesign::Pocket] Pocket014
  BaseFeature = -> Pad008
  Direction = (0,1,-2e-16)
  Length = 4
  Length2 = 5
  Placement = pos=(0,0,0) rot=(1,0,0;1.5708rad)
  Profile = -> Sketch023
  ReferenceAxis = -> Sketch023 [N_Axis]
  Refine = true
  Reversed = true
  Suppressed = false
  Type = 0
  expr: Length = <<DisplaySS>>.back_plate_thickness
FEATURE [PartDesign::MultiTransform] MultiTransform
  BaseFeature = -> Pocket014
  Originals = -> [Pocket014]
  Placement = pos=(0,0,0) rot=(1,0,0;1.5708rad)
  Refine = true
  Suppressed = false
  TransformMode = 0
  Transformations = -> [Mirrored,Mirrored006]
FEATURE [Sketcher::SketchObject] Sketch031  label="Mounting Stud Sketch"
  ArcFitTolerance = 1e-06
  AttachmentSupport = -> [DatumPlane009]
  ExternalGeometry = -> [Binder001]
  FullyConstrained = true
  MakeInternals = false
  MapMode = 5
  Placement = pos=(0,0,98) rot=(0,0,1;0rad)
  expr: Constraints[9] = mount_stud#<<MountStudSS>>.base_diameter / 2
  sketch-geometry (4):
    g0: LineSegment StartX=23.7735 StartY=-12.25 StartZ=0 EndX=33.047 EndY=-12.25 EndZ=0
    g1: LineSegment StartX=23.7735 StartY=-47.85 StartZ=0 EndX=33.047 EndY=-47.85 EndZ=0
    g2: LineSegment StartX=186.374 StartY=-12.25 StartZ=0 EndX=195.647 EndY=-12.25 EndZ=0
    g3: LineSegment StartX=186.374 StartY=-47.85 StartZ=0 EndX=195.647 EndY=-47.85 EndZ=0
  constraints (12):
    c: Coincident(g0,g-7)
    c: Horizontal(g0)
    c: Coincident(g1,g-5)
    c: Coincident(g2,g-3)
    c: Coincident(g3,g-4)
    c: Horizontal(g3)
    c: Equal(g3,g2)
    c: Equal(g2,g1)
    c: Equal(g1,g0)
    c: Distance(g0) = 9.2735
    c: Parallel(g1,g0)
    c: Parallel(g0,g2)
FEATURE [App::FeaturePython] Joint036  label="Fixed036"  # Assembly joint (typed FeaturePython)
  Activated = true
  AngleMax = 0
  AngleMin = 0
  Detach1 = false
  Detach2 = false
  Distance = 0
  Distance2 = 0
  EnableAngleMax = false
  EnableAngleMin = false
  EnableLengthMax = false
  EnableLengthMin = false
  JointType = 0 (Fixed)
  LengthMax = 0
  LengthMin = 0
  Offset1 = pos=(0,2,0) rot=(0,0,1;0rad)
  Offset2 = pos=(0,0,0) rot=(0,0,-1;1.5708rad)
  Placement1 = pos=(4.63675,-2,0) rot=(0.707107,0,0.707107;3.14159rad)
  Placement2 = pos=(191.01,-12.25,0) rot=(0.57735,0.57735,0.57735;2.0944rad)
  Reference1 = -> Assembly [MountStud007.Sketch.Edge4,MountStud007.Sketch.Edge4]
  Reference2 = -> Assembly [Housing.Sketch031.Edge3,Housing.Sketch031.Edge3]
  expr: .Offset1.Base.y = <<DisplaySS>>.case_thickness
FEATURE [App::FeaturePython] Joint037  label="Fixed037"  # Assembly joint (typed FeaturePython)
  Activated = true
  AngleMax = 0
  AngleMin = 0
  Detach1 = false
  Detach2 = false
  Distance = 0
  Distance2 = 0
  EnableAngleMax = false
  EnableAngleMin = false
  EnableLengthMax = false
  EnableLengthMin = false
  JointType = 0 (Fixed)
  LengthMax = 0
  LengthMin = 0
  Offset1 = pos=(0,2,0) rot=(0,0,1;0rad)
  Offset2 = pos=(0,0,0) rot=(0,0,-1;1.5708rad)
  Placement1 = pos=(4.63675,-2,0) rot=(0.707107,0,0.707107;3.14159rad)
  Placement2 = pos=(191.01,-47.85,0) rot=(0.57735,0.57735,0.57735;2.0944rad)
  Reference1 = -> Assembly [MountStud006.Sketch.Edge4,MountStud006.Sketch.Edge4]
  Reference2 = -> Assembly [Housing.Sketch031.Edge4,Housing.Sketch031.Edge4]
  expr: .Offset1.Base.y = <<DisplaySS>>.case_thickness
FEATURE [App::FeaturePython] Joint038  label="Fixed038"  # Assembly joint (typed FeaturePython)
  Activated = true
  AngleMax = 0
  AngleMin = 0
  Detach1 = false
  Detach2 = false
  Distance = 0
  Distance2 = 0
  EnableAngleMax = false
  EnableAngleMin = false
  EnableLengthMax = false
  EnableLengthMin = false
  JointType = 0 (Fixed)
  LengthMax = 0
  LengthMin = 0
  Offset1 = pos=(0,2,0) rot=(0,0,1;0rad)
  Offset2 = pos=(0,0,0) rot=(0,0,-1;1.5708rad)
  Placement1 = pos=(4.63675,-2,0) rot=(0.707107,0,0.707107;3.14159rad)
  Placement2 = pos=(28.4103,-12.25,0) rot=(0.57735,0.57735,0.57735;2.0944rad)
  Reference1 = -> Assembly [MountStud005.Sketch.Edge4,MountStud005.Sketch.Edge4]
  Reference2 = -> Assembly [Housing.Sketch031.Edge1,Housing.Sketch031.Edge1]
  expr: .Offset1.Base.y = <<DisplaySS>>.case_thickness
FEATURE [App::FeaturePython] Joint039  label="Fixed039"  # Assembly joint (typed FeaturePython)
  Activated = true
  AngleMax = 0
  AngleMin = 0
  Detach1 = false
  Detach2 = false
  Distance = 0
  Distance2 = 0
  EnableAngleMax = false
  EnableAngleMin = false
  EnableLengthMax = false
  EnableLengthMin = false
  JointType = 0 (Fixed)
  LengthMax = 0
  LengthMin = 0
  Offset1 = pos=(0,2,0) rot=(0,0,1;0rad)
  Offset2 = pos=(0,0,0) rot=(0,0,-1;1.5708rad)
  Placement1 = pos=(4.63675,-2,0) rot=(0.707107,0,0.707107;3.14159rad)
  Placement2 = pos=(28.4103,-47.85,0) rot=(0.57735,0.57735,0.57735;2.0944rad)
  Reference1 = -> Assembly [MountStud004.Sketch.Edge4,MountStud004.Sketch.Edge4]
  Reference2 = -> Assembly [Housing.Sketch031.Edge2,Housing.Sketch031.Edge2]
  expr: .Offset1.Base.y = <<DisplaySS>>.case_thickness
FEATURE [App::Link] MountStud008  label="MountStud"
  LinkPlacement = pos=(268.2,-1.57e-14,74.6068) rot=(-0.57735,-0.57735,0.57735;4.18879rad)
  LinkedObject = -> <external mount_stud.FCStd>#Body
  Placement = pos=(268.2,-1.57e-14,74.6068) rot=(-0.57735,-0.57735,0.57735;4.18879rad)
FEATURE [App::FeaturePython] Joint040  label="Fixed040"  # Assembly joint (typed FeaturePython)
  Activated = true
  AngleMax = 0
  AngleMin = 0
  Detach1 = false
  Detach2 = false
  Distance = 0
  Distance2 = 0
  EnableAngleMax = false
  EnableAngleMin = false
  EnableLengthMax = false
  EnableLengthMin = false
  JointType = 0 (Fixed)
  LengthMax = 0
  LengthMin = 0
  Offset2 = pos=(0,0,0) rot=(0,0,1;1.5708rad)
  Placement1 = pos=(4.63675,0,0) rot=(0.707107,0,0.707107;3.14159rad)
  Placement2 = pos=(80.8,28.0299,0) rot=(1,0,0;4.71239rad)
  Reference1 = -> Assembly [MountStud008.Sketch.Edge4,MountStud008.Sketch.Edge4]
  Reference2 = -> Assembly [BackPlateBody.Sketch027.Edge2,BackPlateBody.Sketch027.Edge2]
FEATURE [PartDesign::SubShapeBinder] Binder002  label="grid_screw_binder"
  BindCopyOnChange = 0
  BindMode = 0
  ClaimChildren = false
  Context = -> Body [Binder002.]
  Fuse = false
  MakeFace = true
  OffsetFill = false
  OffsetIntersection = false
  OffsetJoinType = 0
  OffsetOpenResult = false
  PartialLoad = false
  Placement = pos=(2,-67,98) rot=(0,0,1;0rad)
  Refine = true
  Relative = true
  Support = -> [<external grid.FCStd>#Body001[Sketch.]]
  _Version = 2
  expr: .Placement.Base.x = <<DisplaySS>>.case_thickness
  expr: .Placement.Base.y = (<<DisplaySS>>.case_depth - <<DisplaySS>>.grid_depth) * -1
  expr: .Placement.Base.z = <<CalculatedSS>>.case_height
FEATURE [Sketcher::SketchObject] Sketch032
  ArcFitTolerance = 1e-06
  AttachmentSupport = -> [DatumPlane009]
  ExternalGeometry = -> [Binder002]
  FullyConstrained = true
  MakeInternals = false
  MapMode = 5
  Placement = pos=(0,0,98) rot=(0,0,1;0rad)
  expr: Constraints[1] = <<DisplaySS>>.screw_diameter
  expr: Constraints[3] = <<DisplaySS>>.screw_diameter
  sketch-geometry (2):
    g0: Circle CenterX=167.5 CenterY=-71 CenterZ=0 NormalX=0 NormalY=0 NormalZ=1 AngleXU=0 Radius=1
    g1: Circle CenterX=181.5 CenterY=-71 CenterZ=0 NormalX=0 NormalY=0 NormalZ=1 AngleXU=0 Radius=1
  constraints (4):
    c: Coincident(g0,g-3)
    c: Diameter(g0) = 2
    c: Coincident(g1,g-4)
    c: Diameter(g1) = 2
FEATURE [PartDesign::Pocket] Pocket015
  BaseFeature = -> LinearPattern
  Direction = (0,0,-1)
  Length = 5
  Length2 = 5
  Profile = -> Sketch032
  ReferenceAxis = -> Sketch032 [N_Axis]
  Refine = true
  Suppressed = false
  Type = 1
FEATURE [App::Link] MountBracket008  label="MountBracket"
  LinkPlacement = pos=(253,-4.4e-15,2) rot=(0,0,1;4.71239rad)
  LinkedObject = -> <external mount_bracket.FCStd>#Body003
  Placement = pos=(253,-4.4e-15,2) rot=(0,0,1;4.71239rad)
FEATURE [App::FeaturePython] Joint041  label="Fixed041"  # Assembly joint (typed FeaturePython)
  Activated = true
  AngleMax = 0
  AngleMin = 0
  Detach1 = false
  Detach2 = false
  Distance = 0
  Distance2 = 0
  EnableAngleMax = false
  EnableAngleMin = false
  EnableLengthMax = false
  EnableLengthMin = false
  JointType = 0 (Fixed)
  LengthMax = 0
  LengthMin = 0
  Offset2 = pos=(0,0,0) rot=(0,0,1;1.5708rad)
  Placement1 = pos=(-10.9259,-1e-15,0) rot=(0.707107,0,0.707107;3.14159rad)
  Placement2 = pos=(242.074,0,0) rot=(-0.57735,0.57735,0.57735;4.18879rad)
  Reference1 = -> Assembly [MountBracket008.Sketch010.Edge1,MountBracket008.Sketch010.Edge1]
  Reference2 = -> Assembly [Housing.Sketch028.Edge34,Housing.Sketch028.Edge34]
FEATURE [App::Link] MountBracket010
  LinkPlacement = pos=(253,-49.5,2) rot=(0,0,1;4.71239rad)
  LinkedObject = -> <external mount_bracket.FCStd>#Body003
  Placement = pos=(253,-49.5,2) rot=(0,0,1;4.71239rad)
FEATURE [App::Link] MountBracket011
  LinkPlacement = pos=(253,-12.5,96) rot=(0.707107,0.707107,0;3.14159rad)
  LinkedObject = -> <external mount_bracket.FCStd>#Body003
  Placement = pos=(253,-12.5,96) rot=(0.707107,0.707107,0;3.14159rad)
FEATURE [App::Link] MountBracket013
  LinkPlacement = pos=(253,-62,2) rot=(0,0,1;1.5708rad)
  LinkedObject = -> <external mount_bracket.FCStd>#Body003
  Placement = pos=(253,-62,2) rot=(0,0,1;1.5708rad)
FEATURE [App::FeaturePython] Joint043  label="Fixed043"  # Assembly joint (typed FeaturePython)
  Activated = true
  AngleMax = 0
  AngleMin = 0
  Detach1 = false
  Detach2 = false
  Distance = 0
  Distance2 = 0
  EnableAngleMax = false
  EnableAngleMin = false
  EnableLengthMax = false
  EnableLengthMin = false
  JointType = 0 (Fixed)
  LengthMax = 0
  LengthMin = 0
  Offset2 = pos=(0,0,0) rot=(0,0,1;1.5708rad)
  Placement1 = pos=(-10.9259,-1e-15,0) rot=(0.707107,0,0.707107;3.14159rad)
  Placement2 = pos=(242.074,-49.5,0) rot=(-0.57735,0.57735,0.57735;4.18879rad)
  Reference1 = -> Assembly [MountBracket010.Sketch010.Edge1,MountBracket010.Sketch010.Edge1]
  Reference2 = -> Assembly [Housing.Sketch028.Edge33,Housing.Sketch028.Edge33]
FEATURE [App::FeaturePython] Joint044  label="Fixed044"  # Assembly joint (typed FeaturePython)
  Activated = true
  AngleMax = 0
  AngleMin = 0
  Detach1 = false
  Detach2 = false
  Distance = 0
  Distance2 = 0
  EnableAngleMax = false
  EnableAngleMin = false
  EnableLengthMax = false
  EnableLengthMin = false
  JointType = 0 (Fixed)
  LengthMax = 0
  LengthMin = 0
  Offset2 = pos=(0,0,0) rot=(0,0,1;3.14159rad)
  Placement1 = pos=(12.5,-10.9259,-9e-16) rot=(0.57735,0.57735,0.57735;4.18879rad)
  Placement2 = pos=(263.926,-49.5,0) rot=(0,1,0;4.71239rad)
  Reference1 = -> Assembly [MountBracket013.Edge4,MountBracket013.Edge4]
  Reference2 = -> Assembly [Housing.Sketch028.Edge32,Housing.Sketch028.Edge32]
FEATURE [App::FeaturePython] Joint045  label="Fixed045"  # Assembly joint (typed FeaturePython)
  Activated = true
  AngleMax = 0
  AngleMin = 0
  Detach1 = false
  Detach2 = false
  Distance = 0
  Distance2 = 0
  EnableAngleMax = false
  EnableAngleMin = false
  EnableLengthMax = false
  EnableLengthMin = false
  JointType = 0 (Fixed)
  LengthMax = 0
  LengthMin = 0
  Offset1 = pos=(0,-94,0) rot=(0,0,1;0rad)
  Offset2 = pos=(0,0,0) rot=(0,0,-1;1.5708rad)
  Placement1 = pos=(-10.9259,94,0) rot=(0.707107,0,0.707107;3.14159rad)
  Placement2 = pos=(242.074,-12.5,0) rot=(0.57735,0.57735,0.57735;2.0944rad)
  Reference1 = -> Assembly [MountBracket011.Sketch010.Edge1,MountBracket011.Sketch010.Edge1]
  Reference2 = -> Assembly [Housing.Sketch028.Edge36,Housing.Sketch028.Edge36]
  expr: .Offset1.Base.y = <<CalculatedSS>>.case_clear_opening_height * -1
FEATURE [App::Link] MountBracket015
  LinkPlacement = pos=(253,-49.5,96) rot=(-0.707107,0.707107,0;3.14159rad)
  LinkedObject = -> <external mount_bracket.FCStd>#Body003
  Placement = pos=(253,-49.5,96) rot=(-0.707107,0.707107,0;3.14159rad)
FEATURE [App::FeaturePython] Joint047  label="Fixed047"  # Assembly joint (typed FeaturePython)
  Activated = true
  AngleMax = 0
  AngleMin = 0
  Detach1 = false
  Detach2 = false
  Distance = 0
  Distance2 = 0
  EnableAngleMax = false
  EnableAngleMin = false
  EnableLengthMax = false
  EnableLengthMin = false
  JointType = 0 (Fixed)
  LengthMax = 0
  LengthMin = 0
  Offset1 = pos=(0,-94,0) rot=(0,0,1;0rad)
  Offset2 = pos=(0,0,0) rot=(0,0,1;1.5708rad)
  Placement1 = pos=(-10.9259,94,0) rot=(0.707107,0,0.707107;3.14159rad)
  Placement2 = pos=(263.926,-49.5,0) rot=(-0.57735,0.57735,0.57735;4.18879rad)
  Reference1 = -> Assembly [MountBracket015.Sketch010.Edge1,MountBracket015.Sketch010.Edge1]
  Reference2 = -> Assembly [Housing.Sketch028.Edge32,Housing.Sketch028.Edge32]
  expr: .Offset1.Base.y = <<CalculatedSS>>.case_clear_opening_height * -1
FEATURE [App::Link] MountBracket016
  LinkPlacement = pos=(253,-62,96) rot=(0.707107,0.707107,0;3.14159rad)
  LinkedObject = -> <external mount_bracket.FCStd>#Body003
  Placement = pos=(253,-62,96) rot=(0.707107,0.707107,0;3.14159rad)
FEATURE [App::FeaturePython] Joint050  label="Fixed050"  # Assembly joint (typed FeaturePython)
  Activated = true
  AngleMax = 0
  AngleMin = 0
  Detach1 = false
  Detach2 = false
  Distance = 0
  Distance2 = 0
  EnableAngleMax = false
  EnableAngleMin = false
  EnableLengthMax = false
  EnableLengthMin = false
  JointType = 0 (Fixed)
  LengthMax = 0
  LengthMin = 0
  Offset1 = pos=(94,0,0) rot=(0,0,1;0rad)
  Placement1 = pos=(12.5,-10.9259,94) rot=(0.57735,0.57735,0.57735;4.18879rad)
  Placement2 = pos=(242.074,-49.5,0) rot=(-0.707107,0,0.707107;3.14159rad)
  Reference1 = -> Assembly [MountBracket016.Edge4,MountBracket016.Edge4]
  Reference2 = -> Assembly [Housing.Sketch028.Edge33,Housing.Sketch028.Edge33]
  expr: .Offset1.Base.x = <<CalculatedSS>>.case_clear_opening_height
FEATURE [App::Link] MountBracket017
  LinkPlacement = pos=(2,-4.6309e-12,2) rot=(0,0,1;0rad)
  LinkedObject = -> <external mount_bracket.FCStd>#Body003
  Placement = pos=(2,-4.6309e-12,2) rot=(0,0,1;0rad)
FEATURE [App::FeaturePython] Joint051  label="Fixed051"  # Assembly joint (typed FeaturePython)
  Activated = true
  AngleMax = 0
  AngleMin = 0
  Detach1 = false
  Detach2 = false
  Distance = 0
  Distance2 = 0
  EnableAngleMax = false
  EnableAngleMin = false
  EnableLengthMax = false
  EnableLengthMin = false
  JointType = 0 (Fixed)
  LengthMax = 0
  LengthMin = 0
  Offset2 = pos=(0,0,0) rot=(0,0,1;1.5708rad)
  Placement1 = pos=(-10.9259,-1e-15,0) rot=(0.707107,0,0.707107;3.14159rad)
  Placement2 = pos=(2,-10.9259,0) rot=(-1,0,0;4.71239rad)
  Reference1 = -> Assembly [MountBracket017.Sketch010.Edge1,MountBracket017.Sketch010.Edge1]
  Reference2 = -> Assembly [Housing.Sketch028.Edge18,Housing.Sketch028.Edge18]
FEATURE [App::Link] TwoFemaleMountBracket
  LinkPlacement = pos=(253,2.4e-15,2) rot=(0,0,1;0rad)
  LinkedObject = -> <external two_female_mount_bracket.FCStd>#Body
  Placement = pos=(253,2.4e-15,2) rot=(0,0,1;0rad)
FEATURE [App::FeaturePython] Joint052  label="Fixed052"  # Assembly joint (typed FeaturePython)
  Activated = true
  AngleMax = 0
  AngleMin = 0
  Detach1 = false
  Detach2 = false
  Distance = 0
  Distance2 = 0
  EnableAngleMax = false
  EnableAngleMin = false
  EnableLengthMax = false
  EnableLengthMin = false
  JointType = 0 (Fixed)
  LengthMax = 0
  LengthMin = 0
  Offset2 = pos=(0,0,0) rot=(0,0,1;1.5708rad)
  Placement1 = pos=(10.9259,0,0) rot=(0.707107,0,0.707107;3.14159rad)
  Placement2 = pos=(263.926,0,0) rot=(-0.57735,0.57735,0.57735;4.18879rad)
  Reference1 = -> Assembly [TwoFemaleMountBracket.Sketch.Edge1,TwoFemaleMountBracket.Sketch.Edge1]
  Reference2 = -> Assembly [Housing.Sketch028.Edge41,Housing.Sketch028.Edge41]
FEATURE [App::Link] TwoFemaleMountBracket001
  LinkPlacement = pos=(253,-3.38e-14,83.5) rot=(0,0,1;0rad)
  LinkedObject = -> <external two_female_mount_bracket.FCStd>#Body
  Placement = pos=(253,-3.38e-14,83.5) rot=(0,0,1;0rad)
FEATURE [App::FeaturePython] Joint053  label="Fixed053"  # Assembly joint (typed FeaturePython)
  Activated = true
  AngleMax = 0
  AngleMin = 0
  Detach1 = false
  Detach2 = false
  Distance = 0
  Distance2 = 0
  EnableAngleMax = false
  EnableAngleMin = false
  EnableLengthMax = false
  EnableLengthMin = false
  JointType = 0 (Fixed)
  LengthMax = 0
  LengthMin = 0
  Offset1 = pos=(0,81.5,0) rot=(0,0,1;0rad)
  Offset2 = pos=(0,0,0) rot=(0,0,1;1.5708rad)
  Placement1 = pos=(10.9259,-81.5,0) rot=(0.707107,0,0.707107;3.14159rad)
  Placement2 = pos=(263.926,0,0) rot=(-0.57735,0.57735,0.57735;4.18879rad)
  Reference1 = -> Assembly [TwoFemaleMountBracket001.Sketch.Edge1,TwoFemaleMountBracket001.Sketch.Edge1]
  Reference2 = -> Assembly [Housing.Sketch028.Edge41,Housing.Sketch028.Edge41]
  expr: .Offset1.Base.y = <<CalculatedSS>>.case_clear_opening_height - mount_bracket#<<DisplaySS>>.mount_bracket_face_size
FEATURE [Assembly::JointGroup] Joints
  Group = -> [GroundedJoint,Joint010,Joint012,Joint013,Joint014,Joint025,Joint026,Joint027,Joint032,Joint033,Joint034,Joint035,Joint036,Joint037,Joint038,Joint039,Joint040,Joint041,Joint043,Joint044,Joint045,Joint047,Joint050,Joint051,Joint052,Joint053]
FEATURE [Assembly::AssemblyObject] Assembly
  Group = -> [Joints,Housing,GroundedJoint,Screen,Exploded_Views,Exploded_View,Move,Move001,Move002,Move003,Move004,Move005,Move006,Move007,Move008,Move009,Move010,BackPlateBody,LDR,Joint010,Group,Mounting_Plate,Joint012,Grid,Joint013,Joint014,Assembly001,Group004,Joint025,Group003,Joint026,Joint027,Button_Body002,Button_Body001,Button_Body,MountStud005,MountStud006,MountStud004,MountStud007,Joint032,Joint033,+30 more]
  Origin = -> Origin005
  Type = Assembly
FEATURE [Sketcher::SketchObject] Sketch033  label="MountBracketPositionSketch"
  ArcFitTolerance = 1e-06
  AttachmentSupport = -> [DatumPlane014]
  ExternalGeometry = -> [Sketch028]
  FullyConstrained = true
  MakeInternals = false
  MapMode = 5
  Placement = pos=(0,0,2) rot=(0,0,1;0rad)
  expr: Constraints[19] = mount_bracket#<<DisplaySS>>.mount_bracket_length
  expr: Constraints[20] = mount_bracket#<<DisplaySS>>.mount_bracket_face_size
  expr: Constraints[54] = <<CalculatedSS>>.split_offset
  sketch-geometry (36):
    g0: LineSegment [constr] StartX=2 StartY=0 StartZ=0 EndX=2 EndY=-62 EndZ=0
    g1: LineSegment [constr] StartX=2 StartY=-62 StartZ=0 EndX=347 EndY=-62 EndZ=0
    g2: LineSegment [constr] StartX=347 StartY=-62 StartZ=0 EndX=347 EndY=0 EndZ=0
    g3: LineSegment [constr] StartX=347 StartY=0 StartZ=0 EndX=2 EndY=0 EndZ=0
    g4: LineSegment StartX=2 StartY=0 StartZ=0 EndX=2 EndY=-21.8519 EndZ=0
    g5: LineSegment StartX=2 StartY=-21.8519 StartZ=0 EndX=14.5 EndY=-21.8519 EndZ=0
    g6: LineSegment StartX=14.5 StartY=-21.8519 StartZ=0 EndX=14.5 EndY=0 EndZ=0
    g7: LineSegment StartX=14.5 StartY=0 StartZ=0 EndX=2 EndY=0 EndZ=0
    g8: LineSegment StartX=2 StartY=-62 StartZ=0 EndX=14.5 EndY=-62 EndZ=0
    g9: LineSegment StartX=14.5 StartY=-62 StartZ=0 EndX=14.5 EndY=-40.1481 EndZ=0
    g10: LineSegment StartX=14.5 StartY=-40.1481 StartZ=0 EndX=2 EndY=-40.1481 EndZ=0
    g11: LineSegment StartX=2 StartY=-40.1481 StartZ=0 EndX=2 EndY=-62 EndZ=0
    g12: LineSegment StartX=231.148 StartY=-12.5 StartZ=0 EndX=253 EndY=-12.5 EndZ=0
    g13: LineSegment StartX=253 StartY=-12.5 StartZ=0 EndX=253 EndY=0 EndZ=0
    g14: LineSegment StartX=253 StartY=0 StartZ=0 EndX=231.148 EndY=0 EndZ=0
    g15: LineSegment StartX=231.148 StartY=0 StartZ=0 EndX=231.148 EndY=-12.5 EndZ=0
    g16: LineSegment StartX=253 StartY=0 StartZ=0 EndX=253 EndY=-12.5 EndZ=0
    g17: LineSegment StartX=253 StartY=-12.5 StartZ=0 EndX=274.852 EndY=-12.5 EndZ=0
    g18: LineSegment StartX=274.852 StartY=-12.5 StartZ=0 EndX=274.852 EndY=0 EndZ=0
    g19: LineSegment StartX=274.852 StartY=0 StartZ=0 EndX=253 EndY=0 EndZ=0
    g20: LineSegment StartX=231.148 StartY=-62 StartZ=0 EndX=253 EndY=-62 EndZ=0
    g21: LineSegment StartX=253 StartY=-62 StartZ=0 EndX=253 EndY=-49.5 EndZ=0
    g22: LineSegment StartX=253 StartY=-49.5 StartZ=0 EndX=231.148 EndY=-49.5 EndZ=0
    g23: LineSegment StartX=231.148 StartY=-49.5 StartZ=0 EndX=231.148 EndY=-62 EndZ=0
    g24: LineSegment StartX=253 StartY=-49.5 StartZ=0 EndX=253 EndY=-62 EndZ=0
    g25: LineSegment StartX=253 StartY=-62 StartZ=0 EndX=274.852 EndY=-62 EndZ=0
    g26: LineSegment StartX=274.852 StartY=-62 StartZ=0 EndX=274.852 EndY=-49.5 EndZ=0
    g27: LineSegment StartX=274.852 StartY=-49.5 StartZ=0 EndX=253 EndY=-49.5 EndZ=0
    g28: LineSegment StartX=347 StartY=0 StartZ=0 EndX=334.5 EndY=0 EndZ=0
    g29: LineSegment StartX=334.5 StartY=0 StartZ=0 EndX=334.5 EndY=-21.8519 EndZ=0
    g30: LineSegment StartX=334.5 StartY=-21.8519 StartZ=0 EndX=347 EndY=-21.8519 EndZ=0
    g31: LineSegment StartX=347 StartY=-21.8519 StartZ=0 EndX=347 EndY=0 EndZ=0
    g32: LineSegment StartX=347 StartY=-62 StartZ=0 EndX=347 EndY=-40.1481 EndZ=0
    g33: LineSegment StartX=347 StartY=-40.1481 StartZ=0 EndX=334.5 EndY=-40.1481 EndZ=0
    g34: LineSegment StartX=334.5 StartY=-40.1481 StartZ=0 EndX=334.5 EndY=-62 EndZ=0
    g35: LineSegment StartX=334.5 StartY=-62 StartZ=0 EndX=347 EndY=-62 EndZ=0
  constraints (100):
    c: Coincident(g0,g1)
    c: Coincident(g1,g2)
    c: Coincident(g2,g3)
    c: Coincident(g3,g0)
    c: Vertical(g0)
    c: Vertical(g2)
    c: Horizontal(g1)
    c: Horizontal(g3)
    c: Coincident(g0,g-5)
    c: Coincident(g1,g-4)
    c: Coincident(g4,g5)
    c: Coincident(g5,g6)
    c: Coincident(g6,g7)
    c: Coincident(g7,g4)
    c: Vertical(g4)
    c: Vertical(g6)
    c: Horizontal(g5)
    c: Horizontal(g7)
    c: Coincident(g4,g0)
    c: Distance(g6) = 21.8519
    c: Distance(g5) = 12.5
    c: Coincident(g8,g9)
    c: Coincident(g9,g10)
    c: Coincident(g10,g11)
    c: Coincident(g11,g8)
    c: Horizontal(g8)
    c: Horizontal(g10)
    c: Vertical(g9)
    c: Vertical(g11)
    c: Coincident(g8,g0)
    c: Vertical(g9,g5)
    c: Equal(g9,g6)
    c: Coincident(g12,g13)
    c: Coincident(g13,g14)
    c: Coincident(g14,g15)
    c: Coincident(g15,g12)
    c: Horizontal(g12)
    c: Horizontal(g14)
    c: Vertical(g13)
    c: Vertical(g15)
    c: PointOnObject(g13,g3)
    c: Coincident(g16,g17)
    c: Coincident(g17,g18)
    c: Coincident(g18,g19)
    c: Coincident(g19,g16)
    c: Vertical(g16)
    c: Vertical(g18)
    c: Horizontal(g17)
    c: Horizontal(g19)
    c: Coincident(g16,g13)
    c: Equal(g15,g18)
    c: Equal(g18,g5)
    c: Equal(g17,g12)
    c: Equal(g12,g6)
    c: DistanceX(g-1,g13) = 253
    c: Coincident(g20,g21)
    c: Coincident(g21,g22)
    c: Coincident(g22,g23)
    c: Coincident(g23,g20)
    c: Horizontal(g20)
    c: Horizontal(g22)
    c: Vertical(g21)
    c: Vertical(g23)
    c: PointOnObject(g20,g1)
    c: Equal(g23,g15)
    c: Equal(g22,g12)
    c: Coincident(g24,g25)
    c: Coincident(g25,g26)
    c: Coincident(g26,g27)
    c: Coincident(g27,g24)
    c: Vertical(g24)
    c: Vertical(g26)
    c: Horizontal(g25)
    c: Horizontal(g27)
    c: Coincident(g24,g21)
    c: PointOnObject(g25,g1)
    c: Equal(g27,g17)
    c: Vertical(g21,g12)
    c: Coincident(g28,g29)
    c: Coincident(g29,g30)
    c: Coincident(g30,g31)
    c: Coincident(g31,g28)
    c: Horizontal(g28)
    c: Horizontal(g30)
    c: Vertical(g29)
    c: Vertical(g31)
    c: Coincident(g28,g2)
    c: Equal(g29,g17)
    c: Equal(g30,g18)
    c: Coincident(g32,g33)
    c: Coincident(g33,g34)
    c: Coincident(g34,g35)
    c: Coincident(g35,g32)
    c: Vertical(g32)
    c: Vertical(g34)
    c: Horizontal(g33)
    c: Horizontal(g35)
    c: Coincident(g32,g1)
    c: Vertical(g33,g29)
    c: Equal(g34,g29)
FEATURE [PartDesign::Plane] DatumPlane016  label="InternalUpperWallPlane"
  AttachmentOffset = pos=(0,0,96) rot=(0,0,1;0rad)
  AttachmentSupport = -> [XY_Plane]
  Length = 412.678
  MapMode = 5
  Placement = pos=(0,0,96) rot=(0,0,1;0rad)
  ResizeMode = 0
  Width = 138.678
  expr: .AttachmentOffset.Base.z = <<CalculatedSS>>.case_height - <<DisplaySS>>.case_thickness
FEATURE [Sketcher::SketchObject] Sketch034  label="UpperMountBracketPositionSketch"
  ArcFitTolerance = 1e-06
  AttachmentSupport = -> [DatumPlane016]
  ExternalGeometry = -> [Sketch028]
  FullyConstrained = true
  MakeInternals = false
  MapMode = 5
  Placement = pos=(0,0,96) rot=(0,0,1;0rad)
  expr: Constraints[19] = Sketch033.Constraints[19]
  expr: Constraints[20] = Sketch033.Constraints[20]
  expr: Constraints[54] = Sketch033.Constraints[54]
  sketch-geometry (36):
    g0: LineSegment [constr] StartX=2 StartY=0 StartZ=0 EndX=2 EndY=-62 EndZ=0
    g1: LineSegment [constr] StartX=2 StartY=-62 StartZ=0 EndX=347 EndY=-62 EndZ=0
    g2: LineSegment [constr] StartX=347 StartY=-62 StartZ=0 EndX=347 EndY=0 EndZ=0
    g3: LineSegment [constr] StartX=347 StartY=0 StartZ=0 EndX=2 EndY=0 EndZ=0
    g4: LineSegment StartX=2 StartY=0 StartZ=0 EndX=2 EndY=-21.8519 EndZ=0
    g5: LineSegment StartX=2 StartY=-21.8519 StartZ=0 EndX=14.5 EndY=-21.8519 EndZ=0
    g6: LineSegment StartX=14.5 StartY=-21.8519 StartZ=0 EndX=14.5 EndY=0 EndZ=0
    g7: LineSegment StartX=14.5 StartY=0 StartZ=0 EndX=2 EndY=0 EndZ=0
    g8: LineSegment StartX=2 StartY=-62 StartZ=0 EndX=14.5 EndY=-62 EndZ=0
    g9: LineSegment StartX=14.5 StartY=-62 StartZ=0 EndX=14.5 EndY=-40.1481 EndZ=0
    g10: LineSegment StartX=14.5 StartY=-40.1481 StartZ=0 EndX=2 EndY=-40.1481 EndZ=0
    g11: LineSegment StartX=2 StartY=-40.1481 StartZ=0 EndX=2 EndY=-62 EndZ=0
    g12: LineSegment StartX=231.148 StartY=-12.5 StartZ=0 EndX=253 EndY=-12.5 EndZ=0
    g13: LineSegment StartX=253 StartY=-12.5 StartZ=0 EndX=253 EndY=0 EndZ=0
    g14: LineSegment StartX=253 StartY=0 StartZ=0 EndX=231.148 EndY=0 EndZ=0
    g15: LineSegment StartX=231.148 StartY=0 StartZ=0 EndX=231.148 EndY=-12.5 EndZ=0
    g16: LineSegment StartX=253 StartY=0 StartZ=0 EndX=253 EndY=-12.5 EndZ=0
    g17: LineSegment StartX=253 StartY=-12.5 StartZ=0 EndX=274.852 EndY=-12.5 EndZ=0
    g18: LineSegment StartX=274.852 StartY=-12.5 StartZ=0 EndX=274.852 EndY=0 EndZ=0
    g19: LineSegment StartX=274.852 StartY=0 StartZ=0 EndX=253 EndY=0 EndZ=0
    g20: LineSegment StartX=231.148 StartY=-62 StartZ=0 EndX=253 EndY=-62 EndZ=0
    g21: LineSegment StartX=253 StartY=-62 StartZ=0 EndX=253 EndY=-49.5 EndZ=0
    g22: LineSegment StartX=253 StartY=-49.5 StartZ=0 EndX=231.148 EndY=-49.5 EndZ=0
    g23: LineSegment StartX=231.148 StartY=-49.5 StartZ=0 EndX=231.148 EndY=-62 EndZ=0
    g24: LineSegment StartX=253 StartY=-49.5 StartZ=0 EndX=253 EndY=-62 EndZ=0
    g25: LineSegment StartX=253 StartY=-62 StartZ=0 EndX=274.852 EndY=-62 EndZ=0
    g26: LineSegment StartX=274.852 StartY=-62 StartZ=0 EndX=274.852 EndY=-49.5 EndZ=0
    g27: LineSegment StartX=274.852 StartY=-49.5 StartZ=0 EndX=253 EndY=-49.5 EndZ=0
    g28: LineSegment StartX=347 StartY=0 StartZ=0 EndX=334.5 EndY=0 EndZ=0
    g29: LineSegment StartX=334.5 StartY=0 StartZ=0 EndX=334.5 EndY=-21.8519 EndZ=0
    g30: LineSegment StartX=334.5 StartY=-21.8519 StartZ=0 EndX=347 EndY=-21.8519 EndZ=0
    g31: LineSegment StartX=347 StartY=-21.8519 StartZ=0 EndX=347 EndY=0 EndZ=0
    g32: LineSegment StartX=347 StartY=-62 StartZ=0 EndX=347 EndY=-40.1481 EndZ=0
    g33: LineSegment StartX=347 StartY=-40.1481 StartZ=0 EndX=334.5 EndY=-40.1481 EndZ=0
    g34: LineSegment StartX=334.5 StartY=-40.1481 StartZ=0 EndX=334.5 EndY=-62 EndZ=0
    g35: LineSegment StartX=334.5 StartY=-62 StartZ=0 EndX=347 EndY=-62 EndZ=0
  constraints (100):
    c: Coincident(g0,g1)
    c: Coincident(g1,g2)
    c: Coincident(g2,g3)
    c: Coincident(g3,g0)
    c: Vertical(g0)
    c: Vertical(g2)
    c: Horizontal(g1)
    c: Horizontal(g3)
    c: Coincident(g0,g-5)
    c: Coincident(g1,g-4)
    c: Coincident(g4,g5)
    c: Coincident(g5,g6)
    c: Coincident(g6,g7)
    c: Coincident(g7,g4)
    c: Vertical(g4)
    c: Vertical(g6)
    c: Horizontal(g5)
    c: Horizontal(g7)
    c: Coincident(g4,g0)
    c: Distance(g6) = 21.8519
    c: Distance(g5) = 12.5
    c: Coincident(g8,g9)
    c: Coincident(g9,g10)
    c: Coincident(g10,g11)
    c: Coincident(g11,g8)
    c: Horizontal(g8)
    c: Horizontal(g10)
    c: Vertical(g9)
    c: Vertical(g11)
    c: Coincident(g8,g0)
    c: Vertical(g9,g5)
    c: Equal(g9,g6)
    c: Coincident(g12,g13)
    c: Coincident(g13,g14)
    c: Coincident(g14,g15)
    c: Coincident(g15,g12)
    c: Horizontal(g12)
    c: Horizontal(g14)
    c: Vertical(g13)
    c: Vertical(g15)
    c: PointOnObject(g13,g3)
    c: Coincident(g16,g17)
    c: Coincident(g17,g18)
    c: Coincident(g18,g19)
    c: Coincident(g19,g16)
    c: Vertical(g16)
    c: Vertical(g18)
    c: Horizontal(g17)
    c: Horizontal(g19)
    c: Coincident(g16,g13)
    c: Equal(g15,g18)
    c: Equal(g18,g5)
    c: Equal(g17,g12)
    c: Equal(g12,g6)
    c: DistanceX(g-1,g13) = 253
    c: Coincident(g20,g21)
    c: Coincident(g21,g22)
    c: Coincident(g22,g23)
    c: Coincident(g23,g20)
    c: Horizontal(g20)
    c: Horizontal(g22)
    c: Vertical(g21)
    c: Vertical(g23)
    c: PointOnObject(g20,g1)
    c: Equal(g23,g15)
    c: Equal(g22,g12)
    c: Coincident(g24,g25)
    c: Coincident(g25,g26)
    c: Coincident(g26,g27)
    c: Coincident(g27,g24)
    c: Vertical(g24)
    c: Vertical(g26)
    c: Horizontal(g25)
    c: Horizontal(g27)
    c: Coincident(g24,g21)
    c: PointOnObject(g25,g1)
    c: Equal(g27,g17)
    c: Vertical(g21,g12)
    c: Coincident(g28,g29)
    c: Coincident(g29,g30)
    c: Coincident(g30,g31)
    c: Coincident(g31,g28)
    c: Horizontal(g28)
    c: Horizontal(g30)
    c: Vertical(g29)
    c: Vertical(g31)
    c: Coincident(g28,g2)
    c: Equal(g29,g17)
    c: Equal(g30,g18)
    c: Coincident(g32,g33)
    c: Coincident(g33,g34)
    c: Coincident(g34,g35)
    c: Coincident(g35,g32)
    c: Vertical(g32)
    c: Vertical(g34)
    c: Horizontal(g33)
    c: Horizontal(g35)
    c: Coincident(g32,g1)
    c: Vertical(g33,g29)
    c: Equal(g34,g29)
FEATURE [PartDesign::Body] Body  label="Housing"
  AllowCompound = false
  Configuration = 0
  Group = -> [Sketch,Sketch001,Pad,Pocket,DatumPlane,DatumPlane007,DatumPlane008,Sketch015,Sketch016,DatumPlane009,DatumPlane010,DatumLine,DatumPoint,DatumLine001,DatumPlane011,Sketch019,Sketch020,Groove,Revolution,Sketch021,Pocket010,Sketch024,Pocket013,LinearPattern,DatumPlane014,Sketch028,Sketch029,Binder001,Sketch031,Binder002,Sketch032,Pocket015,Sketch033,DatumPlane016,Sketch034]
  Origin = -> Origin
  Tip = -> Pocket015
  expr: .Configuration.Enum = Spreadsheet.cells[<<A3:|>>]
FEATURE [PartDesign::Plane] DatumPlane017
  AttachmentOffset = pos=(0,0,2) rot=(0,0,1;0rad)
  AttachmentSupport = -> [XY_Plane007]
  Length = 416.896
  MapMode = 3
  Placement = pos=(0,-2,4e-16) rot=(1,0,0;1.5708rad)
  ResizeMode = 0
  Width = 165.896
  expr: .AttachmentOffset.Base.z = <<DisplaySS>>.back_plate_thickness / 2
FEATURE [Sketcher::SketchObject] Sketch039  label="CutSketch"
  ArcFitTolerance = 1e-06
  AttachmentSupport = -> [XY_Plane007]
  FullyConstrained = true
  MakeInternals = false
  MapMode = 5
  expr: Constraints[19] = <<DisplaySS>>.back_plate_thickness / 2
  expr: Constraints[20] = <<CalculatedSS>>.mount_bracket_face_size
  expr: Constraints[30] = <<DisplaySS>>.back_plate_thickness / 2
  expr: Constraints[41] = <<CalculatedSS>>.split_offset
  expr: Constraints[42] = <<CalculatedSS>>.case_width
  expr: Constraints[9] = <<DisplaySS>>.back_plate_thickness + <<DisplaySS>>.dht_depth
  sketch-geometry (16):
    g0: LineSegment StartX=0 StartY=0 StartZ=0 EndX=0 EndY=-11.7 EndZ=0
    g1: LineSegment StartX=0 StartY=-11.7 StartZ=0 EndX=240.5 EndY=-11.7 EndZ=0
    g2: LineSegment StartX=240.5 StartY=-11.7 StartZ=0 EndX=240.5 EndY=0 EndZ=0
    g3: LineSegment StartX=240.5 StartY=0 StartZ=0 EndX=0 EndY=0 EndZ=0
    g4: LineSegment StartX=240.5 StartY=0 StartZ=0 EndX=240.5 EndY=-2 EndZ=0
    g5: LineSegment StartX=240.5 StartY=-2 StartZ=0 EndX=253 EndY=-2 EndZ=0
    g6: LineSegment StartX=253 StartY=-2 StartZ=0 EndX=253 EndY=0 EndZ=0
    g7: LineSegment StartX=253 StartY=0 StartZ=0 EndX=240.5 EndY=0 EndZ=0
    g8: LineSegment StartX=240.5 StartY=-2 StartZ=0 EndX=240.5 EndY=-4 EndZ=0
    g9: LineSegment StartX=240.5 StartY=-4 StartZ=0 EndX=253 EndY=-4 EndZ=0
    g10: LineSegment StartX=253 StartY=-4 StartZ=0 EndX=253 EndY=-2 EndZ=0
    g11: LineSegment StartX=253 StartY=-2 StartZ=0 EndX=240.5 EndY=-2 EndZ=0
    g12: LineSegment StartX=253 StartY=-4 StartZ=0 EndX=349 EndY=-4 EndZ=0
    g13: LineSegment StartX=349 StartY=-4 StartZ=0 EndX=349 EndY=0 EndZ=0
    g14: LineSegment StartX=349 StartY=0 StartZ=0 EndX=253 EndY=0 EndZ=0
    g15: LineSegment StartX=253 StartY=0 StartZ=0 EndX=253 EndY=-4 EndZ=0
  constraints (43):
    c: Coincident(g0,g1)
    c: Coincident(g1,g2)
    c: Coincident(g2,g3)
    c: Coincident(g3,g0)
    c: Vertical(g0)
    c: Vertical(g2)
    c: Horizontal(g1)
    c: Horizontal(g3)
    c: Coincident(g0,g-1)
    c: Distance(g0) = 11.7
    c: Coincident(g4,g5)
    c: Coincident(g5,g6)
    c: Coincident(g6,g7)
    c: Coincident(g7,g4)
    c: Vertical(g4)
    c: Vertical(g6)
    c: Horizontal(g5)
    c: Horizontal(g7)
    c: Coincident(g4,g2)
    c: Distance(g6) = 2
    c: Distance(g5) = 12.5
    c: Coincident(g8,g9)
    c: Coincident(g9,g10)
    c: Coincident(g10,g11)
    c: Coincident(g11,g8)
    c: Vertical(g8)
    c: Vertical(g10)
    c: Horizontal(g9)
    c: Coincident(g8,g4)
    c: Coincident(g10,g5)
    c: Distance(g10) = 2
    c: Coincident(g12,g13)
    c: Coincident(g13,g14)
    c: Coincident(g14,g15)
    c: Coincident(g15,g12)
    c: Horizontal(g12)
    c: Horizontal(g14)
    c: Vertical(g13)
    c: Vertical(g15)
    c: Coincident(g12,g9)
    c: PointOnObject(g13,g-1)
    c: DistanceX(g-1,g6) = 253
    c: DistanceX(g-2,g13) = 349
FEATURE [PartDesign::Body] Body006  label="FullBackPlateBody"
  AllowCompound = false
  Group = -> [Sketch022,Pad007,Sketch023,DatumPlane012,DatumPlane013,Mirrored,Mirrored006,Sketch026,Pad008,DatumPlane015,Sketch027,Pocket014,MultiTransform,DatumPlane017,Sketch039]
  Origin = -> Origin007
  Tip = -> MultiTransform
FEATURE [PartDesign::FeatureBase] Clone
  BaseFeature = -> Body006
  Suppressed = false
FEATURE [PartDesign::FeatureBase] Clone001
  BaseFeature = -> Body006
  Suppressed = false
FEATURE [PartDesign::SubShapeBinder] Binder
  BindCopyOnChange = 0
  BindMode = 0
  ClaimChildren = false
  Context = -> Body009 [Binder.]
  Fuse = false
  MakeFace = true
  OffsetFill = false
  OffsetIntersection = false
  OffsetJoinType = 0
  OffsetOpenResult = false
  PartialLoad = false
  Refine = true
  Relative = true
  Support = -> [Body006[Sketch039.]]
  _Version = 2
FEATURE [Sketcher::SketchObject] Sketch040
  ArcFitTolerance = 1e-06
  AttachmentSupport = -> [XY_Plane011]
  ExternalGeometry = -> [Binder]
  FullyConstrained = true
  MakeInternals = false
  MapMode = 5
  expr: Constraints[9] = <<DisplaySS>>.back_plate_thickness / 2
  sketch-geometry (8):
    g0: LineSegment StartX=240.5 StartY=-4 StartZ=0 EndX=253 EndY=-4 EndZ=0
    g1: LineSegment StartX=253 StartY=-4 StartZ=0 EndX=253 EndY=-2 EndZ=0
    g2: LineSegment StartX=253 StartY=-2 StartZ=0 EndX=240.5 EndY=-2 EndZ=0
    g3: LineSegment StartX=240.5 StartY=-2 StartZ=0 EndX=240.5 EndY=-4 EndZ=0
    g4: LineSegment StartX=253 StartY=0 StartZ=0 EndX=253 EndY=-4 EndZ=0
    g5: LineSegment StartX=253 StartY=-4 StartZ=0 EndX=349 EndY=-4 EndZ=0
    g6: LineSegment StartX=349 StartY=-4 StartZ=0 EndX=349 EndY=0 EndZ=0
    g7: LineSegment StartX=349 StartY=0 StartZ=0 EndX=253 EndY=0 EndZ=0
  constraints (20):
    c: Coincident(g0,g1)
    c: Coincident(g1,g2)
    c: Coincident(g2,g3)
    c: Coincident(g3,g0)
    c: Horizontal(g2)
    c: Vertical(g1)
    c: Vertical(g3)
    c: Coincident(g0,g-3)
    c: Coincident(g0,g-4)
    c: Distance(g1) = 2
    c: Coincident(g4,g5)
    c: Coincident(g5,g6)
    c: Coincident(g6,g7)
    c: Coincident(g7,g4)
    c: Vertical(g4)
    c: Vertical(g6)
    c: Horizontal(g5)
    c: Horizontal(g7)
    c: Coincident(g4,g-6)
    c: Coincident(g5,g-7)
FEATURE [PartDesign::Pocket] Pocket017
  BaseFeature = -> Clone001
  Direction = (0,0,-1)
  Length = 98
  Length2 = 5
  Profile = -> Sketch040
  ReferenceAxis = -> Sketch040 [N_Axis]
  Refine = true
  Reversed = true
  Suppressed = false
  Type = 0
  expr: Length = <<CalculatedSS>>.case_height
FEATURE [PartDesign::SubShapeBinder] Binder003
  BindCopyOnChange = 0
  BindMode = 0
  ClaimChildren = false
  Context = -> Body008 [Binder003.]
  Fuse = false
  MakeFace = true
  OffsetFill = false
  OffsetIntersection = false
  OffsetJoinType = 0
  OffsetOpenResult = false
  PartialLoad = false
  Refine = true
  Relative = true
  Support = -> [Body006[Sketch039.]]
  _Version = 2
FEATURE [Sketcher::SketchObject] Sketch041
  ArcFitTolerance = 1e-06
  AttachmentSupport = -> [XY_Plane010]
  ExternalGeometry = -> [Binder003]
  FullyConstrained = true
  MakeInternals = false
  MapMode = 5
  expr: Constraints[18] = <<DisplaySS>>.back_plate_thickness / 2
  sketch-geometry (8):
    g0: LineSegment StartX=0 StartY=0 StartZ=0 EndX=0 EndY=-11.7 EndZ=0
    g1: LineSegment StartX=0 StartY=-11.7 StartZ=0 EndX=240.5 EndY=-11.7 EndZ=0
    g2: LineSegment StartX=240.5 StartY=-11.7 StartZ=0 EndX=240.5 EndY=0 EndZ=0
    g3: LineSegment StartX=240.5 StartY=0 StartZ=0 EndX=0 EndY=0 EndZ=0
    g4: LineSegment StartX=240.5 StartY=0 StartZ=0 EndX=240.5 EndY=-2 EndZ=0
    g5: LineSegment StartX=240.5 StartY=-2 StartZ=0 EndX=253 EndY=-2 EndZ=0
    g6: LineSegment StartX=253 StartY=-2 StartZ=0 EndX=253 EndY=0 EndZ=0
    g7: LineSegment StartX=253 StartY=0 StartZ=0 EndX=240.5 EndY=0 EndZ=0
  constraints (20):
    c: Coincident(g0,g1)
    c: Coincident(g1,g2)
    c: Coincident(g2,g3)
    c: Coincident(g3,g0)
    c: Vertical(g0)
    c: Vertical(g2)
    c: Horizontal(g1)
    c: Horizontal(g3)
    c: Coincident(g0,g-1)
    c: Coincident(g1,g-4)
    c: Coincident(g4,g5)
    c: Coincident(g5,g6)
    c: Coincident(g6,g7)
    c: Coincident(g7,g4)
    c: Vertical(g4)
    c: Vertical(g6)
    c: Horizontal(g5)
    c: Coincident(g4,g2)
    c: Distance(g6) = 2
    c: Coincident(g6,g-5)
FEATURE [PartDesign::Pocket] Pocket018
  BaseFeature = -> Clone
  Direction = (0,0,-1)
  Length = 98
  Length2 = 5
  Profile = -> Sketch041
  ReferenceAxis = -> Sketch041 [N_Axis]
  Refine = true
  Reversed = true
  Suppressed = false
  Type = 0
  expr: Length = <<CalculatedSS>>.case_height
FEATURE [PartDesign::Body] Body008  label="LeftBackPlateBody"
  AllowCompound = false
  Group = -> [Clone,Binder003,Sketch041,Pocket018]
  Origin = -> Origin010
  Tip = -> Pocket018
FEATURE [PartDesign::SubShapeBinder] Binder004
  BindCopyOnChange = 0
  BindMode = 0
  ClaimChildren = false
  Context = -> Body009 [Binder004.]
  Fuse = false
  MakeFace = true
  OffsetFill = false
  OffsetIntersection = false
  OffsetJoinType = 0
  OffsetOpenResult = false
  PartialLoad = false
  Refine = true
  Relative = true
  Support = -> [Body006[Sketch027.]]
  _Version = 2
FEATURE [Sketcher::SketchObject] Sketch042  label="MountStudSketch001"
  ArcFitTolerance = 1e-06
  AttachmentSupport = -> [XZ_Plane011]
  ExternalGeometry = -> [Binder004]
  FullyConstrained = true
  MakeInternals = false
  MapMode = 5
  Placement = pos=(0,0,0) rot=(1,0,0;1.5708rad)
  expr: Constraints[1] = mount_stud#<<MountStudSS>>.base_diameter
  sketch-geometry (2):
    g0: Circle CenterX=80.8 CenterY=23.3932 CenterZ=0 NormalX=0 NormalY=0 NormalZ=1 AngleXU=0 Radius=9.2735
    g1: LineSegment StartX=80.8 StartY=23.3932 StartZ=0 EndX=80.8 EndY=32.6667 EndZ=0
  constraints (5):
    c: Coincident(g0,g-3)
    c: Diameter(g0) = 18.547
    c: Coincident(g1,g0)
    c: PointOnObject(g1,g0)
    c: Vertical(g1)
FEATURE [PartDesign::Body] Body009  label="RightBackPlateBody"
  AllowCompound = false
  Group = -> [Clone001,Binder,Sketch040,Pocket017,Binder004,Sketch042]
  Origin = -> Origin011
  Tip = -> Pocket017

RESOLVED EXTERNAL PARTS (link-assembly join: the EXTERNAL_REF files above that resolve inside this repo's crawl, each included once):
---- part Protoboard.FCStd = doc fcstd_cc8330c3cff3 ----
FCSTD DOCUMENT  (FreeCAD 1.0R39109 (Git))
Label: Protoboard
License: All rights reserved
LicenseURL: https://en.wikipedia.org/wiki/All_rights_reserved
objects: Spreadsheet::Sheet×1, Sketcher::SketchObject×1, PartDesign::Pad×1, PartDesign::Body×1
note: 6 computed .brp shape members not serialized (recipe doc carries the construction recipe); baked Part::Feature solids carry a one-line shape summary decoded from their .brp

FEATURE [Spreadsheet::Sheet] Spreadsheet004  label="ProtoboardSS"
  cells = A1='Total Length; B1(total_length)==172.7 mm; A2='Mount Hole Spacing Length; B2(mount_spacing_length)==162.6 mm; A3='Mount Hole Spacing Width; B3(mount_spacing_width)==35.6 mm; A4='Total Width; B4(total_width)==52.1 mm; A5='Pins Width; B5(pin_width)==157.4 mm; A6='One Side Pin Margin; B6(pin_margin)==(total_length - pin_width) / 2; A7='Pitch; B7(pitch)==2.54 mm; A8='Mount to Pin Offset; B8(mount_pin_offset)==(mount_spacing_length - pin_width) / 2; A9='PCB Thickness; B9(thickness)==1.57 mm; A10='Mount Hole Side Offset; B10(mount_hole_side_offset)==(total_width - mount_spacing_width) / 2; A11='Mount Hole Top Offset; B11(mount_top_offset)==(total_length - mount_spacing_length) / 2; A12='M2 Mount Hole Size; B12(mount_hole_diameter)==2.2 mm; A13='first_pin_row_start; B13(first_pin_row_start)==(total_length - pin_width) / 2
FEATURE [Sketcher::SketchObject] Sketch020
  ArcFitTolerance = 1e-06
  AttachmentSupport = -> [XZ_Plane009]
  FullyConstrained = true
  MakeInternals = false
  MapMode = 5
  Placement = pos=(0,0,0) rot=(1,0,0;1.5708rad)
  expr: Constraints[10] = <<ProtoboardSS>>.total_length
  expr: Constraints[14] = <<ProtoboardSS>>.mount_hole_diameter
  expr: Constraints[15] = <<ProtoboardSS>>.mount_top_offset
  expr: Constraints[16] = <<ProtoboardSS>>.mount_hole_side_offset
  expr: Constraints[17] = <<ProtoboardSS>>.mount_top_offset
  expr: Constraints[18] = <<ProtoboardSS>>.total_width - <<ProtoboardSS>>.mount_hole_side_offset
  expr: Constraints[19] = <<ProtoboardSS>>.mount_hole_side_offset
  expr: Constraints[20] = <<ProtoboardSS>>.mount_top_offset
  expr: Constraints[21] = <<ProtoboardSS>>.mount_hole_side_offset
  expr: Constraints[22] = <<ProtoboardSS>>.mount_top_offset
  expr: Constraints[9] = <<ProtoboardSS>>.total_width
  sketch-geometry (12):
    g0: LineSegment StartX=0 StartY=0 StartZ=0 EndX=52.1 EndY=0 EndZ=0
    g1: LineSegment StartX=52.1 StartY=0 StartZ=0 EndX=52.1 EndY=172.7 EndZ=0
    g2: LineSegment StartX=52.1 StartY=172.7 StartZ=0 EndX=0 EndY=172.7 EndZ=0
    g3: LineSegment StartX=0 StartY=172.7 StartZ=0 EndX=0 EndY=0 EndZ=0
    g4: Circle CenterX=8.25 CenterY=167.65 CenterZ=0 NormalX=0 NormalY=0 NormalZ=1 AngleXU=0 Radius=1.1
    g5: Circle CenterX=43.85 CenterY=167.65 CenterZ=0 NormalX=0 NormalY=0 NormalZ=1 AngleXU=0 Radius=1.1
    g6: Circle CenterX=43.85 CenterY=5.05 CenterZ=0 NormalX=0 NormalY=0 NormalZ=1 AngleXU=0 Radius=1.1
    g7: Circle CenterX=8.25 CenterY=5.05 CenterZ=0 NormalX=0 NormalY=0 NormalZ=1 AngleXU=0 Radius=1.1
    g8: GeomPoint X=8.25 Y=5.05 Z=0
    g9: GeomPoint X=43.85 Y=5.05 Z=0
    g10: GeomPoint X=43.85 Y=167.65 Z=0
    g11: GeomPoint X=8.25 Y=167.65 Z=0
  constraints (27):
    c: Coincident(g0,g1)
    c: Coincident(g1,g2)
    c: Coincident(g2,g3)
    c: Coincident(g3,g0)
    c: Horizontal(g0)
    c: Horizontal(g2)
    c: Vertical(g1)
    c: Vertical(g3)
    c: Coincident(g-1,g0)
    c: Distance(g0) = 52.1
    c: Distance(g3) = 172.7
    c: Equal(g7,g6)
    c: Equal(g7,g5)
    c: Equal(g7,g4)
    c: Diameter(g7) = 2.2
    c: Distance(g4,g2) = 5.05
    c: Distance(g4,g3) = 8.25
    c: Distance(g5,g2) = 5.05
    c: Distance(g5,g3) = 43.85
    c: Distance(g7,g3) = 8.25
    c: DistanceY(g-1,g7) = 5.05
    c: Distance(g6,g1) = 8.25
    c: Distance(g6,g0) = 5.05
    c: Coincident(g8,g7)
    c: Coincident(g9,g6)
    c: Coincident(g10,g5)
    c: Coincident(g11,g4)
FEATURE [PartDesign::Pad] Pad007  label="Protoboard Pad"
  Direction = (0,-1,2e-16)
  Length = 1.57
  Length2 = 10
  Placement = pos=(0,0,0) rot=(1,0,0;1.5708rad)
  Profile = -> Sketch020
  ReferenceAxis = -> Sketch020 [N_Axis]
  Refine = true
  Suppressed = false
  Type = 0
  expr: Length = <<ProtoboardSS>>.thickness
FEATURE [PartDesign::Body] Body007  label="Protoboard Body"
  AllowCompound = false
  Group = -> [Sketch020,Pad007]
  Origin = -> Origin009
  Tip = -> Pad007
---- part button.FCStd = doc fcstd_0512d082dd11 ----
FCSTD DOCUMENT  (FreeCAD 1.0R39109 (Git))
Label: button
License: All rights reserved
LicenseURL: https://en.wikipedia.org/wiki/All_rights_reserved
objects: Sketcher::SketchObject×2, Mesh::Feature×2, PartDesign::Revolution×1, PartDesign::Pocket×1, PartDesign::Body×1, Spreadsheet::Sheet×1
note: 11 computed .brp shape members not serialized (recipe doc carries the construction recipe); baked Part::Feature solids carry a one-line shape summary decoded from their .brp
EXTERNAL_REF file=mount_stud.FCStd obj=Spreadsheet002

FEATURE [Sketcher::SketchObject] Sketch018
  ArcFitTolerance = 1e-06
  AttachmentSupport = -> [XY_Plane008]
  FullyConstrained = true
  MakeInternals = false
  MapMode = 5
  expr: Constraints[11] = <<ButtonSS>>.flange_height + <<ButtonSS>>.barrel_height
  expr: Constraints[12] = <<ButtonSS>>.flange_radius
  expr: Constraints[13] = <<ButtonSS>>.barrel_height
  expr: Constraints[14] = <<ButtonSS>>.radius
  expr: Constraints[15] = <<ButtonSS>>.flange_height
  sketch-geometry (6):
    g0: LineSegment StartX=0 StartY=0 StartZ=0 EndX=0 EndY=8 EndZ=0
    g1: LineSegment StartX=0 StartY=8 StartZ=0 EndX=10 EndY=8 EndZ=0
    g2: LineSegment StartX=10 StartY=8 StartZ=0 EndX=10 EndY=5 EndZ=0
    g3: LineSegment StartX=10 StartY=5 StartZ=0 EndX=11 EndY=7.1e-15 EndZ=0
    g4: LineSegment StartX=11 StartY=7.1e-15 StartZ=0 EndX=11 EndY=0 EndZ=0
    g5: LineSegment StartX=11 StartY=0 StartZ=0 EndX=0 EndY=0 EndZ=0
  constraints (17):
    c: Coincident(g-1,g0)
    c: PointOnObject(g0,g-2)
    c: Coincident(g0,g1)
    c: Coincident(g1,g2)
    c: Vertical(g2)
    c: Coincident(g2,g3)
    c: Coincident(g3,g4)
    c: PointOnObject(g4,g-1)
    c: Vertical(g4)
    c: Coincident(g4,g5)
    c: Coincident(g5,g0)
    c: Distance(g0) = 8
    c: Distance(g5) = 11
    c: Distance(g2) = 3
    c: DistanceX(g0,g1) = 10
    c: DistanceY(g3,g2) = 5
    c: Angle(g1,g2) = 1.5708
FEATURE [PartDesign::Revolution] Revolution
  Angle = 360
  Angle2 = 60
  Axis = (0,1,0)
  Base = (0,0,0)
  Profile = -> Sketch018
  ReferenceAxis = -> Sketch018 [V_Axis]
  Refine = true
  Reversed = true
  Suppressed = false
  Type = 0
FEATURE [Sketcher::SketchObject] Sketch019
  ArcFitTolerance = 1e-06
  AttachmentSupport = -> [XZ_Plane008]
  FullyConstrained = true
  MakeInternals = false
  MapMode = 5
  Placement = pos=(0,0,0) rot=(1,0,0;1.5708rad)
  expr: Constraints[10] = <<ButtonSS>>.mount_width
  expr: Constraints[11] = <<ButtonSS>>.mount_width
  expr: Constraints[8] = <<ButtonSS>>.mount_width / 2
  expr: Constraints[9] = <<ButtonSS>>.mount_width / 2
  sketch-geometry (4):
    g0: LineSegment StartX=-5 StartY=5 StartZ=0 EndX=-5 EndY=-5 EndZ=0
    g1: LineSegment StartX=-5 StartY=-5 StartZ=0 EndX=5 EndY=-5 EndZ=0
    g2: LineSegment StartX=5 StartY=-5 StartZ=0 EndX=5 EndY=5 EndZ=0
    g3: LineSegment StartX=5 StartY=5 StartZ=0 EndX=-5 EndY=5 EndZ=0
  constraints (12):
    c: Coincident(g0,g1)
    c: Coincident(g1,g2)
    c: Coincident(g2,g3)
    c: Coincident(g3,g0)
    c: Vertical(g0)
    c: Vertical(g2)
    c: Horizontal(g1)
    c: Horizontal(g3)
    c: Distance(g-1,g2) = 5
    c: Distance(g-1,g3) = 5
    c: Distance(g1) = 10
    c: Distance(g0) = 10
FEATURE [PartDesign::Pocket] Pocket006
  BaseFeature = -> Revolution
  Direction = (0,1,-2e-16)
  Length = 3
  Length2 = 5
  Profile = -> Sketch019
  ReferenceAxis = -> Sketch019 [N_Axis]
  Refine = true
  Suppressed = false
  Type = 0
  expr: Length = <<ButtonSS>>.mount_depth
FEATURE [PartDesign::Body] Body006  label="Button Body"
  AllowCompound = false
  Group = -> [Sketch018,Revolution,Sketch019,Pocket006]
  Origin = -> Origin008
  Tip = -> Pocket006
FEATURE [Spreadsheet::Sheet] Spreadsheet005  label="ButtonSS"
  cells = A1='Diameter; B1(diameter)==2 cm; A2='Barrel Height; B2(barrel_height)==3 mm; A3='Flange Height; B3(flange_height)==<<mount_stud>>#<<MountStudSS>>.height - 5 mm; A4='Flange Diameter Factor; B4(flange_factor)=1.1; A5='Flange Diameter; B5(flange_diameter)==diameter * flange_factor; A6='Mount Width; B6(mount_width)==10 mm; A7='Flange Transition Height; B7(flange_transition_height)==3 mm; A8='Total height; B8(total_height)==barrel_height + flange_height; A9='Radius; B9(radius)==diameter / 2; A10='Flange Radius; B10(flange_radius)==flange_diameter / 2; A11='Mount Depth; B11(mount_depth)==3 mm
FEATURE [Mesh::Feature] Mesh  label="Pocket006 (Meshed)"
FEATURE [Mesh::Feature] Mesh001  label="Pocket006 (Meshed)001"
---- part grid.FCStd = doc fcstd_6c8f9071b443 ----
FCSTD DOCUMENT  (FreeCAD 1.0R39109 (Git))
Label: grid
License: All rights reserved
LicenseURL: https://en.wikipedia.org/wiki/All_rights_reserved
objects: Sketcher::SketchObject×7, PartDesign::Mirrored×6, PartDesign::Pocket×6, PartDesign::Plane×4, PartDesign::MultiTransform×4, Spreadsheet::Sheet×2, PartDesign::LinearPattern×2, PartDesign::Pad×1, PartDesign::Body×1
note: 64 computed .brp shape members not serialized (recipe doc carries the construction recipe); baked Part::Feature solids carry a one-line shape summary decoded from their .brp

FEATURE [Spreadsheet::Sheet] Spreadsheet  label="GridDisplaySS"
  Body = 0
  cells = A1='Variant; B1='case_depth; C1='matrix_height; D1='matrix_width; E1='matrix_depth; F1='threaded_insert_depth; G1='threaded_insert_outer_diameter; H1='threaded_insert_safety_zone; I1='case_thickness; J1='grid_border_thickness; K1='grid_depth; L1='grid_intercell_spacing; M1='grid_cell_width; N1='led_x_count; O1='led_y_count; P1='grid_countersink_hole_depth; Q1='magnet_diameter; R1='magnet_height; S1='printer_tolerance_modifier; T1='screw_diameter; U1='mount_panel_exclusion_offset; V1='glass_thickness; W1='top_component_offset; X1='photoresistor_diameter; Y1='photoresistor_truncated_width; Z1='photoresistor_height; AA1='top_component_horizontal_offset; AB1='top_component_spacing; AC1='photoresistor_ledge_size; AD1='back_plate_thickness; A2==hiddenref(.Body.String); B2(case_depth)==.B3; C2(matrix_height)==.C3; D2(matrix_width)==.D3; E2(matrix_depth)==.E3; F2(threaded_insert_depth)==.F3; G2(threaded_insert_outer_diameter)==.G3; H2(threaded_insert_safety_zone)==.H3; I2(case_thickness)==.I3; J2(grid_border_thickness)==.J3; K2(grid_depth)==.K3; L2(grid_intercell_spacing)==.L3; M2(grid_cell_width)==.M3; N2(led_x_count)==.N3; O2(led_y_count)==.O3; P2(grid_countersink_hole_depth)==.P3; Q2(magnet_diameter)==.Q3; R2(magnet_height)==.R3; S2(printer_tolerance_modifier)==.S3; T2(screw_diameter)==.T3; U2(mount_panel_exclusion_offset)==.U3; V2(glass_thickness)==.V3; W2(top_component_offset)==.W3; X2(photoresistor_diameter)==.X3; Y2(photoresistor_truncated_width)==.Y3; Z2(photoresistor_height)==.Z3; AA2(top_component_horizontal_offset)==.AA3; AB2(top_component_spacing)==.AB3; AC2(photoresistor_ledge_size)==.AC3; AD2(back_plate_thickness)==.AD3; A3='A; B3==6 cm; C3==80 mm; D3==320 mm; E3==2 mm; F3==4 mm; G3==5 mm; H3==2 mm; I3==2 mm; J3==3 mm; K3==8 mm; L3==1 mm; M3==9 mm; N3=32; O3=8; P3==3 mm; Q3==5 mm; R3==2.8 mm; S3==1 mm; T3==2 mm; U3==2 cm; V3==3 mm; W3==2 cm; X3==5.1 mm; Y3==4.5 mm; Z3==2.4 mm; AA3==2 cm; AB3==0.5 cm; AC3==3 mm; AD3==4 mm
  expr: .Body.Enum = cells[<<A3:|>>]
  expr: .cells.Bind.B2.ZZ2 = tuple(.cells; <<B>> + str(hiddenref(Body) + 3); <<ZZ>> + str(hiddenref(Body) + 3))
FEATURE [Spreadsheet::Sheet] Spreadsheet001  label="GridCalculatedSS"
  cells = B1='grid_horizontal_padding; C1='grid_vertical_padding; D1='case_height; E1='case_width; F1='grid_width; G1='grid_height; H1='grid_matrix_width; I1='grid_matrix_height; J1='screw_horizontal_offset; K1='screw_vertical_offset; L1='grid_magnet_vertical_offset; M1='grid_magnet_horizontal_offset; N1='grid_magnet_depth; O1='case_clear_opening_height; P1='case_clear_opening_width; Q1='mounting_plate_thickness; R1='mount_bracket_face_size; S1='case_relative_magnet_horizontal_offset; T1='case_relative_magnet_vertical_offset; U1='split_offset; V1='screw_offset; W1='screw_diameter; X1='screw_depth; B2(grid_horizontal_padding)==<<GridDisplaySS>>.threaded_insert_outer_diameter + <<GridDisplaySS>>.threaded_insert_safety_zone * 2 + <<GridDisplaySS>>.grid_border_thickness + <<GridDisplaySS>>.grid_intercell_spacing / 2; C2(grid_vertical_padding)==screw_depth + 2 mm; D2(case_height)==grid_height + <<GridDisplaySS>>.case_thickness * 2; E2(case_width)==grid_width + <<GridDisplaySS>>.case_thickness * 2; F2(grid_width)==grid_horizontal_padding * 2 + <<GridDisplaySS>>.matrix_width; G2(grid_height)==grid_vertical_padding * 2 + <<GridDisplaySS>>.matrix_height; H2(grid_matrix_width)==grid_width - 2 * grid_horizontal_padding - 10 mm; I2(grid_matrix_height)=70; J2(screw_horizontal_offset)==grid_horizontal_padding / 2; K2(screw_vertical_offset)==mount_bracket_face_size / 2; L2(grid_magnet_vertical_offset)==grid_height / 5; M2(grid_magnet_horizontal_offset)==grid_horizontal_padding / 2; N2(grid_magnet_depth)==<<GridDisplaySS>>.magnet_height * 2; O2(case_clear_opening_height)==grid_height; P2(case_clear_opening_width)==grid_width; Q2(mounting_plate_thickness)==<<GridDisplaySS>>.matrix_depth + 3 mm; R2(mount_bracket_face_size)==screw_horizontal_offset * 2; S2(case_relative_magnet_horizontal_offset)==grid_magnet_horizontal_offset + <<GridDisplaySS>>.case_thickness; T2(case_relative_magnet_vertical_offset)==grid_magnet_vertical_offset + <<GridDisplaySS>>.case_thickness; U2(split_offset)==grid_width / 2; V2(screw_offset)==screw_diameter + 3 mm; W2(screw_diameter)==4 mm; X2(screw_depth)==5 mm
FEATURE [PartDesign::Plane] DatumPlane003  label="Horizontal Dividing Plane"
  AttachmentOffset = pos=(0,0,-47) rot=(0,0,1;0rad)
  AttachmentSupport = -> [XZ_Plane001]
  Length = 397.203
  MapMode = 3
  Placement = pos=(0,0,47) rot=(1,0,0;3.14159rad)
  ResizeMode = 0
  Width = 77.2029
  expr: .AttachmentOffset.Base.z = <<GridCalculatedSS>>.grid_height / 2 * -1
FEATURE [PartDesign::Mirrored] Mirrored006
  MirrorPlane = -> DatumPlane003
  Placement = pos=(0,0,0) rot=(1,0,0;1.5708rad)
  Refine = true
  Suppressed = false
  TransformMode = 0
FEATURE [PartDesign::Plane] DatumPlane002  label="Vertical Dividing Plane"
  AttachmentOffset = pos=(0,0,172.5) rot=(0,0,1;0rad)
  AttachmentSupport = -> [XZ_Plane001]
  Length = 134.427
  MapMode = 4
  Placement = pos=(172.5,0,-3.83e-14) rot=(0.707107,0,0.707107;3.14159rad)
  ResizeMode = 0
  Width = 65.4272
  expr: .AttachmentOffset.Base.z = <<GridCalculatedSS>>.grid_width / 2
FEATURE [PartDesign::Mirrored] Mirrored007
  MirrorPlane = -> DatumPlane002
  Placement = pos=(0,0,0) rot=(1,0,0;1.5708rad)
  Refine = true
  Suppressed = false
  TransformMode = 0
FEATURE [PartDesign::Plane] DatumPlane001  label="Grid Face Plane"
  AttachmentOffset = pos=(0,0,8) rot=(0,0,1;0rad)
  AttachmentSupport = -> [XZ_Plane001]
  Length = 411.967
  MapMode = 2
  Placement = pos=(0,-8,1.8e-15) rot=(1,0,0;1.5708rad)
  ResizeMode = 0
  Width = 160.967
  expr: .AttachmentOffset.Base.z = <<GridDisplaySS>>.grid_depth
FEATURE [Sketcher::SketchObject] Sketch017  label="ScrewHole"
  ArcFitTolerance = 1e-06
  AttachmentSupport = -> [DatumPlane001]
  FullyConstrained = true
  MakeInternals = false
  MapMode = 5
  Placement = pos=(0,-8,1.8e-15) rot=(1,0,0;1.5708rad)
  expr: Constraints[0] = <<GridDisplaySS>>.screw_diameter
  expr: Constraints[1] = <<GridCalculatedSS>>.screw_horizontal_offset
  expr: Constraints[2] = <<GridCalculatedSS>>.screw_vertical_offset
  sketch-geometry (1):
    g0: Circle CenterX=6.25 CenterY=6.25 CenterZ=0 NormalX=0 NormalY=0 NormalZ=1 AngleXU=0 Radius=1
  constraints (3):
    c: Diameter(g0) = 2
    c: DistanceX(g-2,g0) = 6.25
    c: DistanceY(g-1,g0) = 6.25
FEATURE [PartDesign::Mirrored] Mirrored002
  MirrorPlane = -> DatumPlane003
  Placement = pos=(0,0,0) rot=(1,0,0;1.5708rad)
  Refine = true
  Suppressed = false
  TransformMode = 0
FEATURE [PartDesign::Mirrored] Mirrored003
  MirrorPlane = -> DatumPlane002
  Placement = pos=(0,0,0) rot=(1,0,0;1.5708rad)
  Refine = true
  Suppressed = false
  TransformMode = 0
FEATURE [Sketcher::SketchObject] Sketch005  label="Magnet Hole"
  ArcFitTolerance = 1e-06
  AttachmentSupport = -> [DatumPlane001]
  FullyConstrained = true
  MakeInternals = false
  MapMode = 5
  Placement = pos=(0,-8,1.8e-15) rot=(1,0,0;1.5708rad)
  expr: Constraints[0] = <<GridCalculatedSS>>.grid_magnet_horizontal_offset
  expr: Constraints[1] = <<GridCalculatedSS>>.grid_magnet_vertical_offset
  expr: Constraints[2] = <<GridDisplaySS>>.magnet_diameter
  sketch-geometry (1):
    g0: Circle CenterX=6.25 CenterY=18.8 CenterZ=0 NormalX=0 NormalY=0 NormalZ=1 AngleXU=0 Radius=2.5
  constraints (3):
    c: DistanceX(g-2,g0) = 6.25
    c: DistanceY(g-1,g0) = 18.8
    c: Diameter(g0) = 5
FEATURE [PartDesign::Mirrored] Mirrored
  MirrorPlane = -> DatumPlane003
  Placement = pos=(0,0,0) rot=(1,0,0;1.5708rad)
  Refine = true
  Suppressed = false
  TransformMode = 0
FEATURE [PartDesign::Mirrored] Mirrored001
  MirrorPlane = -> DatumPlane002
  Placement = pos=(0,0,0) rot=(1,0,0;1.5708rad)
  Refine = true
  Suppressed = false
  TransformMode = 0
FEATURE [Sketcher::SketchObject] Sketch004
  ArcFitTolerance = 1e-06
  AttachmentSupport = -> [DatumPlane001]
  FullyConstrained = true
  MakeInternals = false
  MapMode = 5
  Placement = pos=(0,-8,1.8e-15) rot=(1,0,0;1.5708rad)
  expr: Constraints[0] = <<GridCalculatedSS>>.screw_vertical_offset
  expr: Constraints[1] = <<GridCalculatedSS>>.screw_horizontal_offset
  expr: Constraints[2] = <<GridDisplaySS>>.threaded_insert_outer_diameter
  sketch-geometry (1):
    g0: Circle CenterX=6.25 CenterY=6.25 CenterZ=0 NormalX=0 NormalY=0 NormalZ=1 AngleXU=0 Radius=2.5
  constraints (3):
    c: DistanceY(g-1,g0) = 6.25
    c: DistanceX(g-2,g0) = 6.25
    c: Diameter(g0) = 5
FEATURE [Sketcher::SketchObject] Sketch003
  ArcFitTolerance = 1e-06
  AttachmentSupport = -> [DatumPlane001]
  FullyConstrained = true
  MakeInternals = false
  MapMode = 5
  Placement = pos=(0,-8,1.8e-15) rot=(1,0,0;1.5708rad)
  expr: Constraints[10] = <<GridDisplaySS>>.grid_cell_width
  expr: Constraints[11] = <<GridDisplaySS>>.grid_cell_width
  expr: Constraints[8] = <<GridCalculatedSS>>.grid_horizontal_padding
  expr: Constraints[9] = <<GridCalculatedSS>>.grid_vertical_padding
  sketch-geometry (4):
    g0: LineSegment StartX=12.5 StartY=7 StartZ=0 EndX=21.5 EndY=7 EndZ=0
    g1: LineSegment StartX=21.5 StartY=7 StartZ=0 EndX=21.5 EndY=16 EndZ=0
    g2: LineSegment StartX=21.5 StartY=16 StartZ=0 EndX=12.5 EndY=16 EndZ=0
    g3: LineSegment StartX=12.5 StartY=16 StartZ=0 EndX=12.5 EndY=7 EndZ=0
  constraints (12):
    c: Coincident(g0,g1)
    c: Coincident(g1,g2)
    c: Coincident(g2,g3)
    c: Coincident(g3,g0)
    c: Horizontal(g0)
    c: Horizontal(g2)
    c: Vertical(g1)
    c: Vertical(g3)
    c: DistanceX(g-2,g0) = 12.5
    c: DistanceY(g-1,g0) = 7
    c: Distance(g0) = 9
    c: Distance(g1) = 9
FEATURE [PartDesign::LinearPattern] LinearPattern
  Direction = -> Sketch003 [H_Axis]
  Length = 310
  Mode = 0
  Occurrences = 32
  Offset = 10
  Placement = pos=(0,0,0) rot=(1,0,0;1.5708rad)
  Refine = true
  Suppressed = false
  TransformMode = 0
  expr: Length = <<GridCalculatedSS>>.grid_matrix_width
  expr: Occurrences = <<GridDisplaySS>>.led_x_count
FEATURE [PartDesign::LinearPattern] LinearPattern001
  Direction = -> Sketch003 [V_Axis]
  Length = 70
  Mode = 0
  Occurrences = 8
  Offset = 10
  Placement = pos=(0,0,0) rot=(1,0,0;1.5708rad)
  Refine = true
  Suppressed = false
  TransformMode = 0
  expr: Length = <<GridCalculatedSS>>.grid_matrix_height
  expr: Occurrences = <<GridDisplaySS>>.led_y_count
FEATURE [Sketcher::SketchObject] Sketch002
  ArcFitTolerance = 1e-06
  AttachmentSupport = -> [XZ_Plane001]
  FullyConstrained = true
  MakeInternals = false
  MapMode = 5
  Placement = pos=(0,0,0) rot=(1,0,0;1.5708rad)
  expr: Constraints[10] = <<GridCalculatedSS>>.grid_height
  expr: Constraints[9] = <<GridCalculatedSS>>.grid_width
  sketch-geometry (4):
    g0: LineSegment StartX=0 StartY=0 StartZ=0 EndX=345 EndY=0 EndZ=0
    g1: LineSegment StartX=345 StartY=0 StartZ=0 EndX=345 EndY=94 EndZ=0
    g2: LineSegment StartX=345 StartY=94 StartZ=0 EndX=0 EndY=94 EndZ=0
    g3: LineSegment StartX=0 StartY=94 StartZ=0 EndX=0 EndY=0 EndZ=0
  constraints (11):
    c: Coincident(g0,g1)
    c: Coincident(g1,g2)
    c: Coincident(g2,g3)
    c: Coincident(g3,g0)
    c: Horizontal(g0)
    c: Horizontal(g2)
    c: Vertical(g1)
    c: Vertical(g3)
    c: Coincident(g0,g-1)
    c: Distance(g0) = 345
    c: Distance(g3) = 94
FEATURE [PartDesign::Pad] Pad001
  Direction = (0,-1,2e-16)
  Length = 8
  Length2 = 10
  Placement = pos=(0,0,0) rot=(1,0,0;1.5708rad)
  Profile = -> Sketch002
  ReferenceAxis = -> Sketch002 [N_Axis]
  Refine = true
  Suppressed = false
  Type = 0
  expr: Length = <<GridDisplaySS>>.grid_depth
FEATURE [PartDesign::Pocket] Pocket001  label="GridCellPocket"
  BaseFeature = -> Pad001
  Direction = (0,1,-2e-16)
  Length = 8
  Length2 = 5
  Placement = pos=(0,0,0) rot=(1,0,0;1.5708rad)
  Profile = -> Sketch003
  ReferenceAxis = -> Sketch003 [N_Axis]
  Refine = true
  Suppressed = false
  Type = 0
  expr: Length = <<GridDisplaySS>>.grid_depth
FEATURE [PartDesign::MultiTransform] MultiTransform  label="GridCells"
  BaseFeature = -> Pocket001
  Originals = -> [Pocket001]
  Placement = pos=(0,0,0) rot=(1,0,0;1.5708rad)
  Refine = true
  Suppressed = false
  TransformMode = 0
  Transformations = -> [LinearPattern,LinearPattern001]
FEATURE [PartDesign::Pocket] Pocket002  label="ScrewCountersink"
  BaseFeature = -> MultiTransform
  Direction = (0,1,-2e-16)
  Length = 3
  Length2 = 5
  Placement = pos=(0,0,0) rot=(1,0,0;1.5708rad)
  Profile = -> Sketch004
  ReferenceAxis = -> Sketch004 [N_Axis]
  Refine = true
  Suppressed = false
  Type = 0
  expr: Length = <<GridDisplaySS>>.grid_countersink_hole_depth
FEATURE [PartDesign::MultiTransform] MultiTransform001  label="ScrewCountersinks"
  BaseFeature = -> Pocket002
  Originals = -> [Pocket002]
  Placement = pos=(0,0,0) rot=(1,0,0;1.5708rad)
  Refine = true
  Suppressed = false
  TransformMode = 0
  Transformations = -> [Mirrored,Mirrored001]
FEATURE [PartDesign::Pocket] Pocket003  label="Magnet Hole001"
  BaseFeature = -> MultiTransform001
  Direction = (0,1,-2e-16)
  Length = 5.6
  Length2 = 5
  Placement = pos=(0,0,0) rot=(1,0,0;1.5708rad)
  Profile = -> Sketch005
  ReferenceAxis = -> Sketch005 [N_Axis]
  Refine = true
  Suppressed = false
  Type = 0
  expr: Length = <<GridCalculatedSS>>.grid_magnet_depth
FEATURE [PartDesign::MultiTransform] MultiTransform002  label="Magnet Holes"
  BaseFeature = -> Pocket003
  Originals = -> [Pocket003]
  Placement = pos=(0,0,0) rot=(1,0,0;1.5708rad)
  Refine = true
  Suppressed = false
  TransformMode = 0
  Transformations = -> [Mirrored002,Mirrored003]
FEATURE [PartDesign::Pocket] Pocket008  label="ScrewHolePocket"
  BaseFeature = -> MultiTransform002
  Direction = (0,1,-2e-16)
  Length = 5
  Length2 = 5
  Placement = pos=(0,0,0) rot=(1,0,0;1.5708rad)
  Profile = -> Sketch017
  ReferenceAxis = -> Sketch017 [N_Axis]
  Refine = true
  Suppressed = false
  Type = 1
FEATURE [PartDesign::MultiTransform] MultiTransform004  label="GridCellTransform"
  BaseFeature = -> Pocket008
  Originals = -> [Pocket008]
  Placement = pos=(0,0,0) rot=(1,0,0;1.5708rad)
  Refine = true
  Suppressed = false
  TransformMode = 0
  Transformations = -> [Mirrored006,Mirrored007]
FEATURE [Sketcher::SketchObject] Sketch
  ArcFitTolerance = 1e-06
  AttachmentSupport = -> [XY_Plane001]
  FullyConstrained = true
  MakeInternals = false
  MapMode = 5
  expr: Constraints[0] = <<GridCalculatedSS>>.screw_diameter
  expr: Constraints[1] = <<GridCalculatedSS>>.screw_diameter
  expr: Constraints[2] = <<GridCalculatedSS>>.split_offset - <<GridCalculatedSS>>.screw_offset
  expr: Constraints[3] = <<GridCalculatedSS>>.screw_offset * 2
  expr: Constraints[4] = <<GridDisplaySS>>.grid_depth / 2 * -1
  sketch-geometry (2):
    g0: Circle CenterX=165.5 CenterY=-4 CenterZ=0 NormalX=0 NormalY=0 NormalZ=1 AngleXU=0 Radius=2
    g1: Circle CenterX=179.5 CenterY=-4 CenterZ=0 NormalX=0 NormalY=0 NormalZ=1 AngleXU=0 Radius=2
  constraints (6):
    c: Diameter(g1) = 4
    c: Diameter(g0) = 4
    c: DistanceX(g-2,g0) = 165.5
    c: Distance(g0,g1) = 14
    c: DistanceY(g-1,g0) = -4
    c: Horizontal(g0,g1)
FEATURE [PartDesign::Pocket] Pocket
  BaseFeature = -> MultiTransform004
  Direction = (0,0,-1)
  Length = 5
  Length2 = 5
  Placement = pos=(0,0,0) rot=(1,0,0;1.5708rad)
  Profile = -> Sketch
  ReferenceAxis = -> Sketch [N_Axis]
  Refine = true
  Reversed = true
  Suppressed = false
  Type = 0
  expr: Length = <<GridCalculatedSS>>.screw_depth
FEATURE [PartDesign::Plane] DatumPlane  label="GridTopPlane"
  AttachmentOffset = pos=(0,0,94) rot=(0,0,1;0rad)
  AttachmentSupport = -> [XY_Plane001]
  Length = 397.203
  MapMode = 5
  Placement = pos=(0,0,94) rot=(0,0,1;0rad)
  ResizeMode = 0
  Width = 77.2029
  expr: .AttachmentOffset.Base.z = <<GridCalculatedSS>>.grid_height
FEATURE [Sketcher::SketchObject] Sketch018
  ArcFitTolerance = 1e-06
  AttachmentSupport = -> [DatumPlane]
  FullyConstrained = true
  MakeInternals = false
  MapMode = 5
  Placement = pos=(0,0,94) rot=(0,0,1;0rad)
  expr: Constraints[0] = Sketch.Constraints[0]
  expr: Constraints[1] = Sketch.Constraints[1]
  expr: Constraints[2] = Sketch.Constraints[2]
  expr: Constraints[3] = Sketch.Constraints[3]
  expr: Constraints[4] = Sketch.Constraints[4]
  sketch-geometry (2):
    g0: Circle CenterX=165.5 CenterY=-4 CenterZ=0 NormalX=0 NormalY=0 NormalZ=1 AngleXU=0 Radius=2
    g1: Circle CenterX=179.5 CenterY=-4 CenterZ=0 NormalX=0 NormalY=0 NormalZ=1 AngleXU=0 Radius=2
  constraints (6):
    c: Diameter(g1) = 4
    c: Diameter(g0) = 4
    c: DistanceX(g-2,g0) = 165.5
    c: Distance(g0,g1) = 14
    c: DistanceY(g-1,g0) = -4
    c: Horizontal(g0,g1)
FEATURE [PartDesign::Pocket] Pocket009
  BaseFeature = -> Pocket
  Direction = (0,0,-1)
  Length = 5
  Length2 = 5
  Placement = pos=(0,0,0) rot=(1,0,0;1.5708rad)
  Profile = -> Sketch018
  ReferenceAxis = -> Sketch018 [N_Axis]
  Refine = true
  Suppressed = false
  Type = 0
  expr: Length = <<GridCalculatedSS>>.screw_depth
FEATURE [PartDesign::Body] Body001  label="Grid"
  AllowCompound = false
  Group = -> [Sketch002,Pad001,DatumPlane001,Sketch003,Pocket001,MultiTransform,LinearPattern,LinearPattern001,Sketch004,Pocket002,DatumPlane002,DatumPlane003,MultiTransform001,Mirrored,Mirrored001,Sketch005,Pocket003,MultiTransform002,Mirrored002,Mirrored003,Sketch017,Pocket008,MultiTransform004,Mirrored006,Mirrored007,Sketch,Pocket,DatumPlane,Sketch018,Pocket009]
  Origin = -> Origin001
  Tip = -> Pocket009
---- part mount_bracket.FCStd = doc fcstd_4642901b0343 ----
FCSTD DOCUMENT  (FreeCAD 1.0R39109 (Git))
Label: mount_bracket
License: All rights reserved
LicenseURL: https://en.wikipedia.org/wiki/All_rights_reserved
objects: Sketcher::SketchObject×3, PartDesign::Pocket×2, Spreadsheet::Sheet×1, PartDesign::Plane×1, PartDesign::Pad×1, PartDesign::Body×1
note: 17 computed .brp shape members not serialized (recipe doc carries the construction recipe); baked Part::Feature solids carry a one-line shape summary decoded from their .brp

FEATURE [Spreadsheet::Sheet] Spreadsheet  label="DisplaySS"
  Configuration = 1
  cells = A1='Variant; B1='threaded_insert_depth; C1='squared_profile_section_length; D1='threaded_insert_outer_diameter; E1='threaded_insert_safety_zone; F1='mount_bracket_face_size; G1='mount_bracket_length; H1='mount_bracket_draft_angle; I1='rear_countersink_offset; J1='rear_countersink_diameter; K1='rear_countersink_depth; A2==hiddenref(.Configuration.String); B2(threaded_insert_depth)==.B4; C2(squared_profile_section_length)==.C4; D2(threaded_insert_outer_diameter)==.D4; E2(threaded_insert_safety_zone)==.E4; F2(mount_bracket_face_size)==.F4; G2(mount_bracket_length)==.G4; H2(mount_bracket_draft_angle)==.H4; I2(rear_countersink_offset)==.I4; J2(rear_countersink_diameter)==.J4; K2(rear_countersink_depth)==.K4; A3='Female; B3==4 mm; C3==threaded_insert_depth; D3==5 mm; E3==2 mm; F3==12.5 mm; G3==mount_bracket_face_size / tan(mount_bracket_draft_angle) + threaded_insert_depth; H3==35 deg; I3==0 mm; J3==threaded_insert_outer_diameter; K3==threaded_insert_depth; A4='Male; B4==50 mm; C4==4 mm; D4==2 mm; E4==1 mm; F4==12.5 mm; G4==mount_bracket_face_size / tan(mount_bracket_draft_angle) + squared_profile_section_length; H4==35 deg; I4==squared_profile_section_length; J4==4 mm; K4==mount_bracket_length
  expr: .Configuration.Enum = cells[<<A3:|>>]
  expr: .cells.Bind.B2.ZZ2 = tuple(.cells; <<B>> + str(hiddenref(Configuration) + 3); <<ZZ>> + str(hiddenref(Configuration) + 3))
FEATURE [Sketcher::SketchObject] Sketch011  label="Threaded Barrel"
  ArcFitTolerance = 1e-06
  AttachmentSupport = -> [XZ_Plane003]
  FullyConstrained = true
  MakeInternals = false
  MapMode = 5
  Placement = pos=(0,0,0) rot=(1,0,0;1.5708rad)
  expr: Constraints[0] = <<DisplaySS>>.threaded_insert_outer_diameter
  expr: Constraints[1] = <<DisplaySS>>.mount_bracket_face_size / 2
  expr: Constraints[2] = <<DisplaySS>>.mount_bracket_face_size / 2
  sketch-geometry (1):
    g0: Circle CenterX=6.25 CenterY=6.25 CenterZ=0 NormalX=0 NormalY=0 NormalZ=1 AngleXU=0 Radius=1
  constraints (3):
    c: Diameter(g0) = 2
    c: DistanceY(g-1,g0) = 6.25
    c: DistanceX(g-2,g0) = 6.25
FEATURE [Sketcher::SketchObject] Sketch010
  ArcFitTolerance = 1e-06
  AttachmentSupport = -> [XY_Plane003]
  FullyConstrained = true
  MakeInternals = false
  MapMode = 4
  Placement = pos=(0,0,0) rot=(0.57735,0.57735,0.57735;2.0944rad)
  expr: Constraints[10] = <<DisplaySS>>.mount_bracket_face_size
  expr: Constraints[8] = <<DisplaySS>>.mount_bracket_draft_angle
  expr: Constraints[9] = <<DisplaySS>>.squared_profile_section_length
  sketch-geometry (4):
    g0: LineSegment StartX=-21.8519 StartY=-1.8e-15 StartZ=0 EndX=0 EndY=0 EndZ=0
    g1: LineSegment StartX=0 StartY=0 StartZ=0 EndX=0 EndY=12.5 EndZ=0
    g2: LineSegment StartX=0 StartY=12.5 StartZ=0 EndX=-4 EndY=12.5 EndZ=0
    g3: LineSegment StartX=-4 StartY=12.5 StartZ=0 EndX=-21.8519 EndY=-1.8e-15 EndZ=0
  constraints (11):
    c: PointOnObject(g0,g-1)
    c: Coincident(g0,g-1)
    c: Coincident(g0,g1)
    c: PointOnObject(g1,g-2)
    c: Coincident(g1,g2)
    c: Horizontal(g2)
    c: Coincident(g2,g3)
    c: Coincident(g3,g0)
    c: Angle(g0,g3) = 0.610865
    c: Distance(g2) = 4
    c: Distance(g1) = 12.5
FEATURE [PartDesign::Plane] DatumPlane  label="CountersinkPlane"
  AttachmentOffset = pos=(0,0,4) rot=(0,0,1;0rad)
  AttachmentSupport = -> [XZ_Plane003]
  Length = 60
  MapMode = 5
  Placement = pos=(0,-4,9e-16) rot=(1,0,0;1.5708rad)
  ResizeMode = 0
  Width = 60
  expr: .AttachmentOffset.Base.z = <<DisplaySS>>.rear_countersink_offset
FEATURE [Sketcher::SketchObject] Sketch  label="CountersinkSketch"
  ArcFitTolerance = 1e-06
  AttachmentSupport = -> [DatumPlane]
  ExternalGeometry = -> [Sketch011]
  FullyConstrained = true
  MakeInternals = false
  MapMode = 5
  Placement = pos=(0,-4,9e-16) rot=(1,0,0;1.5708rad)
  expr: Constraints[1] = <<DisplaySS>>.rear_countersink_diameter
  sketch-geometry (1):
    g0: Circle CenterX=6.25 CenterY=6.25 CenterZ=0 NormalX=0 NormalY=0 NormalZ=1 AngleXU=0 Radius=2
  constraints (2):
    c: Coincident(g0,g-3)
    c: Diameter(g0) = 4
FEATURE [PartDesign::Pad] Pad006
  Direction = (1,0,0)
  Length = 12.5
  Length2 = 10
  Profile = -> Sketch010
  ReferenceAxis = -> Sketch010 [N_Axis]
  Refine = true
  Suppressed = false
  Type = 0
  expr: Length = <<DisplaySS>>.mount_bracket_face_size
FEATURE [PartDesign::Pocket] Pocket015
  BaseFeature = -> Pad006
  Direction = (0,1,-2e-16)
  Length = 50
  Length2 = 5
  Profile = -> Sketch011
  ReferenceAxis = -> Sketch011 [N_Axis]
  Refine = true
  Reversed = true
  Suppressed = false
  Type = 0
  expr: Length = <<DisplaySS>>.threaded_insert_depth
FEATURE [PartDesign::Pocket] Pocket
  BaseFeature = -> Pocket015
  Direction = (0,1,-2e-16)
  Length = 21.8519
  Length2 = 5
  Profile = -> Sketch
  ReferenceAxis = -> Sketch [N_Axis]
  Refine = true
  Reversed = true
  Suppressed = false
  Type = 0
  expr: Length = <<DisplaySS>>.rear_countersink_depth
FEATURE [PartDesign::Body] Body003  label="MountBracket"
  AllowCompound = false
  Group = -> [Sketch010,Pad006,Sketch011,Pocket015,Sketch,Pocket,DatumPlane]
  Origin = -> Origin003
  Tip = -> Pocket
---- part mount_stud.FCStd = doc fcstd_6881cdc6e3de ----
FCSTD DOCUMENT  (FreeCAD 1.0R39109 (Git))
Label: mount_stud
License: All rights reserved
LicenseURL: https://en.wikipedia.org/wiki/All_rights_reserved
objects: Spreadsheet::Sheet×1, Sketcher::SketchObject×1, PartDesign::Revolution×1, PartDesign::Body×1
note: 6 computed .brp shape members not serialized (recipe doc carries the construction recipe); baked Part::Feature solids carry a one-line shape summary decoded from their .brp

FEATURE [Spreadsheet::Sheet] Spreadsheet002  label="MountStudSS"
  Body = 0
  cells = B1='height; C1='base_diameter; D1='top_diameter; E1='barrel_diameter; F1='barrel_depth; G1='depth_padding; H1='horizontal_padding; I1='slope_angle; J1='top_diameter_excluding_barrel; A2==hiddenref(.Body.String); B2(height)==.B3; C2(base_diameter)==.C3; D2(top_diameter)==.D3; E2(barrel_diameter)==.E3; F2(barrel_depth)==.F3; G2(depth_padding)==.G3; H2(horizontal_padding)==.H3; I2(slope_angle)==.I3; J2(top_diameter_excluding_barrel)==.J3; A3='M2 Heated; B3==10 mm; C3==tan(slope_angle) * height * 2 + top_diameter; D3==barrel_diameter + horizontal_padding; E3==5 mm; F3==4 mm; G3==2 mm; H3==2 mm; I3==30 deg; J3==top_diameter - barrel_diameter
  expr: .Body.Enum = cells[<<A3:|>>]
  expr: .cells.Bind.B2.ZZ2 = tuple(.cells; <<B>> + str(hiddenref(Body) + 3); <<ZZ>> + str(hiddenref(Body) + 3))
FEATURE [Sketcher::SketchObject] Sketch
  ArcFitTolerance = 1e-06
  AttachmentSupport = -> [XZ_Plane]
  FullyConstrained = true
  MakeInternals = false
  MapMode = 5
  Placement = pos=(0,0,0) rot=(1,0,0;1.5708rad)
  expr: Constraints[10] = <<MountStudSS>>.barrel_diameter / 2
  expr: Constraints[13] = <<MountStudSS>>.barrel_depth
  expr: Constraints[14] = <<MountStudSS>>.top_diameter_excluding_barrel
  expr: Constraints[15] = <<MountStudSS>>.height
  expr: Constraints[16] = <<MountStudSS>>.base_diameter / 2
  sketch-geometry (6):
    g0: LineSegment StartX=2.5 StartY=10 StartZ=0 EndX=2.5 EndY=6 EndZ=0
    g1: LineSegment StartX=2.5 StartY=6 StartZ=0 EndX=0 EndY=6 EndZ=0
    g2: LineSegment StartX=0 StartY=6 StartZ=0 EndX=0 EndY=0 EndZ=0
    g3: LineSegment StartX=0 StartY=0 StartZ=0 EndX=9.2735 EndY=0 EndZ=0
    g4: LineSegment StartX=9.2735 StartY=0 StartZ=0 EndX=4.5 EndY=10 EndZ=0
    g5: LineSegment StartX=4.5 StartY=10 StartZ=0 EndX=2.5 EndY=10 EndZ=0
  constraints (17):
    c: Vertical(g0)
    c: Coincident(g0,g1)
    c: Coincident(g1,g2)
    c: Coincident(g2,g-1)
    c: Vertical(g2)
    c: Coincident(g2,g3)
    c: PointOnObject(g3,g-1)
    c: Coincident(g3,g4)
    c: Coincident(g4,g5)
    c: Coincident(g5,g0)
    c: Distance(g1) = 2.5
    c: Angle(g0,g1) = 1.5708
    c: Angle(g0,g5) = 1.5708
    c: Distance(g0) = 4
    c: Distance(g5) = 2
    c: DistanceY(g-1,g0) = 10
    c: Distance(g3) = 9.2735
FEATURE [PartDesign::Revolution] Revolution
  Angle = 360
  Angle2 = 60
  Axis = (0,2e-16,1)
  Base = (0,0,0)
  Placement = pos=(0,0,0) rot=(1,0,0;1.5708rad)
  Profile = -> Sketch
  ReferenceAxis = -> Sketch [V_Axis]
  Refine = true
  Reversed = true
  Suppressed = false
  Type = 0
FEATURE [PartDesign::Body] Body  label="MountStud"
  AllowCompound = false
  Group = -> [Sketch,Revolution]
  Origin = -> Origin
  Tip = -> Revolution
---- part two_female_mount_bracket.FCStd = doc fcstd_ec417903da43 ----
FCSTD DOCUMENT  (FreeCAD 1.0R39109 (Git))
Label: two_female_mount_bracket
License: All rights reserved
LicenseURL: https://en.wikipedia.org/wiki/All_rights_reserved
objects: Sketcher::SketchObject×3, PartDesign::Pocket×2, PartDesign::Pad×1, PartDesign::SubShapeBinder×1, PartDesign::Body×1, Spreadsheet::Sheet×1
note: 17 computed .brp shape members not serialized (recipe doc carries the construction recipe); baked Part::Feature solids carry a one-line shape summary decoded from their .brp
EXTERNAL_REF file=mount_bracket.FCStd obj=Spreadsheet
EXTERNAL_REF file=mount_bracket.FCStd obj=Body003

FEATURE [Sketcher::SketchObject] Sketch
  ArcFitTolerance = 1e-06
  AttachmentSupport = -> [XZ_Plane]
  FullyConstrained = true
  MakeInternals = false
  MapMode = 5
  Placement = pos=(0,0,0) rot=(1,0,0;1.5708rad)
  expr: Constraints[10] = mount_bracket#<<DisplaySS>>.mount_bracket_face_size
  expr: Constraints[9] = mount_bracket#<<DisplaySS>>.mount_bracket_length
  sketch-geometry (4):
    g0: LineSegment StartX=0 StartY=0 StartZ=0 EndX=21.8519 EndY=0 EndZ=0
    g1: LineSegment StartX=21.8519 StartY=0 StartZ=0 EndX=21.8519 EndY=12.5 EndZ=0
    g2: LineSegment StartX=21.8519 StartY=12.5 StartZ=0 EndX=0 EndY=12.5 EndZ=0
    g3: LineSegment StartX=0 StartY=12.5 StartZ=0 EndX=0 EndY=0 EndZ=0
  constraints (11):
    c: Coincident(g0,g1)
    c: Coincident(g1,g2)
    c: Coincident(g2,g3)
    c: Coincident(g3,g0)
    c: Horizontal(g0)
    c: Horizontal(g2)
    c: Vertical(g1)
    c: Vertical(g3)
    c: Coincident(g0,g-1)
    c: Distance(g2) = 21.8519
    c: Distance(g1) = 12.5
FEATURE [PartDesign::Pad] Pad
  Direction = (0,-1,2e-16)
  Length = 12.5
  Length2 = 10
  Placement = pos=(0,0,0) rot=(1,0,0;1.5708rad)
  Profile = -> Sketch
  ReferenceAxis = -> Sketch [N_Axis]
  Refine = true
  Suppressed = false
  Type = 0
  expr: Length = <<mount_bracket>>#<<DisplaySS>>.mount_bracket_face_size
FEATURE [PartDesign::SubShapeBinder] Binder
  BindCopyOnChange = 0
  BindMode = 0
  ClaimChildren = false
  Context = -> Body [Binder.]
  Fuse = false
  MakeFace = true
  OffsetFill = false
  OffsetIntersection = false
  OffsetJoinType = 0
  OffsetOpenResult = false
  PartialLoad = false
  Placement = pos=(0,0,0) rot=(0.57735,-0.57735,0.57735;2.0944rad)
  Refine = true
  Relative = true
  Support = -> [<external mount_bracket.FCStd>#Body003[Sketch011.]]
  _Version = 2
FEATURE [Sketcher::SketchObject] Sketch001
  ArcFitTolerance = 1e-06
  AttachmentSupport = -> [YZ_Plane]
  ExternalGeometry = -> [Binder]
  FullyConstrained = true
  MakeInternals = false
  MapMode = 5
  Placement = pos=(0,0,0) rot=(0.57735,0.57735,0.57735;2.0944rad)
  expr: Constraints[1] = mount_bracket#<<DisplaySS>>.threaded_insert_outer_diameter
  sketch-geometry (1):
    g0: Circle CenterX=-6.25 CenterY=6.25 CenterZ=0 NormalX=0 NormalY=0 NormalZ=1 AngleXU=0 Radius=1
  constraints (2):
    c: Coincident(g0,g-3)
    c: Diameter(g0) = 2
FEATURE [PartDesign::Pocket] Pocket
  BaseFeature = -> Pad
  Direction = (-1,0,0)
  Length = 50
  Length2 = 5
  Placement = pos=(0,0,0) rot=(1,0,0;1.5708rad)
  Profile = -> Sketch001
  ReferenceAxis = -> Sketch001 [N_Axis]
  Refine = true
  Reversed = true
  Suppressed = false
  Type = 0
  expr: Length = <<mount_bracket>>#<<DisplaySS>>.threaded_insert_depth
FEATURE [Sketcher::SketchObject] Sketch002
  ArcFitTolerance = 1e-06
  AttachmentSupport = -> [XZ_Plane]
  ExternalGeometry = -> [Sketch]
  FullyConstrained = true
  MakeInternals = false
  MapMode = 5
  Placement = pos=(0,0,0) rot=(1,0,0;1.5708rad)
  expr: Constraints[0] = <<mount_bracket>>#<<DisplaySS>>.threaded_insert_outer_diameter
  expr: Constraints[1] = mount_bracket#<<DisplaySS>>.mount_bracket_face_size / 2
  expr: Constraints[2] = mount_bracket#<<DisplaySS>>.mount_bracket_face_size / 2
  sketch-geometry (1):
    g0: Circle CenterX=15.6019 CenterY=6.25 CenterZ=0 NormalX=0 NormalY=0 NormalZ=1 AngleXU=0 Radius=1
  constraints (3):
    c: Diameter(g0) = 2
    c: DistanceY(g-1,g0) = 6.25
    c: Distance(g0,g-3) = 6.25
FEATURE [PartDesign::Pocket] Pocket001
  BaseFeature = -> Pocket
  Direction = (0,1,-2e-16)
  Length = 50
  Length2 = 5
  Placement = pos=(0,0,0) rot=(1,0,0;1.5708rad)
  Profile = -> Sketch002
  ReferenceAxis = -> Sketch002 [N_Axis]
  Refine = true
  Reversed = true
  Suppressed = false
  Type = 0
  expr: Length = mount_bracket#<<DisplaySS>>.threaded_insert_depth
FEATURE [PartDesign::Body] Body  label="TwoFemaleMountBracket"
  AllowCompound = false
  Group = -> [Sketch,Pad,Binder,Sketch001,Pocket,Sketch002,Pocket001]
  Origin = -> Origin
  Tip = -> Pocket001
FEATURE [Spreadsheet::Sheet] Spreadsheet  label="DisplaySS"
  Configuration = 1
  cells = A1='Variant; B1='threaded_insert_depth; C1='squared_profile_section_length; D1='threaded_insert_outer_diameter; E1='threaded_insert_safety_zone; F1='mount_bracket_face_size; G1='mount_bracket_length; H1='mount_bracket_draft_angle; I1='rear_countersink_offset; J1='rear_countersink_diameter; K1='rear_countersink_depth; A2==hiddenref(.Configuration.String); B2(threaded_insert_depth)==.B4; C2(squared_profile_section_length)==.C4; D2(threaded_insert_outer_diameter)==.D4; E2(threaded_insert_safety_zone)==.E4; F2(mount_bracket_face_size)==.F4; G2(mount_bracket_length)==.G4; H2(mount_bracket_draft_angle)==.H4; I2(rear_countersink_offset)==.I4; J2(rear_countersink_diameter)==.J4; K2(rear_countersink_depth)==.K4; A3='Female; B3==4 mm; C3==threaded_insert_depth; D3==5 mm; E3==2 mm; F3==12.5 mm; G3==mount_bracket_face_size / tan(mount_bracket_draft_angle) + threaded_insert_depth; H3==35 deg; I3==0 mm; J3==threaded_insert_outer_diameter; K3==threaded_insert_depth; A4='Male; B4==50 mm; C4==4 mm; D4==2 mm; E4==1 mm; F4==12.5 mm; G4==mount_bracket_face_size / tan(mount_bracket_draft_angle) + squared_profile_section_length; H4==35 deg; I4==squared_profile_section_length; J4==4 mm; K4==mount_bracket_length
  expr: .Configuration.Enum = cells[<<A3:|>>]
  expr: .cells.Bind.B2.ZZ2 = tuple(.cells; <<B>> + str(hiddenref(Configuration) + 3); <<ZZ>> + str(hiddenref(Configuration) + 3))
